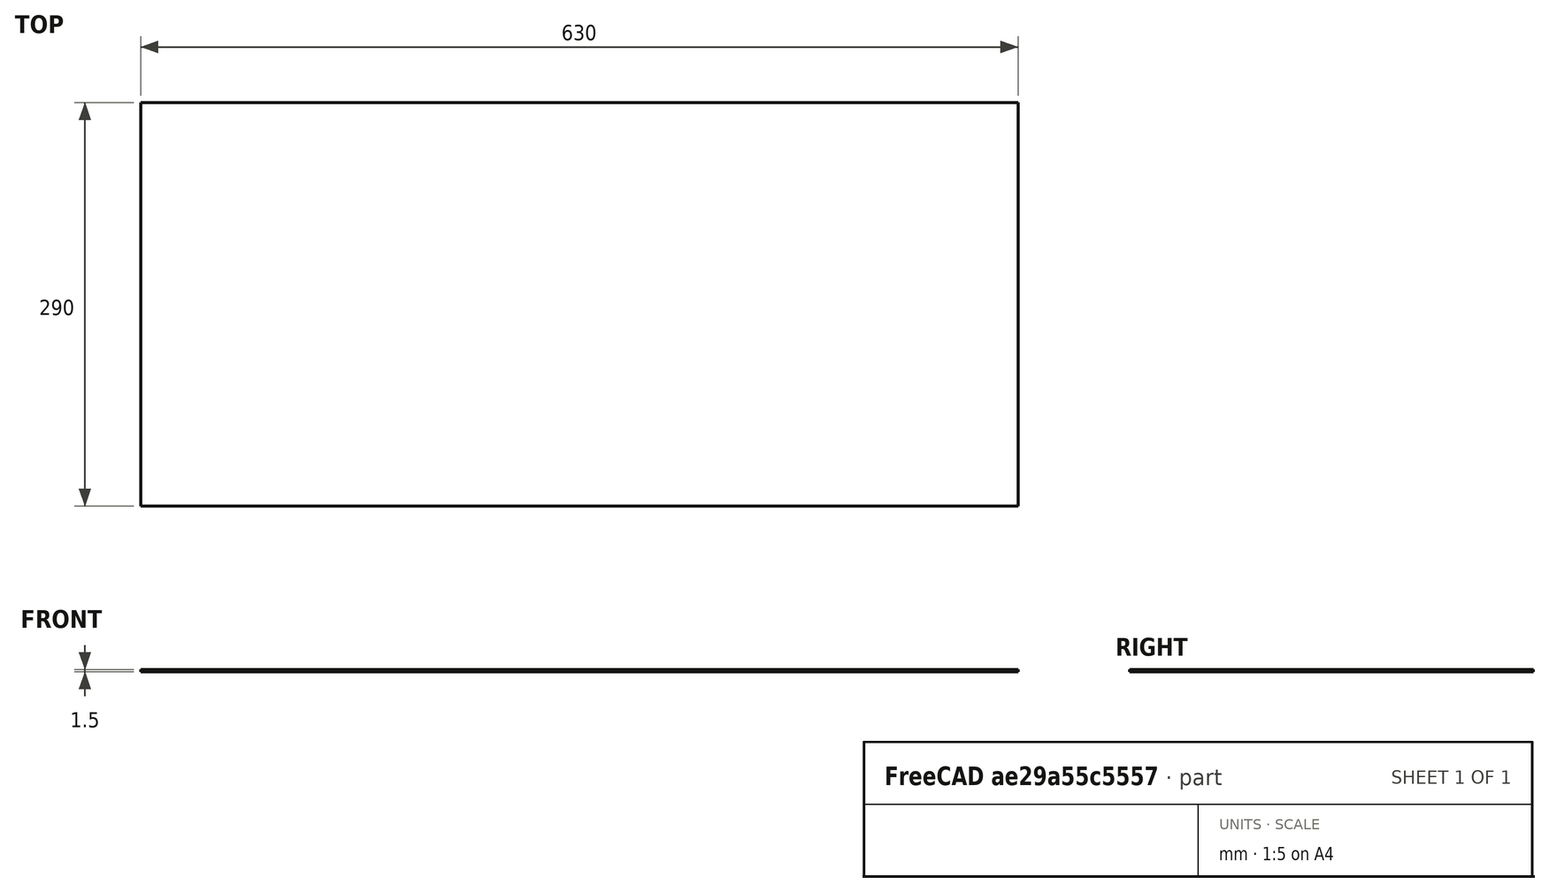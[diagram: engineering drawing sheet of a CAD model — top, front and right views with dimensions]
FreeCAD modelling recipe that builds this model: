
FCSTD DOCUMENT  (FreeCAD 0.21R33771 (Git))
Label: model
License: All rights reserved
LicenseURL: http://en.wikipedia.org/wiki/All_rights_reserved
objects: Sketcher::SketchObject×10, PartDesign::Pad×1, PartDesign::Body×1
note: 13 computed .brp shape members not serialized (recipe doc carries the construction recipe); baked Part::Feature solids carry a one-line shape summary decoded from their .brp

FEATURE [Sketcher::SketchObject] Sketch  label="plate"
  FullyConstrained = true
  MapMode = 5
  Support = -> [XY_Plane]
  sketch-geometry (4):
    g0: LineSegment StartX=-315 StartY=145 StartZ=0 EndX=315 EndY=145 EndZ=0
    g1: LineSegment StartX=315 StartY=145 StartZ=0 EndX=315 EndY=-145 EndZ=0
    g2: LineSegment StartX=315 StartY=-145 StartZ=0 EndX=-315 EndY=-145 EndZ=0
    g3: LineSegment StartX=-315 StartY=-145 StartZ=0 EndX=-315 EndY=145 EndZ=0
  constraints (12):
    c: Coincident(g0,g1)
    c: Coincident(g1,g2)
    c: Coincident(g2,g3)
    c: Coincident(g3,g0)
    c: Horizontal(g0)
    c: Horizontal(g2)
    c: Vertical(g1)
    c: Vertical(g3)
    c: DistanceX(g0,g0) = 630
    c: DistanceY(g1,g1) = 290
    c: DistanceX(g-1,g0) = 315
    c: DistanceY(g-1,g0) = 145
FEATURE [PartDesign::Pad] Pad
  Direction = (0,0,1)
  Length = 1.5
  Length2 = 10
  Profile = -> Sketch
  ReferenceAxis = -> Sketch [N_Axis]
  Type = 0
FEATURE [Sketcher::SketchObject] Sketch001  label="faderwing0"
  ExternalGeometry = -> [Pad]
  FullyConstrained = true
  MapMode = 5
  Placement = pos=(0,0,1.5) rot=(0,0,1;0rad)
  Support = -> [Pad]
  sketch-geometry (120):
    g0: Circle CenterX=-295 CenterY=128 CenterZ=0 NormalX=0 NormalY=0 NormalZ=1 AngleXU=0 Radius=5
    g1: LineSegment StartX=-302 StartY=111 StartZ=0 EndX=-288 EndY=111 EndZ=0
    g2: LineSegment StartX=-288 StartY=111 StartZ=0 EndX=-288 EndY=97 EndZ=0
    g3: LineSegment StartX=-288 StartY=97 StartZ=0 EndX=-302 EndY=97 EndZ=0
    g4: LineSegment StartX=-302 StartY=97 StartZ=0 EndX=-302 EndY=111 EndZ=0
    g5: LineSegment StartX=-309 StartY=44 StartZ=0 EndX=-281 EndY=44 EndZ=0
    g6: LineSegment StartX=-281 StartY=44 StartZ=0 EndX=-281 EndY=30 EndZ=0
    g7: LineSegment StartX=-281 StartY=30 StartZ=0 EndX=-309 EndY=30 EndZ=0
    g8: LineSegment StartX=-309 StartY=30 StartZ=0 EndX=-309 EndY=44 EndZ=0
    g9: LineSegment StartX=-302 StartY=91 StartZ=0 EndX=-288 EndY=91 EndZ=0
    g10: LineSegment StartX=-288 StartY=91 StartZ=0 EndX=-288 EndY=77 EndZ=0
    g11: LineSegment StartX=-288 StartY=77 StartZ=0 EndX=-302 EndY=77 EndZ=0
    g12: LineSegment StartX=-302 StartY=77 StartZ=0 EndX=-302 EndY=91 EndZ=0
    g13: Circle CenterX=-295 CenterY=60 CenterZ=0 NormalX=0 NormalY=0 NormalZ=1 AngleXU=0 Radius=5
    g14: Circle CenterX=-295 CenterY=15 CenterZ=0 NormalX=0 NormalY=0 NormalZ=1 AngleXU=0 Radius=1.5
    g15: LineSegment StartX=-296 StartY=9 StartZ=0 EndX=-294 EndY=9 EndZ=0
    g16: LineSegment StartX=-294 StartY=9 StartZ=0 EndX=-294 EndY=-99 EndZ=0
    g17: LineSegment StartX=-294 StartY=-99 StartZ=0 EndX=-296 EndY=-99 EndZ=0
    g18: LineSegment StartX=-296 StartY=-99 StartZ=0 EndX=-296 EndY=9 EndZ=0
    g19: Circle CenterX=-295 CenterY=-105 CenterZ=0 NormalX=0 NormalY=0 NormalZ=1 AngleXU=0 Radius=1.5
    g20: LineSegment StartX=-302 StartY=-121 StartZ=0 EndX=-288 EndY=-121 EndZ=0
    g21: LineSegment StartX=-288 StartY=-121 StartZ=0 EndX=-288 EndY=-135 EndZ=0
    g22: LineSegment StartX=-288 StartY=-135 StartZ=0 EndX=-302 EndY=-135 EndZ=0
    g23: LineSegment StartX=-302 StartY=-135 StartZ=0 EndX=-302 EndY=-121 EndZ=0
    g24: Circle CenterX=-265 CenterY=128 CenterZ=0 NormalX=0 NormalY=0 NormalZ=1 AngleXU=0 Radius=5
    g25: LineSegment StartX=-272 StartY=111 StartZ=0 EndX=-258 EndY=111 EndZ=0
    g26: LineSegment StartX=-258 StartY=111 StartZ=0 EndX=-258 EndY=97 EndZ=0
    g27: LineSegment StartX=-258 StartY=97 StartZ=0 EndX=-272 EndY=97 EndZ=0
    g28: LineSegment StartX=-272 StartY=97 StartZ=0 EndX=-272 EndY=111 EndZ=0
    g29: LineSegment StartX=-279 StartY=44 StartZ=0 EndX=-251 EndY=44 EndZ=0
    g30: LineSegment StartX=-251 StartY=44 StartZ=0 EndX=-251 EndY=30 EndZ=0
    g31: LineSegment StartX=-251 StartY=30 StartZ=0 EndX=-279 EndY=30 EndZ=0
    g32: LineSegment StartX=-279 StartY=30 StartZ=0 EndX=-279 EndY=44 EndZ=0
    g33: LineSegment StartX=-272 StartY=91 StartZ=0 EndX=-258 EndY=91 EndZ=0
    g34: LineSegment StartX=-258 StartY=91 StartZ=0 EndX=-258 EndY=77 EndZ=0
    g35: LineSegment StartX=-258 StartY=77 StartZ=0 EndX=-272 EndY=77 EndZ=0
    g36: LineSegment StartX=-272 StartY=77 StartZ=0 EndX=-272 EndY=91 EndZ=0
    g37: Circle CenterX=-265 CenterY=60 CenterZ=0 NormalX=0 NormalY=0 NormalZ=1 AngleXU=0 Radius=5
    g38: Circle CenterX=-265 CenterY=15 CenterZ=0 NormalX=0 NormalY=0 NormalZ=1 AngleXU=0 Radius=1.5
    g39: LineSegment StartX=-266 StartY=9 StartZ=0 EndX=-264 EndY=9 EndZ=0
    g40: LineSegment StartX=-264 StartY=9 StartZ=0 EndX=-264 EndY=-99 EndZ=0
    g41: LineSegment StartX=-264 StartY=-99 StartZ=0 EndX=-266 EndY=-99 EndZ=0
    g42: LineSegment StartX=-266 StartY=-99 StartZ=0 EndX=-266 EndY=9 EndZ=0
    g43: Circle CenterX=-265 CenterY=-105 CenterZ=0 NormalX=0 NormalY=0 NormalZ=1 AngleXU=0 Radius=1.5
    g44: LineSegment StartX=-272 StartY=-121 StartZ=0 EndX=-258 EndY=-121 EndZ=0
    g45: LineSegment StartX=-258 StartY=-121 StartZ=0 EndX=-258 EndY=-135 EndZ=0
    g46: LineSegment StartX=-258 StartY=-135 StartZ=0 EndX=-272 EndY=-135 EndZ=0
    g47: LineSegment StartX=-272 StartY=-135 StartZ=0 EndX=-272 EndY=-121 EndZ=0
    g48: Circle CenterX=-235 CenterY=128 CenterZ=0 NormalX=0 NormalY=0 NormalZ=1 AngleXU=0 Radius=5
    g49: LineSegment StartX=-242 StartY=111 StartZ=0 EndX=-228 EndY=111 EndZ=0
    g50: LineSegment StartX=-228 StartY=111 StartZ=0 EndX=-228 EndY=97 EndZ=0
    g51: LineSegment StartX=-228 StartY=97 StartZ=0 EndX=-242 EndY=97 EndZ=0
    g52: LineSegment StartX=-242 StartY=97 StartZ=0 EndX=-242 EndY=111 EndZ=0
    g53: LineSegment StartX=-249 StartY=44 StartZ=0 EndX=-221 EndY=44 EndZ=0
    g54: LineSegment StartX=-221 StartY=44 StartZ=0 EndX=-221 EndY=30 EndZ=0
    g55: LineSegment StartX=-221 StartY=30 StartZ=0 EndX=-249 EndY=30 EndZ=0
    g56: LineSegment StartX=-249 StartY=30 StartZ=0 EndX=-249 EndY=44 EndZ=0
    g57: LineSegment StartX=-242 StartY=91 StartZ=0 EndX=-228 EndY=91 EndZ=0
    g58: LineSegment StartX=-228 StartY=91 StartZ=0 EndX=-228 EndY=77 EndZ=0
    g59: LineSegment StartX=-228 StartY=77 StartZ=0 EndX=-242 EndY=77 EndZ=0
    g60: LineSegment StartX=-242 StartY=77 StartZ=0 EndX=-242 EndY=91 EndZ=0
    g61: Circle CenterX=-235 CenterY=60 CenterZ=0 NormalX=0 NormalY=0 NormalZ=1 AngleXU=0 Radius=5
    g62: Circle CenterX=-235 CenterY=15 CenterZ=0 NormalX=0 NormalY=0 NormalZ=1 AngleXU=0 Radius=1.5
    g63: LineSegment StartX=-236 StartY=9 StartZ=0 EndX=-234 EndY=9 EndZ=0
    g64: LineSegment StartX=-234 StartY=9 StartZ=0 EndX=-234 EndY=-99 EndZ=0
    g65: LineSegment StartX=-234 StartY=-99 StartZ=0 EndX=-236 EndY=-99 EndZ=0
    g66: LineSegment StartX=-236 StartY=-99 StartZ=0 EndX=-236 EndY=9 EndZ=0
    g67: Circle CenterX=-235 CenterY=-105 CenterZ=0 NormalX=0 NormalY=0 NormalZ=1 AngleXU=0 Radius=1.5
    g68: LineSegment StartX=-242 StartY=-121 StartZ=0 EndX=-228 EndY=-121 EndZ=0
    g69: LineSegment StartX=-228 StartY=-121 StartZ=0 EndX=-228 EndY=-135 EndZ=0
    g70: LineSegment StartX=-228 StartY=-135 StartZ=0 EndX=-242 EndY=-135 EndZ=0
    g71: LineSegment StartX=-242 StartY=-135 StartZ=0 EndX=-242 EndY=-121 EndZ=0
    g72: Circle CenterX=-205 CenterY=128 CenterZ=0 NormalX=0 NormalY=0 NormalZ=1 AngleXU=0 Radius=5
    g73: LineSegment StartX=-212 StartY=111 StartZ=0 EndX=-198 EndY=111 EndZ=0
    g74: LineSegment StartX=-198 StartY=111 StartZ=0 EndX=-198 EndY=97 EndZ=0
    g75: LineSegment StartX=-198 StartY=97 StartZ=0 EndX=-212 EndY=97 EndZ=0
    g76: LineSegment StartX=-212 StartY=97 StartZ=0 EndX=-212 EndY=111 EndZ=0
    g77: LineSegment StartX=-219 StartY=44 StartZ=0 EndX=-191 EndY=44 EndZ=0
    g78: LineSegment StartX=-191 StartY=44 StartZ=0 EndX=-191 EndY=30 EndZ=0
    g79: LineSegment StartX=-191 StartY=30 StartZ=0 EndX=-219 EndY=30 EndZ=0
    g80: LineSegment StartX=-219 StartY=30 StartZ=0 EndX=-219 EndY=44 EndZ=0
    g81: LineSegment StartX=-212 StartY=91 StartZ=0 EndX=-198 EndY=91 EndZ=0
    g82: LineSegment StartX=-198 StartY=91 StartZ=0 EndX=-198 EndY=77 EndZ=0
    g83: LineSegment StartX=-198 StartY=77 StartZ=0 EndX=-212 EndY=77 EndZ=0
    g84: LineSegment StartX=-212 StartY=77 StartZ=0 EndX=-212 EndY=91 EndZ=0
    g85: Circle CenterX=-205 CenterY=60 CenterZ=0 NormalX=0 NormalY=0 NormalZ=1 AngleXU=0 Radius=5
    g86: Circle CenterX=-205 CenterY=15 CenterZ=0 NormalX=0 NormalY=0 NormalZ=1 AngleXU=0 Radius=1.5
    g87: LineSegment StartX=-206 StartY=9 StartZ=0 EndX=-204 EndY=9 EndZ=0
    g88: LineSegment StartX=-204 StartY=9 StartZ=0 EndX=-204 EndY=-99 EndZ=0
    g89: LineSegment StartX=-204 StartY=-99 StartZ=0 EndX=-206 EndY=-99 EndZ=0
    g90: LineSegment StartX=-206 StartY=-99 StartZ=0 EndX=-206 EndY=9 EndZ=0
    g91: Circle CenterX=-205 CenterY=-105 CenterZ=0 NormalX=0 NormalY=0 NormalZ=1 AngleXU=0 Radius=1.5
    g92: LineSegment StartX=-212 StartY=-121 StartZ=0 EndX=-198 EndY=-121 EndZ=0
    g93: LineSegment StartX=-198 StartY=-121 StartZ=0 EndX=-198 EndY=-135 EndZ=0
    g94: LineSegment StartX=-198 StartY=-135 StartZ=0 EndX=-212 EndY=-135 EndZ=0
    g95: LineSegment StartX=-212 StartY=-135 StartZ=0 EndX=-212 EndY=-121 EndZ=0
    g96: Circle CenterX=-175 CenterY=128 CenterZ=0 NormalX=0 NormalY=0 NormalZ=1 AngleXU=0 Radius=5
    g97: LineSegment StartX=-182 StartY=111 StartZ=0 EndX=-168 EndY=111 EndZ=0
    g98: LineSegment StartX=-168 StartY=111 StartZ=0 EndX=-168 EndY=97 EndZ=0
    g99: LineSegment StartX=-168 StartY=97 StartZ=0 EndX=-182 EndY=97 EndZ=0
    g100: LineSegment StartX=-182 StartY=97 StartZ=0 EndX=-182 EndY=111 EndZ=0
    g101: LineSegment StartX=-189 StartY=44 StartZ=0 EndX=-161 EndY=44 EndZ=0
    g102: LineSegment StartX=-161 StartY=44 StartZ=0 EndX=-161 EndY=30 EndZ=0
    g103: LineSegment StartX=-161 StartY=30 StartZ=0 EndX=-189 EndY=30 EndZ=0
    g104: LineSegment StartX=-189 StartY=30 StartZ=0 EndX=-189 EndY=44 EndZ=0
    g105: LineSegment StartX=-182 StartY=91 StartZ=0 EndX=-168 EndY=91 EndZ=0
    g106: LineSegment StartX=-168 StartY=91 StartZ=0 EndX=-168 EndY=77 EndZ=0
    g107: LineSegment StartX=-168 StartY=77 StartZ=0 EndX=-182 EndY=77 EndZ=0
    g108: LineSegment StartX=-182 StartY=77 StartZ=0 EndX=-182 EndY=91 EndZ=0
    g109: Circle CenterX=-175 CenterY=60 CenterZ=0 NormalX=0 NormalY=0 NormalZ=1 AngleXU=0 Radius=5
    g110: Circle CenterX=-175 CenterY=15 CenterZ=0 NormalX=0 NormalY=0 NormalZ=1 AngleXU=0 Radius=1.5
    g111: LineSegment StartX=-176 StartY=9 StartZ=0 EndX=-174 EndY=9 EndZ=0
    g112: LineSegment StartX=-174 StartY=9 StartZ=0 EndX=-174 EndY=-99 EndZ=0
    g113: LineSegment StartX=-174 StartY=-99 StartZ=0 EndX=-176 EndY=-99 EndZ=0
    g114: LineSegment StartX=-176 StartY=-99 StartZ=0 EndX=-176 EndY=9 EndZ=0
    g115: Circle CenterX=-175 CenterY=-105 CenterZ=0 NormalX=0 NormalY=0 NormalZ=1 AngleXU=0 Radius=1.5
    g116: LineSegment StartX=-182 StartY=-121 StartZ=0 EndX=-168 EndY=-121 EndZ=0
    g117: LineSegment StartX=-168 StartY=-121 StartZ=0 EndX=-168 EndY=-135 EndZ=0
    g118: LineSegment StartX=-168 StartY=-135 StartZ=0 EndX=-182 EndY=-135 EndZ=0
    g119: LineSegment StartX=-182 StartY=-135 StartZ=0 EndX=-182 EndY=-121 EndZ=0
  constraints (360):
    c: Coincident(g1,g2)
    c: Coincident(g2,g3)
    c: Coincident(g3,g4)
    c: Coincident(g4,g1)
    c: Horizontal(g1)
    c: Horizontal(g3)
    c: Vertical(g2)
    c: Vertical(g4)
    c: Coincident(g5,g6)
    c: Coincident(g6,g7)
    c: Coincident(g7,g8)
    c: Coincident(g8,g5)
    c: Horizontal(g5)
    c: Horizontal(g7)
    c: Vertical(g6)
    c: Vertical(g8)
    c: Diameter(g0) = 10
    c: DistanceY(g4,g4) = 14
    c: DistanceX(g1,g1) = 14
    c: DistanceX(g-4,g0) = 20
    c: DistanceY(g0,g-4) = 17
    c: DistanceX(g1,g0) = 7
    c: DistanceY(g1,g0) = 17
    c: Coincident(g9,g10)
    c: Coincident(g10,g11)
    c: Coincident(g11,g12)
    c: Coincident(g12,g9)
    c: Horizontal(g9)
    c: Horizontal(g11)
    c: Vertical(g10)
    c: Vertical(g12)
    c: Equal(g4,g12) = 14
    c: Equal(g1,g9) = 14
    c: DistanceY(g9,g3) = 6
    c: DistanceX(g3,g9) = 0
    c: Equal(g0,g13) = 10
    c: DistanceX(g11,g13) = 7
    c: DistanceY(g13,g11) = 17
    c: DistanceY(g5,g13) = 16
    c: DistanceY(g8,g8) = 14
    c: DistanceX(g5,g5) = 28
    c: DistanceX(g5,g13) = 14
    c: Coincident(g15,g16)
    c: Coincident(g16,g17)
    c: Coincident(g17,g18)
    c: Coincident(g18,g15)
    c: Horizontal(g15)
    c: Horizontal(g17)
    c: Vertical(g16)
    c: Vertical(g18)
    c: Diameter(g14) = 3
    c: DistanceY(g18,g18) = 108
    c: DistanceX(g15,g15) = 2
    c: DistanceX(g15,g14) = 1
    c: DistanceY(g15,g14) = 6
    c: DistanceX(g7,g14) = 14
    c: DistanceY(g14,g7) = 15
    c: Equal(g14,g19) = 3
    c: DistanceY(g19,g17) = 6
    c: DistanceX(g17,g19) = 1
    c: Coincident(g20,g21)
    c: Coincident(g21,g22)
    c: Coincident(g22,g23)
    c: Coincident(g23,g20)
    c: Horizontal(g20)
    c: Horizontal(g22)
    c: Vertical(g21)
    c: Vertical(g23)
    c: Equal(g4,g23) = 14
    c: Equal(g1,g20) = 14
    c: DistanceX(g20,g19) = 7
    c: DistanceY(g20,g19) = 16
    c: Coincident(g25,g26)
    c: Coincident(g26,g27)
    c: Coincident(g27,g28)
    c: Coincident(g28,g25)
    c: Horizontal(g25)
    c: Horizontal(g27)
    c: Vertical(g26)
    c: Vertical(g28)
    c: Coincident(g29,g30)
    c: Coincident(g30,g31)
    c: Coincident(g31,g32)
    c: Coincident(g32,g29)
    c: Horizontal(g29)
    c: Horizontal(g31)
    c: Vertical(g30)
    c: Vertical(g32)
    c: Equal(g0,g24) = 10
    c: Equal(g4,g28) = 14
    c: Equal(g1,g25) = 14
    c: DistanceX(g25,g24) = 7
    c: Coincident(g33,g34)
    c: Coincident(g34,g35)
    c: Coincident(g35,g36)
    c: Coincident(g36,g33)
    c: Horizontal(g33)
    c: Horizontal(g35)
    c: Vertical(g34)
    c: Vertical(g36)
    c: Equal(g28,g36) = 14
    c: Equal(g25,g33) = 14
    c: DistanceX(g27,g33) = 0
    c: Equal(g24,g37) = 10
    c: DistanceX(g35,g37) = 7
    c: Equal(g8,g32) = 14
    c: Equal(g5,g29) = 28
    c: DistanceX(g29,g37) = 14
    c: Coincident(g39,g40)
    c: Coincident(g40,g41)
    c: Coincident(g41,g42)
    c: Coincident(g42,g39)
    c: Horizontal(g39)
    c: Horizontal(g41)
    c: Vertical(g40)
    c: Vertical(g42)
    c: Equal(g14,g38) = 3
    c: Equal(g18,g42) = 108
    c: Equal(g15,g39) = 2
    c: DistanceX(g39,g38) = 1
    c: DistanceX(g31,g38) = 14
    c: Equal(g38,g43) = 3
    c: DistanceX(g41,g43) = 1
    c: Coincident(g44,g45)
    c: Coincident(g45,g46)
    c: Coincident(g46,g47)
    c: Coincident(g47,g44)
    c: Horizontal(g44)
    c: Horizontal(g46)
    c: Vertical(g45)
    c: Vertical(g47)
    c: Equal(g28,g47) = 14
    c: Equal(g25,g44) = 14
    c: DistanceX(g44,g43) = 7
    c: DistanceY(g24,g0) = 0
    c: DistanceY(g25,g1) = 0
    c: DistanceY(g33,g9) = 0
    c: DistanceX(g0,g24) = 30
    c: DistanceY(g37,g13) = 0
    c: DistanceY(g29,g5) = 0
    c: DistanceY(g38,g14) = 0
    c: DistanceY(g39,g15) = 0
    c: DistanceY(g43,g19) = 0
    c: DistanceY(g44,g20) = 0
    c: Coincident(g49,g50)
    c: Coincident(g50,g51)
    c: Coincident(g51,g52)
    c: Coincident(g52,g49)
    c: Horizontal(g49)
    c: Horizontal(g51)
    c: Vertical(g50)
    c: Vertical(g52)
    c: Coincident(g53,g54)
    c: Coincident(g54,g55)
    c: Coincident(g55,g56)
    c: Coincident(g56,g53)
    c: Horizontal(g53)
    c: Horizontal(g55)
    c: Vertical(g54)
    c: Vertical(g56)
    c: DistanceX(g49,g48) = 7
    c: Coincident(g57,g58)
    c: Coincident(g58,g59)
    c: Coincident(g59,g60)
    c: Coincident(g60,g57)
    c: Horizontal(g57)
    c: Horizontal(g59)
    c: Vertical(g58)
    c: Vertical(g60)
    c: Equal(g52,g60) = 14
    c: Equal(g49,g57) = 14
    c: DistanceX(g51,g57) = 0
    c: Equal(g48,g61) = 10
    c: DistanceX(g59,g61) = 7
    c: DistanceX(g53,g61) = 14
    c: Coincident(g63,g64)
    c: Coincident(g64,g65)
    c: Coincident(g65,g66)
    c: Coincident(g66,g63)
    c: Horizontal(g63)
    c: Horizontal(g65)
    c: Vertical(g64)
    c: Vertical(g66)
    c: DistanceX(g63,g62) = 1
    c: DistanceX(g55,g62) = 14
    c: Equal(g62,g67) = 3
    c: DistanceX(g65,g67) = 1
    c: Coincident(g68,g69)
    c: Coincident(g69,g70)
    c: Coincident(g70,g71)
    c: Coincident(g71,g68)
    c: Horizontal(g68)
    c: Horizontal(g70)
    c: Vertical(g69)
    c: Vertical(g71)
    c: Equal(g52,g71) = 14
    c: Equal(g49,g68) = 14
    c: DistanceX(g68,g67) = 7
    c: Coincident(g73,g74)
    c: Coincident(g74,g75)
    c: Coincident(g75,g76)
    c: Coincident(g76,g73)
    c: Horizontal(g73)
    c: Horizontal(g75)
    c: Vertical(g74)
    c: Vertical(g76)
    c: Coincident(g77,g78)
    c: Coincident(g78,g79)
    c: Coincident(g79,g80)
    c: Coincident(g80,g77)
    c: Horizontal(g77)
    c: Horizontal(g79)
    c: Vertical(g78)
    c: Vertical(g80)
    c: DistanceX(g73,g72) = 7
    c: Coincident(g81,g82)
    c: Coincident(g82,g83)
    c: Coincident(g83,g84)
    c: Coincident(g84,g81)
    c: Horizontal(g81)
    c: Horizontal(g83)
    c: Vertical(g82)
    c: Vertical(g84)
    c: Equal(g76,g84) = 14
    c: Equal(g73,g81) = 14
    c: DistanceX(g75,g81) = 0
    c: Equal(g72,g85) = 10
    c: DistanceX(g83,g85) = 7
    c: DistanceX(g77,g85) = 14
    c: Coincident(g87,g88)
    c: Coincident(g88,g89)
    c: Coincident(g89,g90)
    c: Coincident(g90,g87)
    c: Horizontal(g87)
    c: Horizontal(g89)
    c: Vertical(g88)
    c: Vertical(g90)
    c: DistanceX(g87,g86) = 1
    c: DistanceX(g79,g86) = 14
    c: Equal(g86,g91) = 3
    c: DistanceX(g89,g91) = 1
    c: Coincident(g92,g93)
    c: Coincident(g93,g94)
    c: Coincident(g94,g95)
    c: Coincident(g95,g92)
    c: Horizontal(g92)
    c: Horizontal(g94)
    c: Vertical(g93)
    c: Vertical(g95)
    c: Equal(g76,g95) = 14
    c: Equal(g73,g92) = 14
    c: DistanceX(g92,g91) = 7
    c: Coincident(g97,g98)
    c: Coincident(g98,g99)
    c: Coincident(g99,g100)
    c: Coincident(g100,g97)
    c: Horizontal(g97)
    c: Horizontal(g99)
    c: Vertical(g98)
    c: Vertical(g100)
    c: Coincident(g101,g102)
    c: Coincident(g102,g103)
    c: Coincident(g103,g104)
    c: Coincident(g104,g101)
    c: Horizontal(g101)
    c: Horizontal(g103)
    c: Vertical(g102)
    c: Vertical(g104)
    c: DistanceX(g97,g96) = 7
    c: Coincident(g105,g106)
    c: Coincident(g106,g107)
    c: Coincident(g107,g108)
    c: Coincident(g108,g105)
    c: Horizontal(g105)
    c: Horizontal(g107)
    c: Vertical(g106)
    c: Vertical(g108)
    c: Equal(g100,g108) = 14
    c: Equal(g97,g105) = 14
    c: DistanceX(g99,g105) = 0
    c: Equal(g96,g109) = 10
    c: DistanceX(g107,g109) = 7
    c: DistanceX(g101,g109) = 14
    c: Coincident(g111,g112)
    c: Coincident(g112,g113)
    c: Coincident(g113,g114)
    c: Coincident(g114,g111)
    c: Horizontal(g111)
    c: Horizontal(g113)
    c: Vertical(g112)
    c: Vertical(g114)
    c: DistanceX(g111,g110) = 1
    c: DistanceX(g103,g110) = 14
    c: Equal(g110,g115) = 3
    c: DistanceX(g113,g115) = 1
    c: Coincident(g116,g117)
    c: Coincident(g117,g118)
    c: Coincident(g118,g119)
    c: Coincident(g119,g116)
    c: Horizontal(g116)
    c: Horizontal(g118)
    c: Vertical(g117)
    c: Vertical(g119)
    c: Equal(g100,g119) = 14
    c: Equal(g97,g116) = 14
    c: DistanceX(g116,g115) = 7
    c: DistanceX(g24,g48) = 30
    c: DistanceX(g48,g72) = 30
    c: DistanceX(g72,g96) = 30
    c: DistanceY(g48,g72) = 0
    c: DistanceY(g72,g96) = 0
    c: DistanceY(g48,g24) = 0
    c: DistanceY(g25,g49) = 0
    c: DistanceY(g49,g73) = 0
    c: DistanceY(g73,g97) = 0
    c: DistanceY(g33,g57) = 0
    c: DistanceY(g57,g81) = 0
    c: DistanceY(g81,g105) = 0
    c: Equal(g48,g72)
    c: Equal(g48,g24)
    c: Equal(g72,g96)
    c: Equal(g52,g28)
    c: Equal(g52,g76)
    c: Equal(g76,g100)
    c: Equal(g25,g49)
    c: Equal(g49,g73)
    c: Equal(g73,g97)
    c: DistanceY(g37,g61) = 0
    c: DistanceY(g61,g85) = 0
    c: DistanceY(g85,g109) = 0
    c: Equal(g29,g53)
    c: Equal(g53,g77)
    c: Equal(g77,g101)
    c: Equal(g56,g32)
    c: Equal(g56,g80)
    c: Equal(g80,g104)
    c: DistanceY(g29,g53) = 0
    c: DistanceY(g53,g77) = 0
    c: DistanceY(g77,g101) = 0
    c: Equal(g38,g62)
    c: Equal(g62,g86)
    c: Equal(g86,g110)
    c: DistanceY(g86,g110) = 0
    c: DistanceY(g62,g86) = 0
    c: DistanceY(g38,g62) = 0
    c: Equal(g66,g42)
    c: Equal(g90,g66)
    c: Equal(g114,g90)
    c: Equal(g39,g63)
    c: Equal(g87,g63)
    c: Equal(g111,g87)
    c: DistanceY(g87,g111) = 0
    c: DistanceY(g63,g87) = 0
    c: DistanceY(g39,g63) = 0
    c: DistanceY(g43,g67) = 0
    c: DistanceY(g91,g115) = 0
    c: DistanceY(g67,g91) = 0
    c: DistanceY(g92,g116) = 0
    c: DistanceY(g68,g92) = 0
    c: DistanceY(g44,g68) = 0
FEATURE [Sketcher::SketchObject] Sketch002  label="faderwing1"
  ExternalGeometry = -> [Pad]
  FullyConstrained = true
  MapMode = 5
  Placement = pos=(0,0,1.5) rot=(0,0,1;0rad)
  Support = -> [Pad]
  sketch-geometry (120):
    g0: Circle CenterX=-115 CenterY=128 CenterZ=0 NormalX=0 NormalY=0 NormalZ=1 AngleXU=0 Radius=5
    g1: LineSegment StartX=-122 StartY=111 StartZ=0 EndX=-108 EndY=111 EndZ=0
    g2: LineSegment StartX=-108 StartY=111 StartZ=0 EndX=-108 EndY=97 EndZ=0
    g3: LineSegment StartX=-108 StartY=97 StartZ=0 EndX=-122 EndY=97 EndZ=0
    g4: LineSegment StartX=-122 StartY=97 StartZ=0 EndX=-122 EndY=111 EndZ=0
    g5: LineSegment StartX=-129 StartY=44 StartZ=0 EndX=-101 EndY=44 EndZ=0
    g6: LineSegment StartX=-101 StartY=44 StartZ=0 EndX=-101 EndY=30 EndZ=0
    g7: LineSegment StartX=-101 StartY=30 StartZ=0 EndX=-129 EndY=30 EndZ=0
    g8: LineSegment StartX=-129 StartY=30 StartZ=0 EndX=-129 EndY=44 EndZ=0
    g9: LineSegment StartX=-122 StartY=91 StartZ=0 EndX=-108 EndY=91 EndZ=0
    g10: LineSegment StartX=-108 StartY=91 StartZ=0 EndX=-108 EndY=77 EndZ=0
    g11: LineSegment StartX=-108 StartY=77 StartZ=0 EndX=-122 EndY=77 EndZ=0
    g12: LineSegment StartX=-122 StartY=77 StartZ=0 EndX=-122 EndY=91 EndZ=0
    g13: Circle CenterX=-115 CenterY=60 CenterZ=0 NormalX=0 NormalY=0 NormalZ=1 AngleXU=0 Radius=5
    g14: Circle CenterX=-115 CenterY=15 CenterZ=0 NormalX=0 NormalY=0 NormalZ=1 AngleXU=0 Radius=1.5
    g15: LineSegment StartX=-116 StartY=9 StartZ=0 EndX=-114 EndY=9 EndZ=0
    g16: LineSegment StartX=-114 StartY=9 StartZ=0 EndX=-114 EndY=-99 EndZ=0
    g17: LineSegment StartX=-114 StartY=-99 StartZ=0 EndX=-116 EndY=-99 EndZ=0
    g18: LineSegment StartX=-116 StartY=-99 StartZ=0 EndX=-116 EndY=9 EndZ=0
    g19: Circle CenterX=-115 CenterY=-105 CenterZ=0 NormalX=0 NormalY=0 NormalZ=1 AngleXU=0 Radius=1.5
    g20: LineSegment StartX=-122 StartY=-121 StartZ=0 EndX=-108 EndY=-121 EndZ=0
    g21: LineSegment StartX=-108 StartY=-121 StartZ=0 EndX=-108 EndY=-135 EndZ=0
    g22: LineSegment StartX=-108 StartY=-135 StartZ=0 EndX=-122 EndY=-135 EndZ=0
    g23: LineSegment StartX=-122 StartY=-135 StartZ=0 EndX=-122 EndY=-121 EndZ=0
    g24: Circle CenterX=-85 CenterY=128 CenterZ=0 NormalX=0 NormalY=0 NormalZ=1 AngleXU=0 Radius=5
    g25: LineSegment StartX=-92 StartY=111 StartZ=0 EndX=-78 EndY=111 EndZ=0
    g26: LineSegment StartX=-78 StartY=111 StartZ=0 EndX=-78 EndY=97 EndZ=0
    g27: LineSegment StartX=-78 StartY=97 StartZ=0 EndX=-92 EndY=97 EndZ=0
    g28: LineSegment StartX=-92 StartY=97 StartZ=0 EndX=-92 EndY=111 EndZ=0
    g29: LineSegment StartX=-99 StartY=44 StartZ=0 EndX=-71 EndY=44 EndZ=0
    g30: LineSegment StartX=-71 StartY=44 StartZ=0 EndX=-71 EndY=30 EndZ=0
    g31: LineSegment StartX=-71 StartY=30 StartZ=0 EndX=-99 EndY=30 EndZ=0
    g32: LineSegment StartX=-99 StartY=30 StartZ=0 EndX=-99 EndY=44 EndZ=0
    g33: LineSegment StartX=-92 StartY=91 StartZ=0 EndX=-78 EndY=91 EndZ=0
    g34: LineSegment StartX=-78 StartY=91 StartZ=0 EndX=-78 EndY=77 EndZ=0
    g35: LineSegment StartX=-78 StartY=77 StartZ=0 EndX=-92 EndY=77 EndZ=0
    g36: LineSegment StartX=-92 StartY=77 StartZ=0 EndX=-92 EndY=91 EndZ=0
    g37: Circle CenterX=-85 CenterY=60 CenterZ=0 NormalX=0 NormalY=0 NormalZ=1 AngleXU=0 Radius=5
    g38: Circle CenterX=-85 CenterY=15 CenterZ=0 NormalX=0 NormalY=0 NormalZ=1 AngleXU=0 Radius=1.5
    g39: LineSegment StartX=-86 StartY=9 StartZ=0 EndX=-84 EndY=9 EndZ=0
    g40: LineSegment StartX=-84 StartY=9 StartZ=0 EndX=-84 EndY=-99 EndZ=0
    g41: LineSegment StartX=-84 StartY=-99 StartZ=0 EndX=-86 EndY=-99 EndZ=0
    g42: LineSegment StartX=-86 StartY=-99 StartZ=0 EndX=-86 EndY=9 EndZ=0
    g43: Circle CenterX=-85 CenterY=-105 CenterZ=0 NormalX=0 NormalY=0 NormalZ=1 AngleXU=0 Radius=1.5
    g44: LineSegment StartX=-92 StartY=-121 StartZ=0 EndX=-78 EndY=-121 EndZ=0
    g45: LineSegment StartX=-78 StartY=-121 StartZ=0 EndX=-78 EndY=-135 EndZ=0
    g46: LineSegment StartX=-78 StartY=-135 StartZ=0 EndX=-92 EndY=-135 EndZ=0
    g47: LineSegment StartX=-92 StartY=-135 StartZ=0 EndX=-92 EndY=-121 EndZ=0
    g48: Circle CenterX=-55 CenterY=128 CenterZ=0 NormalX=0 NormalY=0 NormalZ=1 AngleXU=0 Radius=5
    g49: LineSegment StartX=-62 StartY=111 StartZ=0 EndX=-48 EndY=111 EndZ=0
    g50: LineSegment StartX=-48 StartY=111 StartZ=0 EndX=-48 EndY=97 EndZ=0
    g51: LineSegment StartX=-48 StartY=97 StartZ=0 EndX=-62 EndY=97 EndZ=0
    g52: LineSegment StartX=-62 StartY=97 StartZ=0 EndX=-62 EndY=111 EndZ=0
    g53: LineSegment StartX=-69 StartY=44 StartZ=0 EndX=-41 EndY=44 EndZ=0
    g54: LineSegment StartX=-41 StartY=44 StartZ=0 EndX=-41 EndY=30 EndZ=0
    g55: LineSegment StartX=-41 StartY=30 StartZ=0 EndX=-69 EndY=30 EndZ=0
    g56: LineSegment StartX=-69 StartY=30 StartZ=0 EndX=-69 EndY=44 EndZ=0
    g57: LineSegment StartX=-62 StartY=91 StartZ=0 EndX=-48 EndY=91 EndZ=0
    g58: LineSegment StartX=-48 StartY=91 StartZ=0 EndX=-48 EndY=77 EndZ=0
    g59: LineSegment StartX=-48 StartY=77 StartZ=0 EndX=-62 EndY=77 EndZ=0
    g60: LineSegment StartX=-62 StartY=77 StartZ=0 EndX=-62 EndY=91 EndZ=0
    g61: Circle CenterX=-55 CenterY=60 CenterZ=0 NormalX=0 NormalY=0 NormalZ=1 AngleXU=0 Radius=5
    g62: Circle CenterX=-55 CenterY=15 CenterZ=0 NormalX=0 NormalY=0 NormalZ=1 AngleXU=0 Radius=1.5
    g63: LineSegment StartX=-56 StartY=9 StartZ=0 EndX=-54 EndY=9 EndZ=0
    g64: LineSegment StartX=-54 StartY=9 StartZ=0 EndX=-54 EndY=-99 EndZ=0
    g65: LineSegment StartX=-54 StartY=-99 StartZ=0 EndX=-56 EndY=-99 EndZ=0
    g66: LineSegment StartX=-56 StartY=-99 StartZ=0 EndX=-56 EndY=9 EndZ=0
    g67: Circle CenterX=-55 CenterY=-105 CenterZ=0 NormalX=0 NormalY=0 NormalZ=1 AngleXU=0 Radius=1.5
    g68: LineSegment StartX=-62 StartY=-121 StartZ=0 EndX=-48 EndY=-121 EndZ=0
    g69: LineSegment StartX=-48 StartY=-121 StartZ=0 EndX=-48 EndY=-135 EndZ=0
    g70: LineSegment StartX=-48 StartY=-135 StartZ=0 EndX=-62 EndY=-135 EndZ=0
    g71: LineSegment StartX=-62 StartY=-135 StartZ=0 EndX=-62 EndY=-121 EndZ=0
    g72: Circle CenterX=-25 CenterY=128 CenterZ=0 NormalX=0 NormalY=0 NormalZ=1 AngleXU=0 Radius=5
    g73: LineSegment StartX=-32 StartY=111 StartZ=0 EndX=-18 EndY=111 EndZ=0
    g74: LineSegment StartX=-18 StartY=111 StartZ=0 EndX=-18 EndY=97 EndZ=0
    g75: LineSegment StartX=-18 StartY=97 StartZ=0 EndX=-32 EndY=97 EndZ=0
    g76: LineSegment StartX=-32 StartY=97 StartZ=0 EndX=-32 EndY=111 EndZ=0
    g77: LineSegment StartX=-39 StartY=44 StartZ=0 EndX=-11 EndY=44 EndZ=0
    g78: LineSegment StartX=-11 StartY=44 StartZ=0 EndX=-11 EndY=30 EndZ=0
    g79: LineSegment StartX=-11 StartY=30 StartZ=0 EndX=-39 EndY=30 EndZ=0
    g80: LineSegment StartX=-39 StartY=30 StartZ=0 EndX=-39 EndY=44 EndZ=0
    g81: LineSegment StartX=-32 StartY=91 StartZ=0 EndX=-18 EndY=91 EndZ=0
    g82: LineSegment StartX=-18 StartY=91 StartZ=0 EndX=-18 EndY=77 EndZ=0
    g83: LineSegment StartX=-18 StartY=77 StartZ=0 EndX=-32 EndY=77 EndZ=0
    g84: LineSegment StartX=-32 StartY=77 StartZ=0 EndX=-32 EndY=91 EndZ=0
    g85: Circle CenterX=-25 CenterY=60 CenterZ=0 NormalX=0 NormalY=0 NormalZ=1 AngleXU=0 Radius=5
    g86: Circle CenterX=-25 CenterY=15 CenterZ=0 NormalX=0 NormalY=0 NormalZ=1 AngleXU=0 Radius=1.5
    g87: LineSegment StartX=-26 StartY=9 StartZ=0 EndX=-24 EndY=9 EndZ=0
    g88: LineSegment StartX=-24 StartY=9 StartZ=0 EndX=-24 EndY=-99 EndZ=0
    g89: LineSegment StartX=-24 StartY=-99 StartZ=0 EndX=-26 EndY=-99 EndZ=0
    g90: LineSegment StartX=-26 StartY=-99 StartZ=0 EndX=-26 EndY=9 EndZ=0
    g91: Circle CenterX=-25 CenterY=-105 CenterZ=0 NormalX=0 NormalY=0 NormalZ=1 AngleXU=0 Radius=1.5
    g92: LineSegment StartX=-32 StartY=-121 StartZ=0 EndX=-18 EndY=-121 EndZ=0
    g93: LineSegment StartX=-18 StartY=-121 StartZ=0 EndX=-18 EndY=-135 EndZ=0
    g94: LineSegment StartX=-18 StartY=-135 StartZ=0 EndX=-32 EndY=-135 EndZ=0
    g95: LineSegment StartX=-32 StartY=-135 StartZ=0 EndX=-32 EndY=-121 EndZ=0
    g96: Circle CenterX=5 CenterY=128 CenterZ=0 NormalX=0 NormalY=0 NormalZ=1 AngleXU=0 Radius=5
    g97: LineSegment StartX=-2 StartY=111 StartZ=0 EndX=12 EndY=111 EndZ=0
    g98: LineSegment StartX=12 StartY=111 StartZ=0 EndX=12 EndY=97 EndZ=0
    g99: LineSegment StartX=12 StartY=97 StartZ=0 EndX=-2 EndY=97 EndZ=0
    g100: LineSegment StartX=-2 StartY=97 StartZ=0 EndX=-2 EndY=111 EndZ=0
    g101: LineSegment StartX=-9 StartY=44 StartZ=0 EndX=19 EndY=44 EndZ=0
    g102: LineSegment StartX=19 StartY=44 StartZ=0 EndX=19 EndY=30 EndZ=0
    g103: LineSegment StartX=19 StartY=30 StartZ=0 EndX=-9 EndY=30 EndZ=0
    g104: LineSegment StartX=-9 StartY=30 StartZ=0 EndX=-9 EndY=44 EndZ=0
    g105: LineSegment StartX=-2 StartY=91 StartZ=0 EndX=12 EndY=91 EndZ=0
    g106: LineSegment StartX=12 StartY=91 StartZ=0 EndX=12 EndY=77 EndZ=0
    g107: LineSegment StartX=12 StartY=77 StartZ=0 EndX=-2 EndY=77 EndZ=0
    g108: LineSegment StartX=-2 StartY=77 StartZ=0 EndX=-2 EndY=91 EndZ=0
    g109: Circle CenterX=5 CenterY=60 CenterZ=0 NormalX=0 NormalY=0 NormalZ=1 AngleXU=0 Radius=5
    g110: Circle CenterX=5 CenterY=15 CenterZ=0 NormalX=0 NormalY=0 NormalZ=1 AngleXU=0 Radius=1.5
    g111: LineSegment StartX=4 StartY=9 StartZ=0 EndX=6 EndY=9 EndZ=0
    g112: LineSegment StartX=6 StartY=9 StartZ=0 EndX=6 EndY=-99 EndZ=0
    g113: LineSegment StartX=6 StartY=-99 StartZ=0 EndX=4 EndY=-99 EndZ=0
    g114: LineSegment StartX=4 StartY=-99 StartZ=0 EndX=4 EndY=9 EndZ=0
    g115: Circle CenterX=5 CenterY=-105 CenterZ=0 NormalX=0 NormalY=0 NormalZ=1 AngleXU=0 Radius=1.5
    g116: LineSegment StartX=-2 StartY=-121 StartZ=0 EndX=12 EndY=-121 EndZ=0
    g117: LineSegment StartX=12 StartY=-121 StartZ=0 EndX=12 EndY=-135 EndZ=0
    g118: LineSegment StartX=12 StartY=-135 StartZ=0 EndX=-2 EndY=-135 EndZ=0
    g119: LineSegment StartX=-2 StartY=-135 StartZ=0 EndX=-2 EndY=-121 EndZ=0
  constraints (360):
    c: Coincident(g1,g2)
    c: Coincident(g2,g3)
    c: Coincident(g3,g4)
    c: Coincident(g4,g1)
    c: Horizontal(g1)
    c: Horizontal(g3)
    c: Vertical(g2)
    c: Vertical(g4)
    c: Coincident(g5,g6)
    c: Coincident(g6,g7)
    c: Coincident(g7,g8)
    c: Coincident(g8,g5)
    c: Horizontal(g5)
    c: Horizontal(g7)
    c: Vertical(g6)
    c: Vertical(g8)
    c: Diameter(g0) = 10
    c: DistanceY(g4,g4) = 14
    c: DistanceX(g1,g1) = 14
    c: DistanceX(g-4,g0) = 200
    c: DistanceY(g0,g-4) = 17
    c: DistanceX(g1,g0) = 7
    c: DistanceY(g1,g0) = 17
    c: Coincident(g9,g10)
    c: Coincident(g10,g11)
    c: Coincident(g11,g12)
    c: Coincident(g12,g9)
    c: Horizontal(g9)
    c: Horizontal(g11)
    c: Vertical(g10)
    c: Vertical(g12)
    c: Equal(g4,g12) = 14
    c: Equal(g1,g9) = 14
    c: DistanceY(g9,g3) = 6
    c: DistanceX(g3,g9) = 0
    c: Equal(g0,g13) = 10
    c: DistanceX(g11,g13) = 7
    c: DistanceY(g13,g11) = 17
    c: DistanceY(g5,g13) = 16
    c: DistanceY(g8,g8) = 14
    c: DistanceX(g5,g5) = 28
    c: DistanceX(g5,g13) = 14
    c: Coincident(g15,g16)
    c: Coincident(g16,g17)
    c: Coincident(g17,g18)
    c: Coincident(g18,g15)
    c: Horizontal(g15)
    c: Horizontal(g17)
    c: Vertical(g16)
    c: Vertical(g18)
    c: Diameter(g14) = 3
    c: DistanceY(g18,g18) = 108
    c: DistanceX(g15,g15) = 2
    c: DistanceX(g15,g14) = 1
    c: DistanceY(g15,g14) = 6
    c: DistanceX(g7,g14) = 14
    c: DistanceY(g14,g7) = 15
    c: Equal(g14,g19) = 3
    c: DistanceY(g19,g17) = 6
    c: DistanceX(g17,g19) = 1
    c: Coincident(g20,g21)
    c: Coincident(g21,g22)
    c: Coincident(g22,g23)
    c: Coincident(g23,g20)
    c: Horizontal(g20)
    c: Horizontal(g22)
    c: Vertical(g21)
    c: Vertical(g23)
    c: Equal(g4,g23) = 14
    c: Equal(g1,g20) = 14
    c: DistanceX(g20,g19) = 7
    c: DistanceY(g20,g19) = 16
    c: Coincident(g25,g26)
    c: Coincident(g26,g27)
    c: Coincident(g27,g28)
    c: Coincident(g28,g25)
    c: Horizontal(g25)
    c: Horizontal(g27)
    c: Vertical(g26)
    c: Vertical(g28)
    c: Coincident(g29,g30)
    c: Coincident(g30,g31)
    c: Coincident(g31,g32)
    c: Coincident(g32,g29)
    c: Horizontal(g29)
    c: Horizontal(g31)
    c: Vertical(g30)
    c: Vertical(g32)
    c: Equal(g0,g24) = 10
    c: Equal(g4,g28) = 14
    c: Equal(g1,g25) = 14
    c: DistanceX(g25,g24) = 7
    c: Coincident(g33,g34)
    c: Coincident(g34,g35)
    c: Coincident(g35,g36)
    c: Coincident(g36,g33)
    c: Horizontal(g33)
    c: Horizontal(g35)
    c: Vertical(g34)
    c: Vertical(g36)
    c: Equal(g28,g36) = 14
    c: Equal(g25,g33) = 14
    c: DistanceX(g27,g33) = 0
    c: Equal(g24,g37) = 10
    c: DistanceX(g35,g37) = 7
    c: Equal(g8,g32) = 14
    c: Equal(g5,g29) = 28
    c: DistanceX(g29,g37) = 14
    c: Coincident(g39,g40)
    c: Coincident(g40,g41)
    c: Coincident(g41,g42)
    c: Coincident(g42,g39)
    c: Horizontal(g39)
    c: Horizontal(g41)
    c: Vertical(g40)
    c: Vertical(g42)
    c: Equal(g14,g38) = 3
    c: Equal(g18,g42) = 108
    c: Equal(g15,g39) = 2
    c: DistanceX(g39,g38) = 1
    c: DistanceX(g31,g38) = 14
    c: Equal(g38,g43) = 3
    c: DistanceX(g41,g43) = 1
    c: Coincident(g44,g45)
    c: Coincident(g45,g46)
    c: Coincident(g46,g47)
    c: Coincident(g47,g44)
    c: Horizontal(g44)
    c: Horizontal(g46)
    c: Vertical(g45)
    c: Vertical(g47)
    c: Equal(g28,g47) = 14
    c: Equal(g25,g44) = 14
    c: DistanceX(g44,g43) = 7
    c: DistanceY(g24,g0) = 0
    c: DistanceY(g25,g1) = 0
    c: DistanceY(g33,g9) = 0
    c: DistanceX(g0,g24) = 30
    c: DistanceY(g37,g13) = 0
    c: DistanceY(g29,g5) = 0
    c: DistanceY(g38,g14) = 0
    c: DistanceY(g39,g15) = 0
    c: DistanceY(g43,g19) = 0
    c: DistanceY(g44,g20) = 0
    c: Coincident(g49,g50)
    c: Coincident(g50,g51)
    c: Coincident(g51,g52)
    c: Coincident(g52,g49)
    c: Horizontal(g49)
    c: Horizontal(g51)
    c: Vertical(g50)
    c: Vertical(g52)
    c: Coincident(g53,g54)
    c: Coincident(g54,g55)
    c: Coincident(g55,g56)
    c: Coincident(g56,g53)
    c: Horizontal(g53)
    c: Horizontal(g55)
    c: Vertical(g54)
    c: Vertical(g56)
    c: DistanceX(g49,g48) = 7
    c: Coincident(g57,g58)
    c: Coincident(g58,g59)
    c: Coincident(g59,g60)
    c: Coincident(g60,g57)
    c: Horizontal(g57)
    c: Horizontal(g59)
    c: Vertical(g58)
    c: Vertical(g60)
    c: Equal(g52,g60) = 14
    c: Equal(g49,g57) = 14
    c: DistanceX(g51,g57) = 0
    c: Equal(g48,g61) = 10
    c: DistanceX(g59,g61) = 7
    c: DistanceX(g53,g61) = 14
    c: Coincident(g63,g64)
    c: Coincident(g64,g65)
    c: Coincident(g65,g66)
    c: Coincident(g66,g63)
    c: Horizontal(g63)
    c: Horizontal(g65)
    c: Vertical(g64)
    c: Vertical(g66)
    c: DistanceX(g63,g62) = 1
    c: DistanceX(g55,g62) = 14
    c: Equal(g62,g67) = 3
    c: DistanceX(g65,g67) = 1
    c: Coincident(g68,g69)
    c: Coincident(g69,g70)
    c: Coincident(g70,g71)
    c: Coincident(g71,g68)
    c: Horizontal(g68)
    c: Horizontal(g70)
    c: Vertical(g69)
    c: Vertical(g71)
    c: Equal(g52,g71) = 14
    c: Equal(g49,g68) = 14
    c: DistanceX(g68,g67) = 7
    c: Coincident(g73,g74)
    c: Coincident(g74,g75)
    c: Coincident(g75,g76)
    c: Coincident(g76,g73)
    c: Horizontal(g73)
    c: Horizontal(g75)
    c: Vertical(g74)
    c: Vertical(g76)
    c: Coincident(g77,g78)
    c: Coincident(g78,g79)
    c: Coincident(g79,g80)
    c: Coincident(g80,g77)
    c: Horizontal(g77)
    c: Horizontal(g79)
    c: Vertical(g78)
    c: Vertical(g80)
    c: DistanceX(g73,g72) = 7
    c: Coincident(g81,g82)
    c: Coincident(g82,g83)
    c: Coincident(g83,g84)
    c: Coincident(g84,g81)
    c: Horizontal(g81)
    c: Horizontal(g83)
    c: Vertical(g82)
    c: Vertical(g84)
    c: Equal(g76,g84) = 14
    c: Equal(g73,g81) = 14
    c: DistanceX(g75,g81) = 0
    c: Equal(g72,g85) = 10
    c: DistanceX(g83,g85) = 7
    c: DistanceX(g77,g85) = 14
    c: Coincident(g87,g88)
    c: Coincident(g88,g89)
    c: Coincident(g89,g90)
    c: Coincident(g90,g87)
    c: Horizontal(g87)
    c: Horizontal(g89)
    c: Vertical(g88)
    c: Vertical(g90)
    c: DistanceX(g87,g86) = 1
    c: DistanceX(g79,g86) = 14
    c: Equal(g86,g91) = 3
    c: DistanceX(g89,g91) = 1
    c: Coincident(g92,g93)
    c: Coincident(g93,g94)
    c: Coincident(g94,g95)
    c: Coincident(g95,g92)
    c: Horizontal(g92)
    c: Horizontal(g94)
    c: Vertical(g93)
    c: Vertical(g95)
    c: Equal(g76,g95) = 14
    c: Equal(g73,g92) = 14
    c: DistanceX(g92,g91) = 7
    c: Coincident(g97,g98)
    c: Coincident(g98,g99)
    c: Coincident(g99,g100)
    c: Coincident(g100,g97)
    c: Horizontal(g97)
    c: Horizontal(g99)
    c: Vertical(g98)
    c: Vertical(g100)
    c: Coincident(g101,g102)
    c: Coincident(g102,g103)
    c: Coincident(g103,g104)
    c: Coincident(g104,g101)
    c: Horizontal(g101)
    c: Horizontal(g103)
    c: Vertical(g102)
    c: Vertical(g104)
    c: DistanceX(g97,g96) = 7
    c: Coincident(g105,g106)
    c: Coincident(g106,g107)
    c: Coincident(g107,g108)
    c: Coincident(g108,g105)
    c: Horizontal(g105)
    c: Horizontal(g107)
    c: Vertical(g106)
    c: Vertical(g108)
    c: Equal(g100,g108) = 14
    c: Equal(g97,g105) = 14
    c: DistanceX(g99,g105) = 0
    c: Equal(g96,g109) = 10
    c: DistanceX(g107,g109) = 7
    c: DistanceX(g101,g109) = 14
    c: Coincident(g111,g112)
    c: Coincident(g112,g113)
    c: Coincident(g113,g114)
    c: Coincident(g114,g111)
    c: Horizontal(g111)
    c: Horizontal(g113)
    c: Vertical(g112)
    c: Vertical(g114)
    c: DistanceX(g111,g110) = 1
    c: DistanceX(g103,g110) = 14
    c: Equal(g110,g115) = 3
    c: DistanceX(g113,g115) = 1
    c: Coincident(g116,g117)
    c: Coincident(g117,g118)
    c: Coincident(g118,g119)
    c: Coincident(g119,g116)
    c: Horizontal(g116)
    c: Horizontal(g118)
    c: Vertical(g117)
    c: Vertical(g119)
    c: Equal(g100,g119) = 14
    c: Equal(g97,g116) = 14
    c: DistanceX(g116,g115) = 7
    c: DistanceX(g24,g48) = 30
    c: DistanceX(g48,g72) = 30
    c: DistanceX(g72,g96) = 30
    c: DistanceY(g48,g72) = 0
    c: DistanceY(g72,g96) = 0
    c: DistanceY(g48,g24) = 0
    c: DistanceY(g25,g49) = 0
    c: DistanceY(g49,g73) = 0
    c: DistanceY(g73,g97) = 0
    c: DistanceY(g33,g57) = 0
    c: DistanceY(g57,g81) = 0
    c: DistanceY(g81,g105) = 0
    c: Equal(g48,g72)
    c: Equal(g48,g24)
    c: Equal(g72,g96)
    c: Equal(g52,g28)
    c: Equal(g52,g76)
    c: Equal(g76,g100)
    c: Equal(g25,g49)
    c: Equal(g49,g73)
    c: Equal(g73,g97)
    c: DistanceY(g37,g61) = 0
    c: DistanceY(g61,g85) = 0
    c: DistanceY(g85,g109) = 0
    c: Equal(g29,g53)
    c: Equal(g53,g77)
    c: Equal(g77,g101)
    c: Equal(g56,g32)
    c: Equal(g56,g80)
    c: Equal(g80,g104)
    c: DistanceY(g29,g53) = 0
    c: DistanceY(g53,g77) = 0
    c: DistanceY(g77,g101) = 0
    c: Equal(g38,g62)
    c: Equal(g62,g86)
    c: Equal(g86,g110)
    c: DistanceY(g86,g110) = 0
    c: DistanceY(g62,g86) = 0
    c: DistanceY(g38,g62) = 0
    c: Equal(g66,g42)
    c: Equal(g90,g66)
    c: Equal(g114,g90)
    c: Equal(g39,g63)
    c: Equal(g87,g63)
    c: Equal(g111,g87)
    c: DistanceY(g87,g111) = 0
    c: DistanceY(g63,g87) = 0
    c: DistanceY(g39,g63) = 0
    c: DistanceY(g43,g67) = 0
    c: DistanceY(g91,g115) = 0
    c: DistanceY(g67,g91) = 0
    c: DistanceY(g92,g116) = 0
    c: DistanceY(g68,g92) = 0
    c: DistanceY(g44,g68) = 0
FEATURE [Sketcher::SketchObject] Sketch003  label="masterfader"
  ExternalGeometry = -> [Pad]
  FullyConstrained = true
  MapMode = 5
  Placement = pos=(0,0,1.5) rot=(0,0,1;0rad)
  Support = -> [Pad]
  sketch-geometry (10):
    g0: LineSegment StartX=304 StartY=-135 StartZ=0 EndX=290 EndY=-135 EndZ=0
    g1: LineSegment StartX=290 StartY=-135 StartZ=0 EndX=290 EndY=-121 EndZ=0
    g2: LineSegment StartX=290 StartY=-121 StartZ=0 EndX=304 EndY=-121 EndZ=0
    g3: LineSegment StartX=304 StartY=-121 StartZ=0 EndX=304 EndY=-135 EndZ=0
    g4: Circle CenterX=296 CenterY=-105 CenterZ=0 NormalX=0 NormalY=0 NormalZ=1 AngleXU=0 Radius=1.5
    g5: Circle CenterX=296 CenterY=15 CenterZ=0 NormalX=0 NormalY=0 NormalZ=1 AngleXU=0 Radius=1.5
    g6: LineSegment StartX=295 StartY=9 StartZ=0 EndX=297 EndY=9 EndZ=0
    g7: LineSegment StartX=297 StartY=9 StartZ=0 EndX=297 EndY=-99 EndZ=0
    g8: LineSegment StartX=297 StartY=-99 StartZ=0 EndX=295 EndY=-99 EndZ=0
    g9: LineSegment StartX=295 StartY=-99 StartZ=0 EndX=295 EndY=9 EndZ=0
  constraints (30):
    c: Coincident(g0,g1)
    c: Coincident(g1,g2)
    c: Coincident(g2,g3)
    c: Coincident(g3,g0)
    c: Horizontal(g0)
    c: Horizontal(g2)
    c: Vertical(g1)
    c: Vertical(g3)
    c: Coincident(g6,g7)
    c: Coincident(g7,g8)
    c: Coincident(g8,g9)
    c: Coincident(g9,g6)
    c: Horizontal(g6)
    c: Horizontal(g8)
    c: Vertical(g7)
    c: Vertical(g9)
    c: Diameter(g4) = 3
    c: Equal(g4,g5)
    c: DistanceX(g6,g6) = 2
    c: DistanceY(g9,g9) = 108
    c: DistanceY(g1,g1) = 14
    c: DistanceX(g2,g2) = 14
    c: DistanceX(g1,g4) = 6
    c: DistanceX(g8,g4) = 1
    c: DistanceX(g6,g5) = 1
    c: DistanceY(g6,g5) = 6
    c: DistanceY(g4,g8) = 6
    c: DistanceY(g1,g4) = 16
    c: DistanceX(g0,g-4) = 11
    c: DistanceY(g-4,g0) = 10
FEATURE [Sketcher::SketchObject] Sketch004  label="keypad"
  ExternalGeometry = -> [Pad]
  FullyConstrained = true
  MapMode = 5
  Placement = pos=(0,0,1.5) rot=(0,0,1;0rad)
  Support = -> [Pad]
  sketch-geometry (105):
    g0: LineSegment StartX=204 StartY=-61 StartZ=0 EndX=190 EndY=-61 EndZ=0
    g1: LineSegment StartX=190 StartY=-61 StartZ=0 EndX=190 EndY=-75 EndZ=0
    g2: LineSegment StartX=190 StartY=-75 StartZ=0 EndX=204 EndY=-75 EndZ=0
    g3: LineSegment StartX=204 StartY=-75 StartZ=0 EndX=204 EndY=-61 EndZ=0
    g4: LineSegment StartX=224 StartY=-61 StartZ=0 EndX=210 EndY=-61 EndZ=0
    g5: LineSegment StartX=210 StartY=-61 StartZ=0 EndX=210 EndY=-75 EndZ=0
    g6: LineSegment StartX=210 StartY=-75 StartZ=0 EndX=224 EndY=-75 EndZ=0
    g7: LineSegment StartX=224 StartY=-75 StartZ=0 EndX=224 EndY=-61 EndZ=0
    g8: LineSegment StartX=204 StartY=-61 StartZ=0 EndX=224 EndY=-61 EndZ=0
    g9: LineSegment StartX=244 StartY=-61 StartZ=0 EndX=230 EndY=-61 EndZ=0
    g10: LineSegment StartX=230 StartY=-61 StartZ=0 EndX=230 EndY=-75 EndZ=0
    g11: LineSegment StartX=230 StartY=-75 StartZ=0 EndX=244 EndY=-75 EndZ=0
    g12: LineSegment StartX=244 StartY=-75 StartZ=0 EndX=244 EndY=-61 EndZ=0
    g13: LineSegment StartX=224 StartY=-61 StartZ=0 EndX=244 EndY=-61 EndZ=0
    g14: LineSegment StartX=264 StartY=-61 StartZ=0 EndX=250 EndY=-61 EndZ=0
    g15: LineSegment StartX=250 StartY=-61 StartZ=0 EndX=250 EndY=-75 EndZ=0
    g16: LineSegment StartX=250 StartY=-75 StartZ=0 EndX=264 EndY=-75 EndZ=0
    g17: LineSegment StartX=264 StartY=-75 StartZ=0 EndX=264 EndY=-61 EndZ=0
    g18: LineSegment StartX=244 StartY=-61 StartZ=0 EndX=264 EndY=-61 EndZ=0
    g19: LineSegment StartX=204 StartY=-81 StartZ=0 EndX=190 EndY=-81 EndZ=0
    g20: LineSegment StartX=190 StartY=-81 StartZ=0 EndX=190 EndY=-95 EndZ=0
    g21: LineSegment StartX=190 StartY=-95 StartZ=0 EndX=204 EndY=-95 EndZ=0
    g22: LineSegment StartX=204 StartY=-95 StartZ=0 EndX=204 EndY=-81 EndZ=0
    g23: LineSegment StartX=204 StartY=-61 StartZ=0 EndX=204 EndY=-81 EndZ=0
    g24: LineSegment StartX=224 StartY=-81 StartZ=0 EndX=210 EndY=-81 EndZ=0
    g25: LineSegment StartX=210 StartY=-81 StartZ=0 EndX=210 EndY=-95 EndZ=0
    g26: LineSegment StartX=210 StartY=-95 StartZ=0 EndX=224 EndY=-95 EndZ=0
    g27: LineSegment StartX=224 StartY=-95 StartZ=0 EndX=224 EndY=-81 EndZ=0
    g28: LineSegment StartX=204 StartY=-81 StartZ=0 EndX=224 EndY=-81 EndZ=0
    g29: LineSegment StartX=244 StartY=-81 StartZ=0 EndX=230 EndY=-81 EndZ=0
    g30: LineSegment StartX=230 StartY=-81 StartZ=0 EndX=230 EndY=-95 EndZ=0
    g31: LineSegment StartX=230 StartY=-95 StartZ=0 EndX=244 EndY=-95 EndZ=0
    g32: LineSegment StartX=244 StartY=-95 StartZ=0 EndX=244 EndY=-81 EndZ=0
    g33: LineSegment StartX=224 StartY=-81 StartZ=0 EndX=244 EndY=-81 EndZ=0
    g34: LineSegment StartX=264 StartY=-81 StartZ=0 EndX=250 EndY=-81 EndZ=0
    g35: LineSegment StartX=250 StartY=-81 StartZ=0 EndX=250 EndY=-95 EndZ=0
    g36: LineSegment StartX=250 StartY=-95 StartZ=0 EndX=264 EndY=-95 EndZ=0
    g37: LineSegment StartX=264 StartY=-95 StartZ=0 EndX=264 EndY=-81 EndZ=0
    g38: LineSegment StartX=244 StartY=-81 StartZ=0 EndX=264 EndY=-81 EndZ=0
    g39: LineSegment StartX=204 StartY=-101 StartZ=0 EndX=190 EndY=-101 EndZ=0
    g40: LineSegment StartX=190 StartY=-101 StartZ=0 EndX=190 EndY=-115 EndZ=0
    g41: LineSegment StartX=190 StartY=-115 StartZ=0 EndX=204 EndY=-115 EndZ=0
    g42: LineSegment StartX=204 StartY=-115 StartZ=0 EndX=204 EndY=-101 EndZ=0
    g43: LineSegment StartX=204 StartY=-81 StartZ=0 EndX=204 EndY=-101 EndZ=0
    g44: LineSegment StartX=224 StartY=-101 StartZ=0 EndX=210 EndY=-101 EndZ=0
    g45: LineSegment StartX=210 StartY=-101 StartZ=0 EndX=210 EndY=-115 EndZ=0
    g46: LineSegment StartX=210 StartY=-115 StartZ=0 EndX=224 EndY=-115 EndZ=0
    g47: LineSegment StartX=224 StartY=-115 StartZ=0 EndX=224 EndY=-101 EndZ=0
    g48: LineSegment StartX=204 StartY=-101 StartZ=0 EndX=224 EndY=-101 EndZ=0
    g49: LineSegment StartX=244 StartY=-101 StartZ=0 EndX=230 EndY=-101 EndZ=0
    g50: LineSegment StartX=230 StartY=-101 StartZ=0 EndX=230 EndY=-115 EndZ=0
    g51: LineSegment StartX=230 StartY=-115 StartZ=0 EndX=244 EndY=-115 EndZ=0
    g52: LineSegment StartX=244 StartY=-115 StartZ=0 EndX=244 EndY=-101 EndZ=0
    g53: LineSegment StartX=224 StartY=-101 StartZ=0 EndX=244 EndY=-101 EndZ=0
    g54: LineSegment StartX=204 StartY=-121 StartZ=0 EndX=190 EndY=-121 EndZ=0
    g55: LineSegment StartX=190 StartY=-121 StartZ=0 EndX=190 EndY=-135 EndZ=0
    g56: LineSegment StartX=190 StartY=-135 StartZ=0 EndX=204 EndY=-135 EndZ=0
    g57: LineSegment StartX=204 StartY=-135 StartZ=0 EndX=204 EndY=-121 EndZ=0
    g58: LineSegment StartX=204 StartY=-101 StartZ=0 EndX=204 EndY=-121 EndZ=0
    g59: LineSegment StartX=224 StartY=-121 StartZ=0 EndX=210 EndY=-121 EndZ=0
    g60: LineSegment StartX=210 StartY=-121 StartZ=0 EndX=210 EndY=-135 EndZ=0
    g61: LineSegment StartX=210 StartY=-135 StartZ=0 EndX=224 EndY=-135 EndZ=0
    g62: LineSegment StartX=224 StartY=-135 StartZ=0 EndX=224 EndY=-121 EndZ=0
    g63: LineSegment StartX=204 StartY=-121 StartZ=0 EndX=224 EndY=-121 EndZ=0
    g64: LineSegment StartX=244 StartY=-121 StartZ=0 EndX=230 EndY=-121 EndZ=0
    g65: LineSegment StartX=230 StartY=-121 StartZ=0 EndX=230 EndY=-135 EndZ=0
    g66: LineSegment StartX=230 StartY=-135 StartZ=0 EndX=244 EndY=-135 EndZ=0
    g67: LineSegment StartX=244 StartY=-135 StartZ=0 EndX=244 EndY=-121 EndZ=0
    g68: LineSegment StartX=224 StartY=-121 StartZ=0 EndX=244 EndY=-121 EndZ=0
    g69: LineSegment StartX=250 StartY=-125 StartZ=0 EndX=250 EndY=-111 EndZ=0
    g70: LineSegment StartX=250 StartY=-111 StartZ=0 EndX=254.7 EndY=-111 EndZ=0
    g71: LineSegment StartX=254.7 StartY=-111 StartZ=0 EndX=254.7 EndY=-109.475 EndZ=0
    g72: LineSegment StartX=254.7 StartY=-109.475 StartZ=0 EndX=251.47 EndY=-109.475 EndZ=0
    g73: LineSegment StartX=251.47 StartY=-109.475 StartZ=0 EndX=251.47 EndY=-102.725 EndZ=0
    g74: LineSegment StartX=251.47 StartY=-102.725 StartZ=0 EndX=254.7 EndY=-102.725 EndZ=0
    g75: LineSegment StartX=254.7 StartY=-102.725 StartZ=0 EndX=254.7 EndY=-101.9 EndZ=0
    g76: LineSegment StartX=254.7 StartY=-101.9 StartZ=0 EndX=257.485 EndY=-101.9 EndZ=0
    g77: LineSegment StartX=257.485 StartY=-101.9 StartZ=0 EndX=257.485 EndY=-102.725 EndZ=0
    g78: LineSegment StartX=257.485 StartY=-102.725 StartZ=0 EndX=263.77 EndY=-102.725 EndZ=0
    g79: LineSegment StartX=263.77 StartY=-102.725 StartZ=0 EndX=263.77 EndY=-104.45 EndZ=0
    g80: LineSegment StartX=263.77 StartY=-104.45 StartZ=0 EndX=265.495 EndY=-104.45 EndZ=0
    g81: LineSegment StartX=265.495 StartY=-104.45 StartZ=0 EndX=265.495 EndY=-107.75 EndZ=0
    g82: LineSegment StartX=265.495 StartY=-107.75 StartZ=0 EndX=263.77 EndY=-107.75 EndZ=0
    g83: LineSegment StartX=263.77 StartY=-107.75 StartZ=0 EndX=263.77 EndY=-109.475 EndZ=0
    g84: LineSegment StartX=263.77 StartY=-109.475 StartZ=0 EndX=259.07 EndY=-109.475 EndZ=0
    g85: LineSegment StartX=259.07 StartY=-109.475 StartZ=0 EndX=259.07 EndY=-111 EndZ=0
    g86: LineSegment StartX=259.07 StartY=-111 StartZ=0 EndX=263.77 EndY=-111 EndZ=0
    g87: LineSegment StartX=263.77 StartY=-111 StartZ=0 EndX=263.77 EndY=-125 EndZ=0
    g88: LineSegment StartX=250 StartY=-125 StartZ=0 EndX=254.7 EndY=-125 EndZ=0
    g89: LineSegment StartX=254.7 StartY=-125 StartZ=0 EndX=254.7 EndY=-126.525 EndZ=0
    g90: LineSegment StartX=254.7 StartY=-126.525 StartZ=0 EndX=251.47 EndY=-126.525 EndZ=0
    g91: LineSegment StartX=251.47 StartY=-126.525 StartZ=0 EndX=251.47 EndY=-133.275 EndZ=0
    g92: LineSegment StartX=251.47 StartY=-133.275 StartZ=0 EndX=254.7 EndY=-133.275 EndZ=0
    g93: LineSegment StartX=254.7 StartY=-133.275 StartZ=0 EndX=254.7 EndY=-134.1 EndZ=0
    g94: LineSegment StartX=254.7 StartY=-134.1 StartZ=0 EndX=257.485 EndY=-134.1 EndZ=0
    g95: LineSegment StartX=257.485 StartY=-134.1 StartZ=0 EndX=257.485 EndY=-133.275 EndZ=0
    g96: LineSegment StartX=257.485 StartY=-133.275 StartZ=0 EndX=263.77 EndY=-133.275 EndZ=0
    g97: LineSegment StartX=263.77 StartY=-133.275 StartZ=0 EndX=263.77 EndY=-131.55 EndZ=0
    g98: LineSegment StartX=263.77 StartY=-131.55 StartZ=0 EndX=265.495 EndY=-131.55 EndZ=0
    g99: LineSegment StartX=265.495 StartY=-131.55 StartZ=0 EndX=265.495 EndY=-128.25 EndZ=0
    g100: LineSegment StartX=265.495 StartY=-128.25 StartZ=0 EndX=263.77 EndY=-128.25 EndZ=0
    g101: LineSegment StartX=263.77 StartY=-128.25 StartZ=0 EndX=263.77 EndY=-126.525 EndZ=0
    g102: LineSegment StartX=263.77 StartY=-126.525 StartZ=0 EndX=259.07 EndY=-126.525 EndZ=0
    g103: LineSegment StartX=259.07 StartY=-126.525 StartZ=0 EndX=259.07 EndY=-125 EndZ=0
    g104: LineSegment StartX=259.07 StartY=-125 StartZ=0 EndX=263.77 EndY=-125 EndZ=0
  constraints (302):
    c: Coincident(g0,g1)
    c: Coincident(g1,g2)
    c: Coincident(g2,g3)
    c: Coincident(g3,g0)
    c: Horizontal(g0)
    c: Horizontal(g2)
    c: Vertical(g1)
    c: Vertical(g3)
    c: DistanceY(g1,g1) = 14
    c: DistanceX(g0,g0) = 14
    c: Coincident(g4,g5)
    c: Coincident(g5,g6)
    c: Coincident(g6,g7)
    c: Coincident(g7,g4)
    c: Horizontal(g4)
    c: Horizontal(g6)
    c: Vertical(g5)
    c: Vertical(g7)
    c: Equal(g1,g5) = 14
    c: Equal(g0,g4) = 14
    c: Coincident(g0,g8)
    c: Coincident(g4,g8)
    c: Distance(g8) = 20
    c: Angle(g8) = 0
    c: Coincident(g9,g10)
    c: Coincident(g10,g11)
    c: Coincident(g11,g12)
    c: Coincident(g12,g9)
    c: Horizontal(g9)
    c: Horizontal(g11)
    c: Vertical(g10)
    c: Vertical(g12)
    c: Equal(g1,g10) = 14
    c: Equal(g0,g9) = 14
    c: Coincident(g4,g13)
    c: Coincident(g9,g13)
    c: Equal(g8,g13)
    c: Parallel(g13,g8)
    c: Coincident(g14,g15)
    c: Coincident(g15,g16)
    c: Coincident(g16,g17)
    c: Coincident(g17,g14)
    c: Horizontal(g14)
    c: Horizontal(g16)
    c: Vertical(g15)
    c: Vertical(g17)
    c: Equal(g1,g15) = 14
    c: Equal(g0,g14) = 14
    c: Coincident(g9,g18)
    c: Coincident(g14,g18)
    c: Equal(g8,g18)
    c: Parallel(g18,g8)
    c: Coincident(g19,g20)
    c: Coincident(g20,g21)
    c: Coincident(g21,g22)
    c: Coincident(g22,g19)
    c: Horizontal(g19)
    c: Horizontal(g21)
    c: Vertical(g20)
    c: Vertical(g22)
    c: Equal(g1,g20) = 14
    c: Equal(g0,g19) = 14
    c: Coincident(g0,g23)
    c: Coincident(g19,g23)
    c: Equal(g23,g8)
    c: Perpendicular(g23,g8)
    c: Coincident(g24,g25)
    c: Coincident(g25,g26)
    c: Coincident(g26,g27)
    c: Coincident(g27,g24)
    c: Horizontal(g24)
    c: Horizontal(g26)
    c: Vertical(g25)
    c: Vertical(g27)
    c: Equal(g1,g25) = 14
    c: Equal(g0,g24) = 14
    c: Coincident(g19,g28)
    c: Coincident(g24,g28)
    c: Equal(g8,g28)
    c: Parallel(g28,g8)
    c: Coincident(g29,g30)
    c: Coincident(g30,g31)
    c: Coincident(g31,g32)
    c: Coincident(g32,g29)
    c: Horizontal(g29)
    c: Horizontal(g31)
    c: Vertical(g30)
    c: Vertical(g32)
    c: Equal(g1,g30) = 14
    c: Equal(g0,g29) = 14
    c: Coincident(g24,g33)
    c: Coincident(g29,g33)
    c: Equal(g8,g33)
    c: Parallel(g33,g8)
    c: Coincident(g34,g35)
    c: Coincident(g35,g36)
    c: Coincident(g36,g37)
    c: Coincident(g37,g34)
    c: Horizontal(g34)
    c: Horizontal(g36)
    c: Vertical(g35)
    c: Vertical(g37)
    c: Equal(g1,g35) = 14
    c: Equal(g0,g34) = 14
    c: Coincident(g29,g38)
    c: Coincident(g34,g38)
    c: Equal(g8,g38)
    c: Parallel(g38,g8)
    c: Coincident(g39,g40)
    c: Coincident(g40,g41)
    c: Coincident(g41,g42)
    c: Coincident(g42,g39)
    c: Horizontal(g39)
    c: Horizontal(g41)
    c: Vertical(g40)
    c: Vertical(g42)
    c: Equal(g1,g40) = 14
    c: Equal(g0,g39) = 14
    c: Coincident(g19,g43)
    c: Coincident(g39,g43)
    c: Equal(g23,g43)
    c: Perpendicular(g43,g8)
    c: Coincident(g44,g45)
    c: Coincident(g45,g46)
    c: Coincident(g46,g47)
    c: Coincident(g47,g44)
    c: Horizontal(g44)
    c: Horizontal(g46)
    c: Vertical(g45)
    c: Vertical(g47)
    c: Equal(g1,g45) = 14
    c: Equal(g0,g44) = 14
    c: Coincident(g39,g48)
    c: Coincident(g44,g48)
    c: Equal(g8,g48)
    c: Parallel(g48,g8)
    c: Coincident(g49,g50)
    c: Coincident(g50,g51)
    c: Coincident(g51,g52)
    c: Coincident(g52,g49)
    c: Horizontal(g49)
    c: Horizontal(g51)
    c: Vertical(g50)
    c: Vertical(g52)
    c: Equal(g1,g50) = 14
    c: Equal(g0,g49) = 14
    c: Coincident(g44,g53)
    c: Coincident(g49,g53)
    c: Equal(g8,g53)
    c: Parallel(g53,g8)
    c: Coincident(g54,g55)
    c: Coincident(g55,g56)
    c: Coincident(g56,g57)
    c: Coincident(g57,g54)
    c: Horizontal(g54)
    c: Horizontal(g56)
    c: Vertical(g55)
    c: Vertical(g57)
    c: Equal(g1,g55) = 14
    c: Equal(g0,g54) = 14
    c: Coincident(g39,g58)
    c: Coincident(g54,g58)
    c: Equal(g23,g58)
    c: Perpendicular(g58,g8)
    c: Coincident(g59,g60)
    c: Coincident(g60,g61)
    c: Coincident(g61,g62)
    c: Coincident(g62,g59)
    c: Horizontal(g59)
    c: Horizontal(g61)
    c: Vertical(g60)
    c: Vertical(g62)
    c: Equal(g1,g60) = 14
    c: Equal(g0,g59) = 14
    c: Coincident(g54,g63)
    c: Coincident(g59,g63)
    c: Equal(g8,g63)
    c: Parallel(g63,g8)
    c: Coincident(g64,g65)
    c: Coincident(g65,g66)
    c: Coincident(g66,g67)
    c: Coincident(g67,g64)
    c: Horizontal(g64)
    c: Horizontal(g66)
    c: Vertical(g65)
    c: Vertical(g67)
    c: Equal(g1,g65) = 14
    c: Equal(g0,g64) = 14
    c: Coincident(g59,g68)
    c: Coincident(g64,g68)
    c: Equal(g8,g68)
    c: Parallel(g68,g8)
    c: DistanceY(g-6,g66) = 10
    c: Vertical(g69)
    c: DistanceY(g69,g69) = 14
    c: DistanceY(g51,g69) = 4
    c: Coincident(g70,g69)
    c: Horizontal(g70)
    c: Coincident(g71,g70)
    c: Vertical(g71)
    c: Coincident(g72,g71)
    c: Horizontal(g72)
    c: Coincident(g73,g72)
    c: Vertical(g73)
    c: Coincident(g74,g73)
    c: Horizontal(g74)
    c: Coincident(g75,g74)
    c: Vertical(g75)
    c: Coincident(g76,g75)
    c: Coincident(g77,g76)
    c: Vertical(g77)
    c: Coincident(g78,g77)
    c: Horizontal(g78)
    c: Coincident(g79,g78)
    c: Coincident(g80,g79)
    c: Coincident(g81,g80)
    c: Coincident(g82,g81)
    c: Coincident(g83,g82)
    c: Vertical(g83)
    c: Coincident(g84,g83)
    c: Horizontal(g84)
    c: Coincident(g85,g84)
    c: Vertical(g85)
    c: Coincident(g86,g85)
    c: Horizontal(g86)
    c: Coincident(g87,g86)
    c: Vertical(g87)
    c: Equal(g74,g72)
    c: Equal(g75,g77)
    c: Equal(g83,g79)
    c: Equal(g80,g82)
    c: Parallel(g80,g82)
    c: Perpendicular(g76,g75)
    c: Perpendicular(g79,g80)
    c: Parallel(g81,g79)
    c: Parallel(g83,g79)
    c: Equal(g85,g71)
    c: Equal(g70,g86)
    c: DistanceY(g73,g73) = 6.75
    c: DistanceX(g70,g70) = 4.7
    c: DistanceY(g71,g71) = 1.525
    c: DistanceX(g72,g72) = 3.23
    c: DistanceX(g35,g69) = 0
    c: DistanceY(g75,g75) = 0.825
    c: DistanceX(g76,g76) = 2.785
    c: DistanceX(g78,g78) = 6.285
    c: DistanceY(g79,g79) = 1.725
    c: DistanceX(g80,g80) = 1.725
    c: DistanceY(g81,g81) = 3.3
    c: Equal(g84,g86)
    c: Equal(g87,g69)
    c: Coincident(g88,g69)
    c: Horizontal(g88)
    c: Coincident(g89,g88)
    c: Vertical(g89)
    c: Coincident(g90,g89)
    c: Horizontal(g90)
    c: Coincident(g91,g90)
    c: Vertical(g91)
    c: Coincident(g92,g91)
    c: Horizontal(g92)
    c: Coincident(g93,g92)
    c: Coincident(g94,g93)
    c: Horizontal(g94)
    c: Coincident(g95,g94)
    c: Coincident(g96,g95)
    c: Horizontal(g96)
    c: Coincident(g97,g96)
    c: Vertical(g97)
    c: Coincident(g98,g97)
    c: Coincident(g99,g98)
    c: Coincident(g100,g99)
    c: Coincident(g101,g100)
    c: Coincident(g102,g101)
    c: Horizontal(g102)
    c: Coincident(g103,g102)
    c: Vertical(g103)
    c: Coincident(g104,g103)
    c: Coincident(g104,g87)
    c: Equal(g70,g88)
    c: Equal(g104,g86)
    c: Equal(g103,g89)
    c: Equal(g89,g71)
    c: Perpendicular(g87,g104)
    c: Equal(g90,g72)
    c: Equal(g102,g84)
    c: Equal(g101,g83)
    c: Equal(g100,g82)
    c: Equal(g81,g99)
    c: Equal(g80,g98)
    c: Equal(g97,g79)
    c: Equal(g78,g96)
    c: Equal(g91,g73)
    c: Equal(g92,g74)
    c: Equal(g95,g93)
    c: Equal(g93,g75)
    c: Perpendicular(g102,g101)
    c: Parallel(g98,g100)
    c: Perpendicular(g101,g100)
    c: Perpendicular(g100,g99)
    c: Perpendicular(g95,g96)
    c: DistanceX(g55,g-6) = 125
FEATURE [Sketcher::SketchObject] Sketch005  label="executer0"
  ExternalGeometry = -> [Pad]
  FullyConstrained = true
  MapMode = 5
  Placement = pos=(0,0,1.5) rot=(0,0,1;0rad)
  Support = -> [Pad]
  sketch-geometry (53):
    g0: LineSegment StartX=60 StartY=-111 StartZ=0 EndX=74 EndY=-111 EndZ=0
    g1: LineSegment StartX=74 StartY=-111 StartZ=0 EndX=74 EndY=-125 EndZ=0
    g2: LineSegment StartX=74 StartY=-125 StartZ=0 EndX=60 EndY=-125 EndZ=0
    g3: LineSegment StartX=60 StartY=-125 StartZ=0 EndX=60 EndY=-111 EndZ=0
    g4: LineSegment StartX=60 StartY=-91 StartZ=0 EndX=74 EndY=-91 EndZ=0
    g5: LineSegment StartX=74 StartY=-91 StartZ=0 EndX=74 EndY=-105 EndZ=0
    g6: LineSegment StartX=74 StartY=-105 StartZ=0 EndX=60 EndY=-105 EndZ=0
    g7: LineSegment StartX=60 StartY=-105 StartZ=0 EndX=60 EndY=-91 EndZ=0
    g8: LineSegment StartX=80 StartY=-111 StartZ=0 EndX=94 EndY=-111 EndZ=0
    g9: LineSegment StartX=94 StartY=-111 StartZ=0 EndX=94 EndY=-125 EndZ=0
    g10: LineSegment StartX=94 StartY=-125 StartZ=0 EndX=80 EndY=-125 EndZ=0
    g11: LineSegment StartX=80 StartY=-125 StartZ=0 EndX=80 EndY=-111 EndZ=0
    g12: LineSegment StartX=80 StartY=-91 StartZ=0 EndX=94 EndY=-91 EndZ=0
    g13: LineSegment StartX=94 StartY=-91 StartZ=0 EndX=94 EndY=-105 EndZ=0
    g14: LineSegment StartX=94 StartY=-105 StartZ=0 EndX=80 EndY=-105 EndZ=0
    g15: LineSegment StartX=80 StartY=-105 StartZ=0 EndX=80 EndY=-91 EndZ=0
    g16: LineSegment StartX=60 StartY=-111 StartZ=0 EndX=80 EndY=-111 EndZ=0
    g17: LineSegment StartX=100 StartY=-111 StartZ=0 EndX=114 EndY=-111 EndZ=0
    g18: LineSegment StartX=114 StartY=-111 StartZ=0 EndX=114 EndY=-125 EndZ=0
    g19: LineSegment StartX=114 StartY=-125 StartZ=0 EndX=100 EndY=-125 EndZ=0
    g20: LineSegment StartX=100 StartY=-125 StartZ=0 EndX=100 EndY=-111 EndZ=0
    g21: LineSegment StartX=100 StartY=-91 StartZ=0 EndX=114 EndY=-91 EndZ=0
    g22: LineSegment StartX=114 StartY=-91 StartZ=0 EndX=114 EndY=-105 EndZ=0
    g23: LineSegment StartX=114 StartY=-105 StartZ=0 EndX=100 EndY=-105 EndZ=0
    g24: LineSegment StartX=100 StartY=-105 StartZ=0 EndX=100 EndY=-91 EndZ=0
    g25: LineSegment StartX=80 StartY=-111 StartZ=0 EndX=100 EndY=-111 EndZ=0
    g26: LineSegment StartX=120 StartY=-111 StartZ=0 EndX=134 EndY=-111 EndZ=0
    g27: LineSegment StartX=134 StartY=-111 StartZ=0 EndX=134 EndY=-125 EndZ=0
    g28: LineSegment StartX=134 StartY=-125 StartZ=0 EndX=120 EndY=-125 EndZ=0
    g29: LineSegment StartX=120 StartY=-125 StartZ=0 EndX=120 EndY=-111 EndZ=0
    g30: LineSegment StartX=120 StartY=-91 StartZ=0 EndX=134 EndY=-91 EndZ=0
    g31: LineSegment StartX=134 StartY=-91 StartZ=0 EndX=134 EndY=-105 EndZ=0
    g32: LineSegment StartX=134 StartY=-105 StartZ=0 EndX=120 EndY=-105 EndZ=0
    g33: LineSegment StartX=120 StartY=-105 StartZ=0 EndX=120 EndY=-91 EndZ=0
    g34: LineSegment StartX=100 StartY=-111 StartZ=0 EndX=120 EndY=-111 EndZ=0
    g35: LineSegment StartX=140 StartY=-111 StartZ=0 EndX=154 EndY=-111 EndZ=0
    g36: LineSegment StartX=154 StartY=-111 StartZ=0 EndX=154 EndY=-125 EndZ=0
    g37: LineSegment StartX=154 StartY=-125 StartZ=0 EndX=140 EndY=-125 EndZ=0
    g38: LineSegment StartX=140 StartY=-125 StartZ=0 EndX=140 EndY=-111 EndZ=0
    g39: LineSegment StartX=140 StartY=-91 StartZ=0 EndX=154 EndY=-91 EndZ=0
    g40: LineSegment StartX=154 StartY=-91 StartZ=0 EndX=154 EndY=-105 EndZ=0
    g41: LineSegment StartX=154 StartY=-105 StartZ=0 EndX=140 EndY=-105 EndZ=0
    g42: LineSegment StartX=140 StartY=-105 StartZ=0 EndX=140 EndY=-91 EndZ=0
    g43: LineSegment StartX=120 StartY=-111 StartZ=0 EndX=140 EndY=-111 EndZ=0
    g44: LineSegment StartX=160 StartY=-111 StartZ=0 EndX=174 EndY=-111 EndZ=0
    g45: LineSegment StartX=174 StartY=-111 StartZ=0 EndX=174 EndY=-125 EndZ=0
    g46: LineSegment StartX=174 StartY=-125 StartZ=0 EndX=160 EndY=-125 EndZ=0
    g47: LineSegment StartX=160 StartY=-125 StartZ=0 EndX=160 EndY=-111 EndZ=0
    g48: LineSegment StartX=160 StartY=-91 StartZ=0 EndX=174 EndY=-91 EndZ=0
    g49: LineSegment StartX=174 StartY=-91 StartZ=0 EndX=174 EndY=-105 EndZ=0
    g50: LineSegment StartX=174 StartY=-105 StartZ=0 EndX=160 EndY=-105 EndZ=0
    g51: LineSegment StartX=160 StartY=-105 StartZ=0 EndX=160 EndY=-91 EndZ=0
    g52: LineSegment StartX=140 StartY=-111 StartZ=0 EndX=160 EndY=-111 EndZ=0
  constraints (154):
    c: Coincident(g0,g1)
    c: Coincident(g1,g2)
    c: Coincident(g2,g3)
    c: Coincident(g3,g0)
    c: Horizontal(g0)
    c: Horizontal(g2)
    c: Vertical(g1)
    c: Vertical(g3)
    c: DistanceY(g3,g3) = 14
    c: DistanceX(g0,g0) = 14
    c: Coincident(g4,g5)
    c: Coincident(g5,g6)
    c: Coincident(g6,g7)
    c: Coincident(g7,g4)
    c: Horizontal(g4)
    c: Horizontal(g6)
    c: Vertical(g5)
    c: Vertical(g7)
    c: Equal(g3,g7) = 14
    c: Equal(g0,g4) = 14
    c: DistanceY(g0,g6) = 6
    c: DistanceX(g0,g6) = 0
    c: Coincident(g8,g9)
    c: Coincident(g9,g10)
    c: Coincident(g10,g11)
    c: Coincident(g11,g8)
    c: Horizontal(g8)
    c: Horizontal(g10)
    c: Vertical(g9)
    c: Vertical(g11)
    c: Equal(g3,g11) = 14
    c: Equal(g0,g8) = 14
    c: Coincident(g12,g13)
    c: Coincident(g13,g14)
    c: Coincident(g14,g15)
    c: Coincident(g15,g12)
    c: Horizontal(g12)
    c: Horizontal(g14)
    c: Vertical(g13)
    c: Vertical(g15)
    c: Equal(g11,g15) = 14
    c: Equal(g8,g12) = 14
    c: DistanceY(g8,g14) = 6
    c: DistanceX(g8,g14) = 0
    c: Coincident(g0,g16)
    c: Coincident(g8,g16)
    c: Distance(g16) = 20
    c: Angle(g16) = 0
    c: Coincident(g17,g18)
    c: Coincident(g18,g19)
    c: Coincident(g19,g20)
    c: Coincident(g20,g17)
    c: Horizontal(g17)
    c: Horizontal(g19)
    c: Vertical(g18)
    c: Vertical(g20)
    c: Equal(g3,g20) = 14
    c: Equal(g0,g17) = 14
    c: Coincident(g21,g22)
    c: Coincident(g22,g23)
    c: Coincident(g23,g24)
    c: Coincident(g24,g21)
    c: Horizontal(g21)
    c: Horizontal(g23)
    c: Vertical(g22)
    c: Vertical(g24)
    c: Equal(g20,g24) = 14
    c: Equal(g17,g21) = 14
    c: DistanceY(g17,g23) = 6
    c: DistanceX(g17,g23) = 0
    c: Coincident(g8,g25)
    c: Coincident(g17,g25)
    c: Equal(g16,g25)
    c: Parallel(g25,g16)
    c: Coincident(g26,g27)
    c: Coincident(g27,g28)
    c: Coincident(g28,g29)
    c: Coincident(g29,g26)
    c: Horizontal(g26)
    c: Horizontal(g28)
    c: Vertical(g27)
    c: Vertical(g29)
    c: Equal(g3,g29) = 14
    c: Equal(g0,g26) = 14
    c: Coincident(g30,g31)
    c: Coincident(g31,g32)
    c: Coincident(g32,g33)
    c: Coincident(g33,g30)
    c: Horizontal(g30)
    c: Horizontal(g32)
    c: Vertical(g31)
    c: Vertical(g33)
    c: Equal(g29,g33) = 14
    c: Equal(g26,g30) = 14
    c: DistanceY(g26,g32) = 6
    c: DistanceX(g26,g32) = 0
    c: Coincident(g17,g34)
    c: Coincident(g26,g34)
    c: Equal(g16,g34)
    c: Parallel(g34,g16)
    c: Coincident(g35,g36)
    c: Coincident(g36,g37)
    c: Coincident(g37,g38)
    c: Coincident(g38,g35)
    c: Horizontal(g35)
    c: Horizontal(g37)
    c: Vertical(g36)
    c: Vertical(g38)
    c: Equal(g3,g38) = 14
    c: Equal(g0,g35) = 14
    c: Coincident(g39,g40)
    c: Coincident(g40,g41)
    c: Coincident(g41,g42)
    c: Coincident(g42,g39)
    c: Horizontal(g39)
    c: Horizontal(g41)
    c: Vertical(g40)
    c: Vertical(g42)
    c: Equal(g38,g42) = 14
    c: Equal(g35,g39) = 14
    c: DistanceY(g35,g41) = 6
    c: DistanceX(g35,g41) = 0
    c: Coincident(g26,g43)
    c: Coincident(g35,g43)
    c: Equal(g16,g43)
    c: Parallel(g43,g16)
    c: Coincident(g44,g45)
    c: Coincident(g45,g46)
    c: Coincident(g46,g47)
    c: Coincident(g47,g44)
    c: Horizontal(g44)
    c: Horizontal(g46)
    c: Vertical(g45)
    c: Vertical(g47)
    c: Equal(g3,g47) = 14
    c: Equal(g0,g44) = 14
    c: Coincident(g48,g49)
    c: Coincident(g49,g50)
    c: Coincident(g50,g51)
    c: Coincident(g51,g48)
    c: Horizontal(g48)
    c: Horizontal(g50)
    c: Vertical(g49)
    c: Vertical(g51)
    c: Equal(g47,g51) = 14
    c: Equal(g44,g48) = 14
    c: DistanceY(g44,g50) = 6
    c: DistanceX(g44,g50) = 0
    c: Coincident(g35,g52)
    c: Coincident(g44,g52)
    c: Equal(g16,g52)
    c: Parallel(g52,g16)
    c: DistanceX(g-6,g2) = 375
    c: DistanceY(g-6,g2) = 20
FEATURE [Sketcher::SketchObject] Sketch006  label="executer1"
  ExternalGeometry = -> [Pad]
  FullyConstrained = true
  MapMode = 5
  Placement = pos=(0,0,1.5) rot=(0,0,1;0rad)
  Support = -> [Pad]
  sketch-geometry (53):
    g0: LineSegment StartX=60 StartY=-41 StartZ=0 EndX=74 EndY=-41 EndZ=0
    g1: LineSegment StartX=74 StartY=-41 StartZ=0 EndX=74 EndY=-55 EndZ=0
    g2: LineSegment StartX=74 StartY=-55 StartZ=0 EndX=60 EndY=-55 EndZ=0
    g3: LineSegment StartX=60 StartY=-55 StartZ=0 EndX=60 EndY=-41 EndZ=0
    g4: LineSegment StartX=60 StartY=-21 StartZ=0 EndX=74 EndY=-21 EndZ=0
    g5: LineSegment StartX=74 StartY=-21 StartZ=0 EndX=74 EndY=-35 EndZ=0
    g6: LineSegment StartX=74 StartY=-35 StartZ=0 EndX=60 EndY=-35 EndZ=0
    g7: LineSegment StartX=60 StartY=-35 StartZ=0 EndX=60 EndY=-21 EndZ=0
    g8: LineSegment StartX=80 StartY=-41 StartZ=0 EndX=94 EndY=-41 EndZ=0
    g9: LineSegment StartX=94 StartY=-41 StartZ=0 EndX=94 EndY=-55 EndZ=0
    g10: LineSegment StartX=94 StartY=-55 StartZ=0 EndX=80 EndY=-55 EndZ=0
    g11: LineSegment StartX=80 StartY=-55 StartZ=0 EndX=80 EndY=-41 EndZ=0
    g12: LineSegment StartX=80 StartY=-21 StartZ=0 EndX=94 EndY=-21 EndZ=0
    g13: LineSegment StartX=94 StartY=-21 StartZ=0 EndX=94 EndY=-35 EndZ=0
    g14: LineSegment StartX=94 StartY=-35 StartZ=0 EndX=80 EndY=-35 EndZ=0
    g15: LineSegment StartX=80 StartY=-35 StartZ=0 EndX=80 EndY=-21 EndZ=0
    g16: LineSegment StartX=60 StartY=-41 StartZ=0 EndX=80 EndY=-41 EndZ=0
    g17: LineSegment StartX=100 StartY=-41 StartZ=0 EndX=114 EndY=-41 EndZ=0
    g18: LineSegment StartX=114 StartY=-41 StartZ=0 EndX=114 EndY=-55 EndZ=0
    g19: LineSegment StartX=114 StartY=-55 StartZ=0 EndX=100 EndY=-55 EndZ=0
    g20: LineSegment StartX=100 StartY=-55 StartZ=0 EndX=100 EndY=-41 EndZ=0
    g21: LineSegment StartX=100 StartY=-21 StartZ=0 EndX=114 EndY=-21 EndZ=0
    g22: LineSegment StartX=114 StartY=-21 StartZ=0 EndX=114 EndY=-35 EndZ=0
    g23: LineSegment StartX=114 StartY=-35 StartZ=0 EndX=100 EndY=-35 EndZ=0
    g24: LineSegment StartX=100 StartY=-35 StartZ=0 EndX=100 EndY=-21 EndZ=0
    g25: LineSegment StartX=80 StartY=-41 StartZ=0 EndX=100 EndY=-41 EndZ=0
    g26: LineSegment StartX=120 StartY=-41 StartZ=0 EndX=134 EndY=-41 EndZ=0
    g27: LineSegment StartX=134 StartY=-41 StartZ=0 EndX=134 EndY=-55 EndZ=0
    g28: LineSegment StartX=134 StartY=-55 StartZ=0 EndX=120 EndY=-55 EndZ=0
    g29: LineSegment StartX=120 StartY=-55 StartZ=0 EndX=120 EndY=-41 EndZ=0
    g30: LineSegment StartX=120 StartY=-21 StartZ=0 EndX=134 EndY=-21 EndZ=0
    g31: LineSegment StartX=134 StartY=-21 StartZ=0 EndX=134 EndY=-35 EndZ=0
    g32: LineSegment StartX=134 StartY=-35 StartZ=0 EndX=120 EndY=-35 EndZ=0
    g33: LineSegment StartX=120 StartY=-35 StartZ=0 EndX=120 EndY=-21 EndZ=0
    g34: LineSegment StartX=100 StartY=-41 StartZ=0 EndX=120 EndY=-41 EndZ=0
    g35: LineSegment StartX=140 StartY=-41 StartZ=0 EndX=154 EndY=-41 EndZ=0
    g36: LineSegment StartX=154 StartY=-41 StartZ=0 EndX=154 EndY=-55 EndZ=0
    g37: LineSegment StartX=154 StartY=-55 StartZ=0 EndX=140 EndY=-55 EndZ=0
    g38: LineSegment StartX=140 StartY=-55 StartZ=0 EndX=140 EndY=-41 EndZ=0
    g39: LineSegment StartX=140 StartY=-21 StartZ=0 EndX=154 EndY=-21 EndZ=0
    g40: LineSegment StartX=154 StartY=-21 StartZ=0 EndX=154 EndY=-35 EndZ=0
    g41: LineSegment StartX=154 StartY=-35 StartZ=0 EndX=140 EndY=-35 EndZ=0
    g42: LineSegment StartX=140 StartY=-35 StartZ=0 EndX=140 EndY=-21 EndZ=0
    g43: LineSegment StartX=120 StartY=-41 StartZ=0 EndX=140 EndY=-41 EndZ=0
    g44: LineSegment StartX=160 StartY=-41 StartZ=0 EndX=174 EndY=-41 EndZ=0
    g45: LineSegment StartX=174 StartY=-41 StartZ=0 EndX=174 EndY=-55 EndZ=0
    g46: LineSegment StartX=174 StartY=-55 StartZ=0 EndX=160 EndY=-55 EndZ=0
    g47: LineSegment StartX=160 StartY=-55 StartZ=0 EndX=160 EndY=-41 EndZ=0
    g48: LineSegment StartX=160 StartY=-21 StartZ=0 EndX=174 EndY=-21 EndZ=0
    g49: LineSegment StartX=174 StartY=-21 StartZ=0 EndX=174 EndY=-35 EndZ=0
    g50: LineSegment StartX=174 StartY=-35 StartZ=0 EndX=160 EndY=-35 EndZ=0
    g51: LineSegment StartX=160 StartY=-35 StartZ=0 EndX=160 EndY=-21 EndZ=0
    g52: LineSegment StartX=140 StartY=-41 StartZ=0 EndX=160 EndY=-41 EndZ=0
  constraints (154):
    c: Coincident(g0,g1)
    c: Coincident(g1,g2)
    c: Coincident(g2,g3)
    c: Coincident(g3,g0)
    c: Horizontal(g0)
    c: Horizontal(g2)
    c: Vertical(g1)
    c: Vertical(g3)
    c: DistanceY(g3,g3) = 14
    c: DistanceX(g0,g0) = 14
    c: Coincident(g4,g5)
    c: Coincident(g5,g6)
    c: Coincident(g6,g7)
    c: Coincident(g7,g4)
    c: Horizontal(g4)
    c: Horizontal(g6)
    c: Vertical(g5)
    c: Vertical(g7)
    c: Equal(g3,g7) = 14
    c: Equal(g0,g4) = 14
    c: DistanceY(g0,g6) = 6
    c: DistanceX(g0,g6) = 0
    c: Coincident(g8,g9)
    c: Coincident(g9,g10)
    c: Coincident(g10,g11)
    c: Coincident(g11,g8)
    c: Horizontal(g8)
    c: Horizontal(g10)
    c: Vertical(g9)
    c: Vertical(g11)
    c: Equal(g3,g11) = 14
    c: Equal(g0,g8) = 14
    c: Coincident(g12,g13)
    c: Coincident(g13,g14)
    c: Coincident(g14,g15)
    c: Coincident(g15,g12)
    c: Horizontal(g12)
    c: Horizontal(g14)
    c: Vertical(g13)
    c: Vertical(g15)
    c: Equal(g11,g15) = 14
    c: Equal(g8,g12) = 14
    c: DistanceY(g8,g14) = 6
    c: DistanceX(g8,g14) = 0
    c: Coincident(g0,g16)
    c: Coincident(g8,g16)
    c: Distance(g16) = 20
    c: Angle(g16) = 0
    c: Coincident(g17,g18)
    c: Coincident(g18,g19)
    c: Coincident(g19,g20)
    c: Coincident(g20,g17)
    c: Horizontal(g17)
    c: Horizontal(g19)
    c: Vertical(g18)
    c: Vertical(g20)
    c: Equal(g3,g20) = 14
    c: Equal(g0,g17) = 14
    c: Coincident(g21,g22)
    c: Coincident(g22,g23)
    c: Coincident(g23,g24)
    c: Coincident(g24,g21)
    c: Horizontal(g21)
    c: Horizontal(g23)
    c: Vertical(g22)
    c: Vertical(g24)
    c: Equal(g20,g24) = 14
    c: Equal(g17,g21) = 14
    c: DistanceY(g17,g23) = 6
    c: DistanceX(g17,g23) = 0
    c: Coincident(g8,g25)
    c: Coincident(g17,g25)
    c: Equal(g16,g25)
    c: Parallel(g25,g16)
    c: Coincident(g26,g27)
    c: Coincident(g27,g28)
    c: Coincident(g28,g29)
    c: Coincident(g29,g26)
    c: Horizontal(g26)
    c: Horizontal(g28)
    c: Vertical(g27)
    c: Vertical(g29)
    c: Equal(g3,g29) = 14
    c: Equal(g0,g26) = 14
    c: Coincident(g30,g31)
    c: Coincident(g31,g32)
    c: Coincident(g32,g33)
    c: Coincident(g33,g30)
    c: Horizontal(g30)
    c: Horizontal(g32)
    c: Vertical(g31)
    c: Vertical(g33)
    c: Equal(g29,g33) = 14
    c: Equal(g26,g30) = 14
    c: DistanceY(g26,g32) = 6
    c: DistanceX(g26,g32) = 0
    c: Coincident(g17,g34)
    c: Coincident(g26,g34)
    c: Equal(g16,g34)
    c: Parallel(g34,g16)
    c: Coincident(g35,g36)
    c: Coincident(g36,g37)
    c: Coincident(g37,g38)
    c: Coincident(g38,g35)
    c: Horizontal(g35)
    c: Horizontal(g37)
    c: Vertical(g36)
    c: Vertical(g38)
    c: Equal(g3,g38) = 14
    c: Equal(g0,g35) = 14
    c: Coincident(g39,g40)
    c: Coincident(g40,g41)
    c: Coincident(g41,g42)
    c: Coincident(g42,g39)
    c: Horizontal(g39)
    c: Horizontal(g41)
    c: Vertical(g40)
    c: Vertical(g42)
    c: Equal(g38,g42) = 14
    c: Equal(g35,g39) = 14
    c: DistanceY(g35,g41) = 6
    c: DistanceX(g35,g41) = 0
    c: Coincident(g26,g43)
    c: Coincident(g35,g43)
    c: Equal(g16,g43)
    c: Parallel(g43,g16)
    c: Coincident(g44,g45)
    c: Coincident(g45,g46)
    c: Coincident(g46,g47)
    c: Coincident(g47,g44)
    c: Horizontal(g44)
    c: Horizontal(g46)
    c: Vertical(g45)
    c: Vertical(g47)
    c: Equal(g3,g47) = 14
    c: Equal(g0,g44) = 14
    c: Coincident(g48,g49)
    c: Coincident(g49,g50)
    c: Coincident(g50,g51)
    c: Coincident(g51,g48)
    c: Horizontal(g48)
    c: Horizontal(g50)
    c: Vertical(g49)
    c: Vertical(g51)
    c: Equal(g47,g51) = 14
    c: Equal(g44,g48) = 14
    c: DistanceY(g44,g50) = 6
    c: DistanceX(g44,g50) = 0
    c: Coincident(g35,g52)
    c: Coincident(g44,g52)
    c: Equal(g16,g52)
    c: Parallel(g52,g16)
    c: DistanceX(g-6,g2) = 375
    c: DistanceY(g-6,g2) = 90
FEATURE [Sketcher::SketchObject] Sketch007  label="user"
  ExternalGeometry = -> [Pad]
  FullyConstrained = true
  MapMode = 5
  Placement = pos=(0,0,1.5) rot=(0,0,1;0rad)
  Support = -> [Pad]
  sketch-geometry (32):
    g0: LineSegment StartX=190 StartY=-21 StartZ=0 EndX=204 EndY=-21 EndZ=0
    g1: LineSegment StartX=204 StartY=-21 StartZ=0 EndX=204 EndY=-35 EndZ=0
    g2: LineSegment StartX=204 StartY=-35 StartZ=0 EndX=190 EndY=-35 EndZ=0
    g3: LineSegment StartX=190 StartY=-35 StartZ=0 EndX=190 EndY=-21 EndZ=0
    g4: LineSegment StartX=210 StartY=-21 StartZ=0 EndX=224 EndY=-21 EndZ=0
    g5: LineSegment StartX=224 StartY=-21 StartZ=0 EndX=224 EndY=-35 EndZ=0
    g6: LineSegment StartX=224 StartY=-35 StartZ=0 EndX=210 EndY=-35 EndZ=0
    g7: LineSegment StartX=210 StartY=-35 StartZ=0 EndX=210 EndY=-21 EndZ=0
    g8: LineSegment StartX=230 StartY=-21 StartZ=0 EndX=244 EndY=-21 EndZ=0
    g9: LineSegment StartX=244 StartY=-21 StartZ=0 EndX=244 EndY=-35 EndZ=0
    g10: LineSegment StartX=244 StartY=-35 StartZ=0 EndX=230 EndY=-35 EndZ=0
    g11: LineSegment StartX=230 StartY=-35 StartZ=0 EndX=230 EndY=-21 EndZ=0
    g12: LineSegment StartX=250 StartY=-21 StartZ=0 EndX=264 EndY=-21 EndZ=0
    g13: LineSegment StartX=264 StartY=-21 StartZ=0 EndX=264 EndY=-35 EndZ=0
    g14: LineSegment StartX=264 StartY=-35 StartZ=0 EndX=250 EndY=-35 EndZ=0
    g15: LineSegment StartX=250 StartY=-35 StartZ=0 EndX=250 EndY=-21 EndZ=0
    g16: LineSegment StartX=190 StartY=19 StartZ=0 EndX=204 EndY=19 EndZ=0
    g17: LineSegment StartX=204 StartY=19 StartZ=0 EndX=204 EndY=5 EndZ=0
    g18: LineSegment StartX=204 StartY=5 StartZ=0 EndX=190 EndY=5 EndZ=0
    g19: LineSegment StartX=190 StartY=5 StartZ=0 EndX=190 EndY=19 EndZ=0
    g20: LineSegment StartX=210 StartY=19 StartZ=0 EndX=224 EndY=19 EndZ=0
    g21: LineSegment StartX=224 StartY=19 StartZ=0 EndX=224 EndY=5 EndZ=0
    g22: LineSegment StartX=224 StartY=5 StartZ=0 EndX=210 EndY=5 EndZ=0
    g23: LineSegment StartX=210 StartY=5 StartZ=0 EndX=210 EndY=19 EndZ=0
    g24: LineSegment StartX=230 StartY=19 StartZ=0 EndX=244 EndY=19 EndZ=0
    g25: LineSegment StartX=244 StartY=19 StartZ=0 EndX=244 EndY=5 EndZ=0
    g26: LineSegment StartX=244 StartY=5 StartZ=0 EndX=230 EndY=5 EndZ=0
    g27: LineSegment StartX=230 StartY=5 StartZ=0 EndX=230 EndY=19 EndZ=0
    g28: LineSegment StartX=250 StartY=19 StartZ=0 EndX=264 EndY=19 EndZ=0
    g29: LineSegment StartX=264 StartY=19 StartZ=0 EndX=264 EndY=5 EndZ=0
    g30: LineSegment StartX=264 StartY=5 StartZ=0 EndX=250 EndY=5 EndZ=0
    g31: LineSegment StartX=250 StartY=5 StartZ=0 EndX=250 EndY=19 EndZ=0
  constraints (96):
    c: Coincident(g0,g1)
    c: Coincident(g1,g2)
    c: Coincident(g2,g3)
    c: Coincident(g3,g0)
    c: Horizontal(g0)
    c: Horizontal(g2)
    c: Vertical(g1)
    c: Vertical(g3)
    c: DistanceY(g3,g3) = 14
    c: DistanceX(g2,g2) = 14
    c: Coincident(g4,g5)
    c: Coincident(g5,g6)
    c: Coincident(g6,g7)
    c: Coincident(g7,g4)
    c: Horizontal(g4)
    c: Horizontal(g6)
    c: Vertical(g5)
    c: Vertical(g7)
    c: Equal(g3,g7) = 14
    c: Equal(g2,g6) = 14
    c: Coincident(g8,g9)
    c: Coincident(g9,g10)
    c: Coincident(g10,g11)
    c: Coincident(g11,g8)
    c: Horizontal(g8)
    c: Horizontal(g10)
    c: Vertical(g9)
    c: Vertical(g11)
    c: Equal(g3,g11) = 14
    c: Equal(g2,g10) = 14
    c: Coincident(g12,g13)
    c: Coincident(g13,g14)
    c: Coincident(g14,g15)
    c: Coincident(g15,g12)
    c: Horizontal(g12)
    c: Horizontal(g14)
    c: Vertical(g13)
    c: Vertical(g15)
    c: Equal(g3,g15) = 14
    c: Equal(g2,g14) = 14
    c: Coincident(g16,g17)
    c: Coincident(g17,g18)
    c: Coincident(g18,g19)
    c: Coincident(g19,g16)
    c: Horizontal(g16)
    c: Horizontal(g18)
    c: Vertical(g17)
    c: Vertical(g19)
    c: Equal(g3,g19) = 14
    c: Equal(g2,g18) = 14
    c: Coincident(g20,g21)
    c: Coincident(g21,g22)
    c: Coincident(g22,g23)
    c: Coincident(g23,g20)
    c: Horizontal(g20)
    c: Horizontal(g22)
    c: Vertical(g21)
    c: Vertical(g23)
    c: Equal(g3,g23) = 14
    c: Equal(g2,g22) = 14
    c: Coincident(g24,g25)
    c: Coincident(g25,g26)
    c: Coincident(g26,g27)
    c: Coincident(g27,g24)
    c: Horizontal(g24)
    c: Horizontal(g26)
    c: Vertical(g25)
    c: Vertical(g27)
    c: Equal(g3,g27) = 14
    c: Equal(g2,g26) = 14
    c: Coincident(g28,g29)
    c: Coincident(g29,g30)
    c: Coincident(g30,g31)
    c: Coincident(g31,g28)
    c: Horizontal(g28)
    c: Horizontal(g30)
    c: Vertical(g29)
    c: Vertical(g31)
    c: Equal(g3,g31) = 14
    c: Equal(g2,g30) = 14
    c: DistanceY(g0,g18) = 26
    c: DistanceY(g17,g22) = 0
    c: DistanceY(g1,g6) = 0
    c: DistanceY(g5,g10) = 0
    c: DistanceY(g9,g14) = 0
    c: DistanceY(g21,g26) = 0
    c: DistanceY(g25,g30) = 0
    c: DistanceX(g16,g20) = 6
    c: DistanceX(g20,g24) = 6
    c: DistanceX(g24,g28) = 6
    c: DistanceX(g0,g17) = 0
    c: DistanceX(g4,g21) = 0
    c: DistanceX(g8,g25) = 0
    c: DistanceX(g29,g12) = 0
    c: DistanceX(g2,g-5) = 125
    c: DistanceY(g-5,g2) = 110
FEATURE [Sketcher::SketchObject] Sketch008  label="bank"
  ExternalGeometry = -> [Pad]
  FullyConstrained = true
  MapMode = 5
  Placement = pos=(0,0,1.5) rot=(0,0,1;0rad)
  Support = -> [Pad]
  sketch-geometry (32):
    g0: LineSegment StartX=30 StartY=-111 StartZ=0 EndX=44 EndY=-111 EndZ=0
    g1: LineSegment StartX=44 StartY=-111 StartZ=0 EndX=44 EndY=-125 EndZ=0
    g2: LineSegment StartX=44 StartY=-125 StartZ=0 EndX=30 EndY=-125 EndZ=0
    g3: LineSegment StartX=30 StartY=-125 StartZ=0 EndX=30 EndY=-111 EndZ=0
    g4: LineSegment StartX=30 StartY=-91 StartZ=0 EndX=44 EndY=-91 EndZ=0
    g5: LineSegment StartX=44 StartY=-91 StartZ=0 EndX=44 EndY=-105 EndZ=0
    g6: LineSegment StartX=44 StartY=-105 StartZ=0 EndX=30 EndY=-105 EndZ=0
    g7: LineSegment StartX=30 StartY=-105 StartZ=0 EndX=30 EndY=-91 EndZ=0
    g8: LineSegment StartX=30 StartY=-41 StartZ=0 EndX=44 EndY=-41 EndZ=0
    g9: LineSegment StartX=44 StartY=-41 StartZ=0 EndX=44 EndY=-55 EndZ=0
    g10: LineSegment StartX=44 StartY=-55 StartZ=0 EndX=30 EndY=-55 EndZ=0
    g11: LineSegment StartX=30 StartY=-55 StartZ=0 EndX=30 EndY=-41 EndZ=0
    g12: LineSegment StartX=30 StartY=-21 StartZ=0 EndX=44 EndY=-21 EndZ=0
    g13: LineSegment StartX=44 StartY=-21 StartZ=0 EndX=44 EndY=-35 EndZ=0
    g14: LineSegment StartX=44 StartY=-35 StartZ=0 EndX=30 EndY=-35 EndZ=0
    g15: LineSegment StartX=30 StartY=-35 StartZ=0 EndX=30 EndY=-21 EndZ=0
    g16: LineSegment StartX=30 StartY=-1 StartZ=0 EndX=44 EndY=-1 EndZ=0
    g17: LineSegment StartX=44 StartY=-1 StartZ=0 EndX=44 EndY=-15 EndZ=0
    g18: LineSegment StartX=44 StartY=-15 StartZ=0 EndX=30 EndY=-15 EndZ=0
    g19: LineSegment StartX=30 StartY=-15 StartZ=0 EndX=30 EndY=-1 EndZ=0
    g20: LineSegment StartX=30 StartY=19 StartZ=0 EndX=44 EndY=19 EndZ=0
    g21: LineSegment StartX=44 StartY=19 StartZ=0 EndX=44 EndY=5 EndZ=0
    g22: LineSegment StartX=44 StartY=5 StartZ=0 EndX=30 EndY=5 EndZ=0
    g23: LineSegment StartX=30 StartY=5 StartZ=0 EndX=30 EndY=19 EndZ=0
    g24: LineSegment StartX=23 StartY=-66 StartZ=0 EndX=51 EndY=-66 EndZ=0
    g25: LineSegment StartX=51 StartY=-66 StartZ=0 EndX=51 EndY=-80 EndZ=0
    g26: LineSegment StartX=51 StartY=-80 StartZ=0 EndX=23 EndY=-80 EndZ=0
    g27: LineSegment StartX=23 StartY=-80 StartZ=0 EndX=23 EndY=-66 EndZ=0
    g28: LineSegment StartX=30 StartY=39 StartZ=0 EndX=44 EndY=39 EndZ=0
    g29: LineSegment StartX=44 StartY=39 StartZ=0 EndX=44 EndY=25 EndZ=0
    g30: LineSegment StartX=44 StartY=25 StartZ=0 EndX=30 EndY=25 EndZ=0
    g31: LineSegment StartX=30 StartY=25 StartZ=0 EndX=30 EndY=39 EndZ=0
  constraints (96):
    c: Coincident(g0,g1)
    c: Coincident(g1,g2)
    c: Coincident(g2,g3)
    c: Coincident(g3,g0)
    c: Horizontal(g0)
    c: Horizontal(g2)
    c: Vertical(g1)
    c: Vertical(g3)
    c: DistanceY(g3,g3) = 14
    c: DistanceX(g0,g0) = 14
    c: Coincident(g4,g5)
    c: Coincident(g5,g6)
    c: Coincident(g6,g7)
    c: Coincident(g7,g4)
    c: Horizontal(g4)
    c: Horizontal(g6)
    c: Vertical(g5)
    c: Vertical(g7)
    c: Equal(g3,g7) = 14
    c: Equal(g0,g4) = 14
    c: Coincident(g8,g9)
    c: Coincident(g9,g10)
    c: Coincident(g10,g11)
    c: Coincident(g11,g8)
    c: Horizontal(g8)
    c: Horizontal(g10)
    c: Vertical(g9)
    c: Vertical(g11)
    c: Equal(g3,g11) = 14
    c: Equal(g0,g8) = 14
    c: Coincident(g12,g13)
    c: Coincident(g13,g14)
    c: Coincident(g14,g15)
    c: Coincident(g15,g12)
    c: Horizontal(g12)
    c: Horizontal(g14)
    c: Vertical(g13)
    c: Vertical(g15)
    c: Equal(g3,g15) = 14
    c: Equal(g0,g12) = 14
    c: Coincident(g16,g17)
    c: Coincident(g17,g18)
    c: Coincident(g18,g19)
    c: Coincident(g19,g16)
    c: Horizontal(g16)
    c: Horizontal(g18)
    c: Vertical(g17)
    c: Vertical(g19)
    c: Equal(g3,g19) = 14
    c: Equal(g0,g16) = 14
    c: Coincident(g20,g21)
    c: Coincident(g21,g22)
    c: Coincident(g22,g23)
    c: Coincident(g23,g20)
    c: Horizontal(g20)
    c: Horizontal(g22)
    c: Vertical(g21)
    c: Vertical(g23)
    c: Equal(g3,g23) = 14
    c: Equal(g0,g20) = 14
    c: DistanceY(g0,g6) = 6
    c: DistanceX(g6,g0) = 0
    c: DistanceY(g8,g14) = 6
    c: DistanceY(g12,g18) = 6
    c: DistanceY(g16,g22) = 6
    c: DistanceX(g16,g22) = 0
    c: DistanceX(g12,g18) = 0
    c: DistanceX(g8,g14) = 0
    c: Coincident(g24,g25)
    c: Coincident(g25,g26)
    c: Coincident(g26,g27)
    c: Coincident(g27,g24)
    c: Horizontal(g24)
    c: Horizontal(g26)
    c: Vertical(g25)
    c: Vertical(g27)
    c: DistanceY(g27,g27) = 14
    c: DistanceX(g24,g24) = 28
    c: DistanceX(g26,g4) = 7
    c: DistanceX(g24,g10) = 7
    c: Coincident(g28,g29)
    c: Coincident(g29,g30)
    c: Coincident(g30,g31)
    c: Coincident(g31,g28)
    c: Horizontal(g28)
    c: Horizontal(g30)
    c: Vertical(g29)
    c: Vertical(g31)
    c: Equal(g3,g31) = 14
    c: Equal(g0,g28) = 14
    c: DistanceY(g20,g30) = 6
    c: DistanceX(g20,g30) = 0
    c: DistanceY(g24,g10) = 11
    c: DistanceY(g4,g26) = 11
    c: DistanceY(g-4,g2) = 20
    c: DistanceX(g-6,g2) = 345
FEATURE [Sketcher::SketchObject] Sketch009  label="encoders"
  ExternalGeometry = -> [Pad]
  FullyConstrained = true
  MapMode = 5
  Placement = pos=(0,0,1.5) rot=(0,0,1;0rad)
  Support = -> [Pad]
  sketch-geometry (500):
    g0: Circle CenterX=295 CenterY=128 CenterZ=0 NormalX=0 NormalY=0 NormalZ=1 AngleXU=0 Radius=5
    g1: Circle CenterX=295 CenterY=128 CenterZ=0 NormalX=0 NormalY=0 NormalZ=1 AngleXU=0 Radius=12
    g2: LineSegment StartX=295 StartY=128 StartZ=0 EndX=295 EndY=116 EndZ=0
    g3: LineSegment StartX=295 StartY=128 StartZ=0 EndX=303.485 EndY=119.515 EndZ=0
    g4: LineSegment StartX=303.485 StartY=119.515 StartZ=0 EndX=303.132 EndY=119.161 EndZ=0
    g5: LineSegment StartX=303.132 StartY=119.161 StartZ=0 EndX=300.303 EndY=121.99 EndZ=0
    g6: LineSegment StartX=300.303 StartY=121.99 StartZ=0 EndX=301.01 EndY=122.697 EndZ=0
    g7: LineSegment StartX=301.01 StartY=122.697 StartZ=0 EndX=303.839 EndY=119.868 EndZ=0
    g8: LineSegment StartX=303.839 StartY=119.868 StartZ=0 EndX=303.485 EndY=119.515 EndZ=0
    g9: LineSegment StartX=295 StartY=128 StartZ=0 EndX=305.692 EndY=122.552 EndZ=0
    g10: LineSegment StartX=305.692 StartY=122.552 StartZ=0 EndX=305.465 EndY=122.107 EndZ=0
    g11: LineSegment StartX=305.465 StartY=122.107 StartZ=0 EndX=301.901 EndY=123.923 EndZ=0
    g12: LineSegment StartX=301.901 StartY=123.923 StartZ=0 EndX=302.355 EndY=124.814 EndZ=0
    g13: LineSegment StartX=302.355 StartY=124.814 StartZ=0 EndX=305.919 EndY=122.998 EndZ=0
    g14: LineSegment StartX=305.919 StartY=122.998 StartZ=0 EndX=305.692 EndY=122.552 EndZ=0
    g15: LineSegment StartX=295 StartY=128 StartZ=0 EndX=306.852 EndY=126.123 EndZ=0
    g16: LineSegment StartX=306.852 StartY=126.123 StartZ=0 EndX=306.774 EndY=125.629 EndZ=0
    g17: LineSegment StartX=306.774 StartY=125.629 StartZ=0 EndX=302.823 EndY=126.255 EndZ=0
    g18: LineSegment StartX=302.823 StartY=126.255 StartZ=0 EndX=302.98 EndY=127.242 EndZ=0
    g19: LineSegment StartX=302.98 StartY=127.242 StartZ=0 EndX=306.93 EndY=126.617 EndZ=0
    g20: LineSegment StartX=306.93 StartY=126.617 StartZ=0 EndX=306.852 EndY=126.123 EndZ=0
    g21: LineSegment StartX=295 StartY=128 StartZ=0 EndX=306.852 EndY=129.877 EndZ=0
    g22: LineSegment StartX=306.852 StartY=129.877 StartZ=0 EndX=306.93 EndY=129.383 EndZ=0
    g23: LineSegment StartX=306.93 StartY=129.383 StartZ=0 EndX=302.98 EndY=128.758 EndZ=0
    g24: LineSegment StartX=302.98 StartY=128.758 StartZ=0 EndX=302.823 EndY=129.745 EndZ=0
    g25: LineSegment StartX=302.823 StartY=129.745 StartZ=0 EndX=306.774 EndY=130.371 EndZ=0
    g26: LineSegment StartX=306.774 StartY=130.371 StartZ=0 EndX=306.852 EndY=129.877 EndZ=0
    g27: LineSegment StartX=295 StartY=128 StartZ=0 EndX=305.692 EndY=133.448 EndZ=0
    g28: LineSegment StartX=305.692 StartY=133.448 StartZ=0 EndX=305.919 EndY=133.002 EndZ=0
    g29: LineSegment StartX=305.919 StartY=133.002 StartZ=0 EndX=302.355 EndY=131.186 EndZ=0
    g30: LineSegment StartX=302.355 StartY=131.186 StartZ=0 EndX=301.901 EndY=132.077 EndZ=0
    g31: LineSegment StartX=301.901 StartY=132.077 StartZ=0 EndX=305.465 EndY=133.893 EndZ=0
    g32: LineSegment StartX=305.465 StartY=133.893 StartZ=0 EndX=305.692 EndY=133.448 EndZ=0
    g33: LineSegment StartX=295 StartY=128 StartZ=0 EndX=303.485 EndY=136.485 EndZ=0
    g34: LineSegment StartX=303.485 StartY=136.485 StartZ=0 EndX=303.839 EndY=136.132 EndZ=0
    g35: LineSegment StartX=303.839 StartY=136.132 StartZ=0 EndX=301.01 EndY=133.303 EndZ=0
    g36: LineSegment StartX=301.01 StartY=133.303 StartZ=0 EndX=300.303 EndY=134.01 EndZ=0
    g37: LineSegment StartX=300.303 StartY=134.01 StartZ=0 EndX=303.132 EndY=136.839 EndZ=0
    g38: LineSegment StartX=303.132 StartY=136.839 StartZ=0 EndX=303.485 EndY=136.485 EndZ=0
    g39: LineSegment StartX=295 StartY=128 StartZ=0 EndX=300.448 EndY=138.692 EndZ=0
    g40: LineSegment StartX=300.448 StartY=138.692 StartZ=0 EndX=300.893 EndY=138.465 EndZ=0
    g41: LineSegment StartX=300.893 StartY=138.465 StartZ=0 EndX=299.077 EndY=134.901 EndZ=0
    g42: LineSegment StartX=299.077 StartY=134.901 StartZ=0 EndX=298.186 EndY=135.355 EndZ=0
    g43: LineSegment StartX=298.186 StartY=135.355 StartZ=0 EndX=300.002 EndY=138.919 EndZ=0
    g44: LineSegment StartX=300.002 StartY=138.919 StartZ=0 EndX=300.448 EndY=138.692 EndZ=0
    g45: LineSegment StartX=295 StartY=128 StartZ=0 EndX=296.877 EndY=139.852 EndZ=0
    g46: LineSegment StartX=296.877 StartY=139.852 StartZ=0 EndX=297.371 EndY=139.774 EndZ=0
    g47: LineSegment StartX=297.371 StartY=139.774 StartZ=0 EndX=296.745 EndY=135.823 EndZ=0
    g48: LineSegment StartX=296.745 StartY=135.823 StartZ=0 EndX=295.758 EndY=135.98 EndZ=0
    g49: LineSegment StartX=295.758 StartY=135.98 StartZ=0 EndX=296.383 EndY=139.93 EndZ=0
    g50: LineSegment StartX=296.383 StartY=139.93 StartZ=0 EndX=296.877 EndY=139.852 EndZ=0
    g51: LineSegment StartX=295 StartY=128 StartZ=0 EndX=293.123 EndY=139.852 EndZ=0
    g52: LineSegment StartX=293.123 StartY=139.852 StartZ=0 EndX=293.617 EndY=139.93 EndZ=0
    g53: LineSegment StartX=293.617 StartY=139.93 StartZ=0 EndX=294.242 EndY=135.98 EndZ=0
    g54: LineSegment StartX=294.242 StartY=135.98 StartZ=0 EndX=293.255 EndY=135.823 EndZ=0
    g55: LineSegment StartX=293.255 StartY=135.823 StartZ=0 EndX=292.629 EndY=139.774 EndZ=0
    g56: LineSegment StartX=292.629 StartY=139.774 StartZ=0 EndX=293.123 EndY=139.852 EndZ=0
    g57: LineSegment StartX=295 StartY=128 StartZ=0 EndX=289.552 EndY=138.692 EndZ=0
    g58: LineSegment StartX=289.552 StartY=138.692 StartZ=0 EndX=289.998 EndY=138.919 EndZ=0
    g59: LineSegment StartX=289.998 StartY=138.919 StartZ=0 EndX=291.814 EndY=135.355 EndZ=0
    g60: LineSegment StartX=291.814 StartY=135.355 StartZ=0 EndX=290.923 EndY=134.901 EndZ=0
    g61: LineSegment StartX=290.923 StartY=134.901 StartZ=0 EndX=289.107 EndY=138.465 EndZ=0
    g62: LineSegment StartX=289.107 StartY=138.465 StartZ=0 EndX=289.552 EndY=138.692 EndZ=0
    g63: LineSegment StartX=295 StartY=128 StartZ=0 EndX=284.308 EndY=133.448 EndZ=0
    g64: LineSegment StartX=284.308 StartY=133.448 StartZ=0 EndX=284.535 EndY=133.893 EndZ=0
    g65: LineSegment StartX=284.535 StartY=133.893 StartZ=0 EndX=288.099 EndY=132.077 EndZ=0
    g66: LineSegment StartX=288.099 StartY=132.077 StartZ=0 EndX=287.645 EndY=131.186 EndZ=0
    g67: LineSegment StartX=287.645 StartY=131.186 StartZ=0 EndX=284.081 EndY=133.002 EndZ=0
    g68: LineSegment StartX=284.081 StartY=133.002 StartZ=0 EndX=284.308 EndY=133.448 EndZ=0
    g69: LineSegment StartX=295 StartY=128 StartZ=0 EndX=283.148 EndY=129.877 EndZ=0
    g70: LineSegment StartX=283.148 StartY=129.877 StartZ=0 EndX=283.226 EndY=130.371 EndZ=0
    g71: LineSegment StartX=283.226 StartY=130.371 StartZ=0 EndX=287.177 EndY=129.745 EndZ=0
    g72: LineSegment StartX=287.177 StartY=129.745 StartZ=0 EndX=287.02 EndY=128.758 EndZ=0
    g73: LineSegment StartX=287.02 StartY=128.758 StartZ=0 EndX=283.07 EndY=129.383 EndZ=0
    g74: LineSegment StartX=283.07 StartY=129.383 StartZ=0 EndX=283.148 EndY=129.877 EndZ=0
    g75: LineSegment StartX=295 StartY=128 StartZ=0 EndX=283.148 EndY=126.123 EndZ=0
    g76: LineSegment StartX=283.148 StartY=126.123 StartZ=0 EndX=283.07 EndY=126.617 EndZ=0
    g77: LineSegment StartX=283.07 StartY=126.617 StartZ=0 EndX=287.02 EndY=127.242 EndZ=0
    g78: LineSegment StartX=287.02 StartY=127.242 StartZ=0 EndX=287.177 EndY=126.255 EndZ=0
    g79: LineSegment StartX=287.177 StartY=126.255 StartZ=0 EndX=283.226 EndY=125.629 EndZ=0
    g80: LineSegment StartX=283.226 StartY=125.629 StartZ=0 EndX=283.148 EndY=126.123 EndZ=0
    g81: LineSegment StartX=295 StartY=128 StartZ=0 EndX=284.308 EndY=122.552 EndZ=0
    g82: LineSegment StartX=284.308 StartY=122.552 StartZ=0 EndX=284.081 EndY=122.998 EndZ=0
    g83: LineSegment StartX=284.081 StartY=122.998 StartZ=0 EndX=287.645 EndY=124.814 EndZ=0
    g84: LineSegment StartX=287.645 StartY=124.814 StartZ=0 EndX=288.099 EndY=123.923 EndZ=0
    g85: LineSegment StartX=288.099 StartY=123.923 StartZ=0 EndX=284.535 EndY=122.107 EndZ=0
    g86: LineSegment StartX=284.535 StartY=122.107 StartZ=0 EndX=284.308 EndY=122.552 EndZ=0
    g87: LineSegment StartX=295 StartY=128 StartZ=0 EndX=286.515 EndY=136.485 EndZ=0
    g88: LineSegment StartX=286.515 StartY=136.485 StartZ=0 EndX=286.868 EndY=136.839 EndZ=0
    g89: LineSegment StartX=286.868 StartY=136.839 StartZ=0 EndX=289.697 EndY=134.01 EndZ=0
    g90: LineSegment StartX=289.697 StartY=134.01 StartZ=0 EndX=288.99 EndY=133.303 EndZ=0
    g91: LineSegment StartX=288.99 StartY=133.303 StartZ=0 EndX=286.161 EndY=136.132 EndZ=0
    g92: LineSegment StartX=286.161 StartY=136.132 StartZ=0 EndX=286.515 EndY=136.485 EndZ=0
    g93: LineSegment StartX=295 StartY=128 StartZ=0 EndX=286.515 EndY=119.515 EndZ=0
    g94: LineSegment StartX=286.515 StartY=119.515 StartZ=0 EndX=286.161 EndY=119.868 EndZ=0
    g95: LineSegment StartX=286.161 StartY=119.868 StartZ=0 EndX=288.99 EndY=122.697 EndZ=0
    g96: LineSegment StartX=288.99 StartY=122.697 StartZ=0 EndX=289.697 EndY=121.99 EndZ=0
    g97: LineSegment StartX=289.697 StartY=121.99 StartZ=0 EndX=286.868 EndY=119.161 EndZ=0
    g98: LineSegment StartX=286.868 StartY=119.161 StartZ=0 EndX=286.515 EndY=119.515 EndZ=0
    g99: Circle CenterX=295 CenterY=118 CenterZ=0 NormalX=0 NormalY=0 NormalZ=1 AngleXU=0 Radius=2
    g100: Circle CenterX=265 CenterY=128 CenterZ=0 NormalX=0 NormalY=0 NormalZ=1 AngleXU=0 Radius=5
    g101: Circle CenterX=265 CenterY=128 CenterZ=0 NormalX=0 NormalY=0 NormalZ=1 AngleXU=0 Radius=12
    g102: LineSegment StartX=265 StartY=128 StartZ=0 EndX=265 EndY=116 EndZ=0
    g103: LineSegment StartX=265 StartY=128 StartZ=0 EndX=273.485 EndY=119.515 EndZ=0
    g104: LineSegment StartX=273.485 StartY=119.515 StartZ=0 EndX=273.132 EndY=119.161 EndZ=0
    g105: LineSegment StartX=273.132 StartY=119.161 StartZ=0 EndX=270.303 EndY=121.99 EndZ=0
    g106: LineSegment StartX=270.303 StartY=121.99 StartZ=0 EndX=271.01 EndY=122.697 EndZ=0
    g107: LineSegment StartX=271.01 StartY=122.697 StartZ=0 EndX=273.839 EndY=119.868 EndZ=0
    g108: LineSegment StartX=273.839 StartY=119.868 StartZ=0 EndX=273.485 EndY=119.515 EndZ=0
    g109: LineSegment StartX=265 StartY=128 StartZ=0 EndX=275.692 EndY=122.552 EndZ=0
    g110: LineSegment StartX=275.692 StartY=122.552 StartZ=0 EndX=275.465 EndY=122.107 EndZ=0
    g111: LineSegment StartX=275.465 StartY=122.107 StartZ=0 EndX=271.901 EndY=123.923 EndZ=0
    g112: LineSegment StartX=271.901 StartY=123.923 StartZ=0 EndX=272.355 EndY=124.814 EndZ=0
    g113: LineSegment StartX=272.355 StartY=124.814 StartZ=0 EndX=275.919 EndY=122.998 EndZ=0
    g114: LineSegment StartX=275.919 StartY=122.998 StartZ=0 EndX=275.692 EndY=122.552 EndZ=0
    g115: LineSegment StartX=265 StartY=128 StartZ=0 EndX=276.852 EndY=126.123 EndZ=0
    g116: LineSegment StartX=276.852 StartY=126.123 StartZ=0 EndX=276.774 EndY=125.629 EndZ=0
    g117: LineSegment StartX=276.774 StartY=125.629 StartZ=0 EndX=272.823 EndY=126.255 EndZ=0
    g118: LineSegment StartX=272.823 StartY=126.255 StartZ=0 EndX=272.98 EndY=127.242 EndZ=0
    g119: LineSegment StartX=272.98 StartY=127.242 StartZ=0 EndX=276.93 EndY=126.617 EndZ=0
    g120: LineSegment StartX=276.93 StartY=126.617 StartZ=0 EndX=276.852 EndY=126.123 EndZ=0
    g121: LineSegment StartX=265 StartY=128 StartZ=0 EndX=276.852 EndY=129.877 EndZ=0
    g122: LineSegment StartX=276.852 StartY=129.877 StartZ=0 EndX=276.93 EndY=129.383 EndZ=0
    g123: LineSegment StartX=276.93 StartY=129.383 StartZ=0 EndX=272.98 EndY=128.758 EndZ=0
    g124: LineSegment StartX=272.98 StartY=128.758 StartZ=0 EndX=272.823 EndY=129.745 EndZ=0
    g125: LineSegment StartX=272.823 StartY=129.745 StartZ=0 EndX=276.774 EndY=130.371 EndZ=0
    g126: LineSegment StartX=276.774 StartY=130.371 StartZ=0 EndX=276.852 EndY=129.877 EndZ=0
    g127: LineSegment StartX=265 StartY=128 StartZ=0 EndX=275.692 EndY=133.448 EndZ=0
    g128: LineSegment StartX=275.692 StartY=133.448 StartZ=0 EndX=275.919 EndY=133.002 EndZ=0
    g129: LineSegment StartX=275.919 StartY=133.002 StartZ=0 EndX=272.355 EndY=131.186 EndZ=0
    g130: LineSegment StartX=272.355 StartY=131.186 StartZ=0 EndX=271.901 EndY=132.077 EndZ=0
    g131: LineSegment StartX=271.901 StartY=132.077 StartZ=0 EndX=275.465 EndY=133.893 EndZ=0
    g132: LineSegment StartX=275.465 StartY=133.893 StartZ=0 EndX=275.692 EndY=133.448 EndZ=0
    g133: LineSegment StartX=265 StartY=128 StartZ=0 EndX=273.485 EndY=136.485 EndZ=0
    g134: LineSegment StartX=273.485 StartY=136.485 StartZ=0 EndX=273.839 EndY=136.132 EndZ=0
    g135: LineSegment StartX=273.839 StartY=136.132 StartZ=0 EndX=271.01 EndY=133.303 EndZ=0
    g136: LineSegment StartX=271.01 StartY=133.303 StartZ=0 EndX=270.303 EndY=134.01 EndZ=0
    g137: LineSegment StartX=270.303 StartY=134.01 StartZ=0 EndX=273.132 EndY=136.839 EndZ=0
    g138: LineSegment StartX=273.132 StartY=136.839 StartZ=0 EndX=273.485 EndY=136.485 EndZ=0
    g139: LineSegment StartX=265 StartY=128 StartZ=0 EndX=270.448 EndY=138.692 EndZ=0
    g140: LineSegment StartX=270.448 StartY=138.692 StartZ=0 EndX=270.893 EndY=138.465 EndZ=0
    g141: LineSegment StartX=270.893 StartY=138.465 StartZ=0 EndX=269.077 EndY=134.901 EndZ=0
    g142: LineSegment StartX=269.077 StartY=134.901 StartZ=0 EndX=268.186 EndY=135.355 EndZ=0
    g143: LineSegment StartX=268.186 StartY=135.355 StartZ=0 EndX=270.002 EndY=138.919 EndZ=0
    g144: LineSegment StartX=270.002 StartY=138.919 StartZ=0 EndX=270.448 EndY=138.692 EndZ=0
    g145: LineSegment StartX=265 StartY=128 StartZ=0 EndX=266.877 EndY=139.852 EndZ=0
    g146: LineSegment StartX=266.877 StartY=139.852 StartZ=0 EndX=267.371 EndY=139.774 EndZ=0
    g147: LineSegment StartX=267.371 StartY=139.774 StartZ=0 EndX=266.745 EndY=135.823 EndZ=0
    g148: LineSegment StartX=266.745 StartY=135.823 StartZ=0 EndX=265.758 EndY=135.98 EndZ=0
    g149: LineSegment StartX=265.758 StartY=135.98 StartZ=0 EndX=266.383 EndY=139.93 EndZ=0
    g150: LineSegment StartX=266.383 StartY=139.93 StartZ=0 EndX=266.877 EndY=139.852 EndZ=0
    g151: LineSegment StartX=265 StartY=128 StartZ=0 EndX=263.123 EndY=139.852 EndZ=0
    g152: LineSegment StartX=263.123 StartY=139.852 StartZ=0 EndX=263.617 EndY=139.93 EndZ=0
    g153: LineSegment StartX=263.617 StartY=139.93 StartZ=0 EndX=264.242 EndY=135.98 EndZ=0
    g154: LineSegment StartX=264.242 StartY=135.98 StartZ=0 EndX=263.255 EndY=135.823 EndZ=0
    g155: LineSegment StartX=263.255 StartY=135.823 StartZ=0 EndX=262.629 EndY=139.774 EndZ=0
    g156: LineSegment StartX=262.629 StartY=139.774 StartZ=0 EndX=263.123 EndY=139.852 EndZ=0
    g157: LineSegment StartX=265 StartY=128 StartZ=0 EndX=259.552 EndY=138.692 EndZ=0
    g158: LineSegment StartX=259.552 StartY=138.692 StartZ=0 EndX=259.998 EndY=138.919 EndZ=0
    g159: LineSegment StartX=259.998 StartY=138.919 StartZ=0 EndX=261.814 EndY=135.355 EndZ=0
    g160: LineSegment StartX=261.814 StartY=135.355 StartZ=0 EndX=260.923 EndY=134.901 EndZ=0
    g161: LineSegment StartX=260.923 StartY=134.901 StartZ=0 EndX=259.107 EndY=138.465 EndZ=0
    g162: LineSegment StartX=259.107 StartY=138.465 StartZ=0 EndX=259.552 EndY=138.692 EndZ=0
    g163: LineSegment StartX=265 StartY=128 StartZ=0 EndX=254.308 EndY=133.448 EndZ=0
    g164: LineSegment StartX=254.308 StartY=133.448 StartZ=0 EndX=254.535 EndY=133.893 EndZ=0
    g165: LineSegment StartX=254.535 StartY=133.893 StartZ=0 EndX=258.099 EndY=132.077 EndZ=0
    g166: LineSegment StartX=258.099 StartY=132.077 StartZ=0 EndX=257.645 EndY=131.186 EndZ=0
    g167: LineSegment StartX=257.645 StartY=131.186 StartZ=0 EndX=254.081 EndY=133.002 EndZ=0
    g168: LineSegment StartX=254.081 StartY=133.002 StartZ=0 EndX=254.308 EndY=133.448 EndZ=0
    g169: LineSegment StartX=265 StartY=128 StartZ=0 EndX=253.148 EndY=129.877 EndZ=0
    g170: LineSegment StartX=253.148 StartY=129.877 StartZ=0 EndX=253.226 EndY=130.371 EndZ=0
    g171: LineSegment StartX=253.226 StartY=130.371 StartZ=0 EndX=257.177 EndY=129.745 EndZ=0
    g172: LineSegment StartX=257.177 StartY=129.745 StartZ=0 EndX=257.02 EndY=128.758 EndZ=0
    g173: LineSegment StartX=257.02 StartY=128.758 StartZ=0 EndX=253.07 EndY=129.383 EndZ=0
    g174: LineSegment StartX=253.07 StartY=129.383 StartZ=0 EndX=253.148 EndY=129.877 EndZ=0
    g175: LineSegment StartX=265 StartY=128 StartZ=0 EndX=253.148 EndY=126.123 EndZ=0
    g176: LineSegment StartX=253.148 StartY=126.123 StartZ=0 EndX=253.07 EndY=126.617 EndZ=0
    g177: LineSegment StartX=253.07 StartY=126.617 StartZ=0 EndX=257.02 EndY=127.242 EndZ=0
    g178: LineSegment StartX=257.02 StartY=127.242 StartZ=0 EndX=257.177 EndY=126.255 EndZ=0
    g179: LineSegment StartX=257.177 StartY=126.255 StartZ=0 EndX=253.226 EndY=125.629 EndZ=0
    g180: LineSegment StartX=253.226 StartY=125.629 StartZ=0 EndX=253.148 EndY=126.123 EndZ=0
    g181: LineSegment StartX=265 StartY=128 StartZ=0 EndX=254.308 EndY=122.552 EndZ=0
    g182: LineSegment StartX=254.308 StartY=122.552 StartZ=0 EndX=254.081 EndY=122.998 EndZ=0
    g183: LineSegment StartX=254.081 StartY=122.998 StartZ=0 EndX=257.645 EndY=124.814 EndZ=0
    g184: LineSegment StartX=257.645 StartY=124.814 StartZ=0 EndX=258.099 EndY=123.923 EndZ=0
    g185: LineSegment StartX=258.099 StartY=123.923 StartZ=0 EndX=254.535 EndY=122.107 EndZ=0
    g186: LineSegment StartX=254.535 StartY=122.107 StartZ=0 EndX=254.308 EndY=122.552 EndZ=0
    g187: LineSegment StartX=265 StartY=128 StartZ=0 EndX=256.515 EndY=136.485 EndZ=0
    g188: LineSegment StartX=256.515 StartY=136.485 StartZ=0 EndX=256.868 EndY=136.839 EndZ=0
    g189: LineSegment StartX=256.868 StartY=136.839 StartZ=0 EndX=259.697 EndY=134.01 EndZ=0
    g190: LineSegment StartX=259.697 StartY=134.01 StartZ=0 EndX=258.99 EndY=133.303 EndZ=0
    g191: LineSegment StartX=258.99 StartY=133.303 StartZ=0 EndX=256.161 EndY=136.132 EndZ=0
    g192: LineSegment StartX=256.161 StartY=136.132 StartZ=0 EndX=256.515 EndY=136.485 EndZ=0
    g193: LineSegment StartX=265 StartY=128 StartZ=0 EndX=256.515 EndY=119.515 EndZ=0
    g194: LineSegment StartX=256.515 StartY=119.515 StartZ=0 EndX=256.161 EndY=119.868 EndZ=0
    g195: LineSegment StartX=256.161 StartY=119.868 StartZ=0 EndX=258.99 EndY=122.697 EndZ=0
    g196: LineSegment StartX=258.99 StartY=122.697 StartZ=0 EndX=259.697 EndY=121.99 EndZ=0
    g197: LineSegment StartX=259.697 StartY=121.99 StartZ=0 EndX=256.868 EndY=119.161 EndZ=0
    g198: LineSegment StartX=256.868 StartY=119.161 StartZ=0 EndX=256.515 EndY=119.515 EndZ=0
    g199: Circle CenterX=265 CenterY=118 CenterZ=0 NormalX=0 NormalY=0 NormalZ=1 AngleXU=0 Radius=2
    g200: Circle CenterX=235 CenterY=128 CenterZ=0 NormalX=0 NormalY=0 NormalZ=1 AngleXU=0 Radius=5
    g201: Circle CenterX=235 CenterY=128 CenterZ=0 NormalX=0 NormalY=0 NormalZ=1 AngleXU=0 Radius=12
    g202: LineSegment StartX=235 StartY=128 StartZ=0 EndX=235 EndY=116 EndZ=0
    g203: LineSegment StartX=235 StartY=128 StartZ=0 EndX=243.485 EndY=119.515 EndZ=0
    g204: LineSegment StartX=243.485 StartY=119.515 StartZ=0 EndX=243.132 EndY=119.161 EndZ=0
    g205: LineSegment StartX=243.132 StartY=119.161 StartZ=0 EndX=240.303 EndY=121.99 EndZ=0
    g206: LineSegment StartX=240.303 StartY=121.99 StartZ=0 EndX=241.01 EndY=122.697 EndZ=0
    g207: LineSegment StartX=241.01 StartY=122.697 StartZ=0 EndX=243.839 EndY=119.868 EndZ=0
    g208: LineSegment StartX=243.839 StartY=119.868 StartZ=0 EndX=243.485 EndY=119.515 EndZ=0
    g209: LineSegment StartX=235 StartY=128 StartZ=0 EndX=245.692 EndY=122.552 EndZ=0
    g210: LineSegment StartX=245.692 StartY=122.552 StartZ=0 EndX=245.465 EndY=122.107 EndZ=0
    g211: LineSegment StartX=245.465 StartY=122.107 StartZ=0 EndX=241.901 EndY=123.923 EndZ=0
    g212: LineSegment StartX=241.901 StartY=123.923 StartZ=0 EndX=242.355 EndY=124.814 EndZ=0
    g213: LineSegment StartX=242.355 StartY=124.814 StartZ=0 EndX=245.919 EndY=122.998 EndZ=0
    g214: LineSegment StartX=245.919 StartY=122.998 StartZ=0 EndX=245.692 EndY=122.552 EndZ=0
    g215: LineSegment StartX=235 StartY=128 StartZ=0 EndX=246.852 EndY=126.123 EndZ=0
    g216: LineSegment StartX=246.852 StartY=126.123 StartZ=0 EndX=246.774 EndY=125.629 EndZ=0
    g217: LineSegment StartX=246.774 StartY=125.629 StartZ=0 EndX=242.823 EndY=126.255 EndZ=0
    g218: LineSegment StartX=242.823 StartY=126.255 StartZ=0 EndX=242.98 EndY=127.242 EndZ=0
    g219: LineSegment StartX=242.98 StartY=127.242 StartZ=0 EndX=246.93 EndY=126.617 EndZ=0
    g220: LineSegment StartX=246.93 StartY=126.617 StartZ=0 EndX=246.852 EndY=126.123 EndZ=0
    g221: LineSegment StartX=235 StartY=128 StartZ=0 EndX=246.852 EndY=129.877 EndZ=0
    g222: LineSegment StartX=246.852 StartY=129.877 StartZ=0 EndX=246.93 EndY=129.383 EndZ=0
    g223: LineSegment StartX=246.93 StartY=129.383 StartZ=0 EndX=242.98 EndY=128.758 EndZ=0
    g224: LineSegment StartX=242.98 StartY=128.758 StartZ=0 EndX=242.823 EndY=129.745 EndZ=0
    g225: LineSegment StartX=242.823 StartY=129.745 StartZ=0 EndX=246.774 EndY=130.371 EndZ=0
    g226: LineSegment StartX=246.774 StartY=130.371 StartZ=0 EndX=246.852 EndY=129.877 EndZ=0
    g227: LineSegment StartX=235 StartY=128 StartZ=0 EndX=245.692 EndY=133.448 EndZ=0
    g228: LineSegment StartX=245.692 StartY=133.448 StartZ=0 EndX=245.919 EndY=133.002 EndZ=0
    g229: LineSegment StartX=245.919 StartY=133.002 StartZ=0 EndX=242.355 EndY=131.186 EndZ=0
    g230: LineSegment StartX=242.355 StartY=131.186 StartZ=0 EndX=241.901 EndY=132.077 EndZ=0
    g231: LineSegment StartX=241.901 StartY=132.077 StartZ=0 EndX=245.465 EndY=133.893 EndZ=0
    g232: LineSegment StartX=245.465 StartY=133.893 StartZ=0 EndX=245.692 EndY=133.448 EndZ=0
    g233: LineSegment StartX=235 StartY=128 StartZ=0 EndX=243.485 EndY=136.485 EndZ=0
    g234: LineSegment StartX=243.485 StartY=136.485 StartZ=0 EndX=243.839 EndY=136.132 EndZ=0
    g235: LineSegment StartX=243.839 StartY=136.132 StartZ=0 EndX=241.01 EndY=133.303 EndZ=0
    g236: LineSegment StartX=241.01 StartY=133.303 StartZ=0 EndX=240.303 EndY=134.01 EndZ=0
    g237: LineSegment StartX=240.303 StartY=134.01 StartZ=0 EndX=243.132 EndY=136.839 EndZ=0
    g238: LineSegment StartX=243.132 StartY=136.839 StartZ=0 EndX=243.485 EndY=136.485 EndZ=0
    g239: LineSegment StartX=235 StartY=128 StartZ=0 EndX=240.448 EndY=138.692 EndZ=0
    g240: LineSegment StartX=240.448 StartY=138.692 StartZ=0 EndX=240.893 EndY=138.465 EndZ=0
    g241: LineSegment StartX=240.893 StartY=138.465 StartZ=0 EndX=239.077 EndY=134.901 EndZ=0
    g242: LineSegment StartX=239.077 StartY=134.901 StartZ=0 EndX=238.186 EndY=135.355 EndZ=0
    g243: LineSegment StartX=238.186 StartY=135.355 StartZ=0 EndX=240.002 EndY=138.919 EndZ=0
    g244: LineSegment StartX=240.002 StartY=138.919 StartZ=0 EndX=240.448 EndY=138.692 EndZ=0
    g245: LineSegment StartX=235 StartY=128 StartZ=0 EndX=236.877 EndY=139.852 EndZ=0
    g246: LineSegment StartX=236.877 StartY=139.852 StartZ=0 EndX=237.371 EndY=139.774 EndZ=0
    g247: LineSegment StartX=237.371 StartY=139.774 StartZ=0 EndX=236.745 EndY=135.823 EndZ=0
    g248: LineSegment StartX=236.745 StartY=135.823 StartZ=0 EndX=235.758 EndY=135.98 EndZ=0
    g249: LineSegment StartX=235.758 StartY=135.98 StartZ=0 EndX=236.383 EndY=139.93 EndZ=0
    g250: LineSegment StartX=236.383 StartY=139.93 StartZ=0 EndX=236.877 EndY=139.852 EndZ=0
    g251: LineSegment StartX=235 StartY=128 StartZ=0 EndX=233.123 EndY=139.852 EndZ=0
    g252: LineSegment StartX=233.123 StartY=139.852 StartZ=0 EndX=233.617 EndY=139.93 EndZ=0
    g253: LineSegment StartX=233.617 StartY=139.93 StartZ=0 EndX=234.242 EndY=135.98 EndZ=0
    g254: LineSegment StartX=234.242 StartY=135.98 StartZ=0 EndX=233.255 EndY=135.823 EndZ=0
    g255: LineSegment StartX=233.255 StartY=135.823 StartZ=0 EndX=232.629 EndY=139.774 EndZ=0
    g256: LineSegment StartX=232.629 StartY=139.774 StartZ=0 EndX=233.123 EndY=139.852 EndZ=0
    g257: LineSegment StartX=235 StartY=128 StartZ=0 EndX=229.552 EndY=138.692 EndZ=0
    g258: LineSegment StartX=229.552 StartY=138.692 StartZ=0 EndX=229.998 EndY=138.919 EndZ=0
    g259: LineSegment StartX=229.998 StartY=138.919 StartZ=0 EndX=231.814 EndY=135.355 EndZ=0
    g260: LineSegment StartX=231.814 StartY=135.355 StartZ=0 EndX=230.923 EndY=134.901 EndZ=0
    g261: LineSegment StartX=230.923 StartY=134.901 StartZ=0 EndX=229.107 EndY=138.465 EndZ=0
    g262: LineSegment StartX=229.107 StartY=138.465 StartZ=0 EndX=229.552 EndY=138.692 EndZ=0
    g263: LineSegment StartX=235 StartY=128 StartZ=0 EndX=224.308 EndY=133.448 EndZ=0
    g264: LineSegment StartX=224.308 StartY=133.448 StartZ=0 EndX=224.535 EndY=133.893 EndZ=0
    g265: LineSegment StartX=224.535 StartY=133.893 StartZ=0 EndX=228.099 EndY=132.077 EndZ=0
    g266: LineSegment StartX=228.099 StartY=132.077 StartZ=0 EndX=227.645 EndY=131.186 EndZ=0
    g267: LineSegment StartX=227.645 StartY=131.186 StartZ=0 EndX=224.081 EndY=133.002 EndZ=0
    g268: LineSegment StartX=224.081 StartY=133.002 StartZ=0 EndX=224.308 EndY=133.448 EndZ=0
    g269: LineSegment StartX=235 StartY=128 StartZ=0 EndX=223.148 EndY=129.877 EndZ=0
    g270: LineSegment StartX=223.148 StartY=129.877 StartZ=0 EndX=223.226 EndY=130.371 EndZ=0
    g271: LineSegment StartX=223.226 StartY=130.371 StartZ=0 EndX=227.177 EndY=129.745 EndZ=0
    g272: LineSegment StartX=227.177 StartY=129.745 StartZ=0 EndX=227.02 EndY=128.758 EndZ=0
    g273: LineSegment StartX=227.02 StartY=128.758 StartZ=0 EndX=223.07 EndY=129.383 EndZ=0
    g274: LineSegment StartX=223.07 StartY=129.383 StartZ=0 EndX=223.148 EndY=129.877 EndZ=0
    g275: LineSegment StartX=235 StartY=128 StartZ=0 EndX=223.148 EndY=126.123 EndZ=0
    g276: LineSegment StartX=223.148 StartY=126.123 StartZ=0 EndX=223.07 EndY=126.617 EndZ=0
    g277: LineSegment StartX=223.07 StartY=126.617 StartZ=0 EndX=227.02 EndY=127.242 EndZ=0
    g278: LineSegment StartX=227.02 StartY=127.242 StartZ=0 EndX=227.177 EndY=126.255 EndZ=0
    g279: LineSegment StartX=227.177 StartY=126.255 StartZ=0 EndX=223.226 EndY=125.629 EndZ=0
    g280: LineSegment StartX=223.226 StartY=125.629 StartZ=0 EndX=223.148 EndY=126.123 EndZ=0
    g281: LineSegment StartX=235 StartY=128 StartZ=0 EndX=224.308 EndY=122.552 EndZ=0
    g282: LineSegment StartX=224.308 StartY=122.552 StartZ=0 EndX=224.081 EndY=122.998 EndZ=0
    g283: LineSegment StartX=224.081 StartY=122.998 StartZ=0 EndX=227.645 EndY=124.814 EndZ=0
    g284: LineSegment StartX=227.645 StartY=124.814 StartZ=0 EndX=228.099 EndY=123.923 EndZ=0
    g285: LineSegment StartX=228.099 StartY=123.923 StartZ=0 EndX=224.535 EndY=122.107 EndZ=0
    g286: LineSegment StartX=224.535 StartY=122.107 StartZ=0 EndX=224.308 EndY=122.552 EndZ=0
    g287: LineSegment StartX=235 StartY=128 StartZ=0 EndX=226.515 EndY=136.485 EndZ=0
    g288: LineSegment StartX=226.515 StartY=136.485 StartZ=0 EndX=226.868 EndY=136.839 EndZ=0
    g289: LineSegment StartX=226.868 StartY=136.839 StartZ=0 EndX=229.697 EndY=134.01 EndZ=0
    g290: LineSegment StartX=229.697 StartY=134.01 StartZ=0 EndX=228.99 EndY=133.303 EndZ=0
    g291: LineSegment StartX=228.99 StartY=133.303 StartZ=0 EndX=226.161 EndY=136.132 EndZ=0
    g292: LineSegment StartX=226.161 StartY=136.132 StartZ=0 EndX=226.515 EndY=136.485 EndZ=0
    g293: LineSegment StartX=235 StartY=128 StartZ=0 EndX=226.515 EndY=119.515 EndZ=0
    g294: LineSegment StartX=226.515 StartY=119.515 StartZ=0 EndX=226.161 EndY=119.868 EndZ=0
    g295: LineSegment StartX=226.161 StartY=119.868 StartZ=0 EndX=228.99 EndY=122.697 EndZ=0
    g296: LineSegment StartX=228.99 StartY=122.697 StartZ=0 EndX=229.697 EndY=121.99 EndZ=0
    g297: LineSegment StartX=229.697 StartY=121.99 StartZ=0 EndX=226.868 EndY=119.161 EndZ=0
    g298: LineSegment StartX=226.868 StartY=119.161 StartZ=0 EndX=226.515 EndY=119.515 EndZ=0
    g299: Circle CenterX=235 CenterY=118 CenterZ=0 NormalX=0 NormalY=0 NormalZ=1 AngleXU=0 Radius=2
    g300: Circle CenterX=205 CenterY=128 CenterZ=0 NormalX=0 NormalY=0 NormalZ=1 AngleXU=0 Radius=5
    g301: Circle CenterX=205 CenterY=128 CenterZ=0 NormalX=0 NormalY=0 NormalZ=1 AngleXU=0 Radius=12
    g302: LineSegment StartX=205 StartY=128 StartZ=0 EndX=205 EndY=116 EndZ=0
    g303: LineSegment StartX=205 StartY=128 StartZ=0 EndX=213.485 EndY=119.515 EndZ=0
    g304: LineSegment StartX=213.485 StartY=119.515 StartZ=0 EndX=213.132 EndY=119.161 EndZ=0
    g305: LineSegment StartX=213.132 StartY=119.161 StartZ=0 EndX=210.303 EndY=121.99 EndZ=0
    g306: LineSegment StartX=210.303 StartY=121.99 StartZ=0 EndX=211.01 EndY=122.697 EndZ=0
    g307: LineSegment StartX=211.01 StartY=122.697 StartZ=0 EndX=213.839 EndY=119.868 EndZ=0
    g308: LineSegment StartX=213.839 StartY=119.868 StartZ=0 EndX=213.485 EndY=119.515 EndZ=0
    g309: LineSegment StartX=205 StartY=128 StartZ=0 EndX=215.692 EndY=122.552 EndZ=0
    g310: LineSegment StartX=215.692 StartY=122.552 StartZ=0 EndX=215.465 EndY=122.107 EndZ=0
    g311: LineSegment StartX=215.465 StartY=122.107 StartZ=0 EndX=211.901 EndY=123.923 EndZ=0
    g312: LineSegment StartX=211.901 StartY=123.923 StartZ=0 EndX=212.355 EndY=124.814 EndZ=0
    g313: LineSegment StartX=212.355 StartY=124.814 StartZ=0 EndX=215.919 EndY=122.998 EndZ=0
    g314: LineSegment StartX=215.919 StartY=122.998 StartZ=0 EndX=215.692 EndY=122.552 EndZ=0
    g315: LineSegment StartX=205 StartY=128 StartZ=0 EndX=216.852 EndY=126.123 EndZ=0
    g316: LineSegment StartX=216.852 StartY=126.123 StartZ=0 EndX=216.774 EndY=125.629 EndZ=0
    g317: LineSegment StartX=216.774 StartY=125.629 StartZ=0 EndX=212.823 EndY=126.255 EndZ=0
    g318: LineSegment StartX=212.823 StartY=126.255 StartZ=0 EndX=212.98 EndY=127.242 EndZ=0
    g319: LineSegment StartX=212.98 StartY=127.242 StartZ=0 EndX=216.93 EndY=126.617 EndZ=0
    g320: LineSegment StartX=216.93 StartY=126.617 StartZ=0 EndX=216.852 EndY=126.123 EndZ=0
    g321: LineSegment StartX=205 StartY=128 StartZ=0 EndX=216.852 EndY=129.877 EndZ=0
    g322: LineSegment StartX=216.852 StartY=129.877 StartZ=0 EndX=216.93 EndY=129.383 EndZ=0
    g323: LineSegment StartX=216.93 StartY=129.383 StartZ=0 EndX=212.98 EndY=128.758 EndZ=0
    g324: LineSegment StartX=212.98 StartY=128.758 StartZ=0 EndX=212.823 EndY=129.745 EndZ=0
    g325: LineSegment StartX=212.823 StartY=129.745 StartZ=0 EndX=216.774 EndY=130.371 EndZ=0
    g326: LineSegment StartX=216.774 StartY=130.371 StartZ=0 EndX=216.852 EndY=129.877 EndZ=0
    g327: LineSegment StartX=205 StartY=128 StartZ=0 EndX=215.692 EndY=133.448 EndZ=0
    g328: LineSegment StartX=215.692 StartY=133.448 StartZ=0 EndX=215.919 EndY=133.002 EndZ=0
    g329: LineSegment StartX=215.919 StartY=133.002 StartZ=0 EndX=212.355 EndY=131.186 EndZ=0
    g330: LineSegment StartX=212.355 StartY=131.186 StartZ=0 EndX=211.901 EndY=132.077 EndZ=0
    g331: LineSegment StartX=211.901 StartY=132.077 StartZ=0 EndX=215.465 EndY=133.893 EndZ=0
    g332: LineSegment StartX=215.465 StartY=133.893 StartZ=0 EndX=215.692 EndY=133.448 EndZ=0
    g333: LineSegment StartX=205 StartY=128 StartZ=0 EndX=213.485 EndY=136.485 EndZ=0
    g334: LineSegment StartX=213.485 StartY=136.485 StartZ=0 EndX=213.839 EndY=136.132 EndZ=0
    g335: LineSegment StartX=213.839 StartY=136.132 StartZ=0 EndX=211.01 EndY=133.303 EndZ=0
    g336: LineSegment StartX=211.01 StartY=133.303 StartZ=0 EndX=210.303 EndY=134.01 EndZ=0
    g337: LineSegment StartX=210.303 StartY=134.01 StartZ=0 EndX=213.132 EndY=136.839 EndZ=0
    g338: LineSegment StartX=213.132 StartY=136.839 StartZ=0 EndX=213.485 EndY=136.485 EndZ=0
    g339: LineSegment StartX=205 StartY=128 StartZ=0 EndX=210.448 EndY=138.692 EndZ=0
    g340: LineSegment StartX=210.448 StartY=138.692 StartZ=0 EndX=210.893 EndY=138.465 EndZ=0
    g341: LineSegment StartX=210.893 StartY=138.465 StartZ=0 EndX=209.077 EndY=134.901 EndZ=0
    g342: LineSegment StartX=209.077 StartY=134.901 StartZ=0 EndX=208.186 EndY=135.355 EndZ=0
    g343: LineSegment StartX=208.186 StartY=135.355 StartZ=0 EndX=210.002 EndY=138.919 EndZ=0
    g344: LineSegment StartX=210.002 StartY=138.919 StartZ=0 EndX=210.448 EndY=138.692 EndZ=0
    g345: LineSegment StartX=205 StartY=128 StartZ=0 EndX=206.877 EndY=139.852 EndZ=0
    g346: LineSegment StartX=206.877 StartY=139.852 StartZ=0 EndX=207.371 EndY=139.774 EndZ=0
    g347: LineSegment StartX=207.371 StartY=139.774 StartZ=0 EndX=206.745 EndY=135.823 EndZ=0
    g348: LineSegment StartX=206.745 StartY=135.823 StartZ=0 EndX=205.758 EndY=135.98 EndZ=0
    g349: LineSegment StartX=205.758 StartY=135.98 StartZ=0 EndX=206.383 EndY=139.93 EndZ=0
    g350: LineSegment StartX=206.383 StartY=139.93 StartZ=0 EndX=206.877 EndY=139.852 EndZ=0
    g351: LineSegment StartX=205 StartY=128 StartZ=0 EndX=203.123 EndY=139.852 EndZ=0
    g352: LineSegment StartX=203.123 StartY=139.852 StartZ=0 EndX=203.617 EndY=139.93 EndZ=0
    g353: LineSegment StartX=203.617 StartY=139.93 StartZ=0 EndX=204.242 EndY=135.98 EndZ=0
    g354: LineSegment StartX=204.242 StartY=135.98 StartZ=0 EndX=203.255 EndY=135.823 EndZ=0
    g355: LineSegment StartX=203.255 StartY=135.823 StartZ=0 EndX=202.629 EndY=139.774 EndZ=0
    g356: LineSegment StartX=202.629 StartY=139.774 StartZ=0 EndX=203.123 EndY=139.852 EndZ=0
    g357: LineSegment StartX=205 StartY=128 StartZ=0 EndX=199.552 EndY=138.692 EndZ=0
    g358: LineSegment StartX=199.552 StartY=138.692 StartZ=0 EndX=199.998 EndY=138.919 EndZ=0
    g359: LineSegment StartX=199.998 StartY=138.919 StartZ=0 EndX=201.814 EndY=135.355 EndZ=0
    g360: LineSegment StartX=201.814 StartY=135.355 StartZ=0 EndX=200.923 EndY=134.901 EndZ=0
    g361: LineSegment StartX=200.923 StartY=134.901 StartZ=0 EndX=199.107 EndY=138.465 EndZ=0
    g362: LineSegment StartX=199.107 StartY=138.465 StartZ=0 EndX=199.552 EndY=138.692 EndZ=0
    g363: LineSegment StartX=205 StartY=128 StartZ=0 EndX=194.308 EndY=133.448 EndZ=0
    g364: LineSegment StartX=194.308 StartY=133.448 StartZ=0 EndX=194.535 EndY=133.893 EndZ=0
    g365: LineSegment StartX=194.535 StartY=133.893 StartZ=0 EndX=198.099 EndY=132.077 EndZ=0
    g366: LineSegment StartX=198.099 StartY=132.077 StartZ=0 EndX=197.645 EndY=131.186 EndZ=0
    g367: LineSegment StartX=197.645 StartY=131.186 StartZ=0 EndX=194.081 EndY=133.002 EndZ=0
    g368: LineSegment StartX=194.081 StartY=133.002 StartZ=0 EndX=194.308 EndY=133.448 EndZ=0
    g369: LineSegment StartX=205 StartY=128 StartZ=0 EndX=193.148 EndY=129.877 EndZ=0
    g370: LineSegment StartX=193.148 StartY=129.877 StartZ=0 EndX=193.226 EndY=130.371 EndZ=0
    g371: LineSegment StartX=193.226 StartY=130.371 StartZ=0 EndX=197.177 EndY=129.745 EndZ=0
    g372: LineSegment StartX=197.177 StartY=129.745 StartZ=0 EndX=197.02 EndY=128.758 EndZ=0
    g373: LineSegment StartX=197.02 StartY=128.758 StartZ=0 EndX=193.07 EndY=129.383 EndZ=0
    g374: LineSegment StartX=193.07 StartY=129.383 StartZ=0 EndX=193.148 EndY=129.877 EndZ=0
    g375: LineSegment StartX=205 StartY=128 StartZ=0 EndX=193.148 EndY=126.123 EndZ=0
    g376: LineSegment StartX=193.148 StartY=126.123 StartZ=0 EndX=193.07 EndY=126.617 EndZ=0
    g377: LineSegment StartX=193.07 StartY=126.617 StartZ=0 EndX=197.02 EndY=127.242 EndZ=0
    g378: LineSegment StartX=197.02 StartY=127.242 StartZ=0 EndX=197.177 EndY=126.255 EndZ=0
    g379: LineSegment StartX=197.177 StartY=126.255 StartZ=0 EndX=193.226 EndY=125.629 EndZ=0
    g380: LineSegment StartX=193.226 StartY=125.629 StartZ=0 EndX=193.148 EndY=126.123 EndZ=0
    g381: LineSegment StartX=205 StartY=128 StartZ=0 EndX=194.308 EndY=122.552 EndZ=0
    g382: LineSegment StartX=194.308 StartY=122.552 StartZ=0 EndX=194.081 EndY=122.998 EndZ=0
    g383: LineSegment StartX=194.081 StartY=122.998 StartZ=0 EndX=197.645 EndY=124.814 EndZ=0
    g384: LineSegment StartX=197.645 StartY=124.814 StartZ=0 EndX=198.099 EndY=123.923 EndZ=0
    g385: LineSegment StartX=198.099 StartY=123.923 StartZ=0 EndX=194.535 EndY=122.107 EndZ=0
    g386: LineSegment StartX=194.535 StartY=122.107 StartZ=0 EndX=194.308 EndY=122.552 EndZ=0
    g387: LineSegment StartX=205 StartY=128 StartZ=0 EndX=196.515 EndY=136.485 EndZ=0
    g388: LineSegment StartX=196.515 StartY=136.485 StartZ=0 EndX=196.868 EndY=136.839 EndZ=0
    g389: LineSegment StartX=196.868 StartY=136.839 StartZ=0 EndX=199.697 EndY=134.01 EndZ=0
    g390: LineSegment StartX=199.697 StartY=134.01 StartZ=0 EndX=198.99 EndY=133.303 EndZ=0
    g391: LineSegment StartX=198.99 StartY=133.303 StartZ=0 EndX=196.161 EndY=136.132 EndZ=0
    g392: LineSegment StartX=196.161 StartY=136.132 StartZ=0 EndX=196.515 EndY=136.485 EndZ=0
    g393: LineSegment StartX=205 StartY=128 StartZ=0 EndX=196.515 EndY=119.515 EndZ=0
    g394: LineSegment StartX=196.515 StartY=119.515 StartZ=0 EndX=196.161 EndY=119.868 EndZ=0
    g395: LineSegment StartX=196.161 StartY=119.868 StartZ=0 EndX=198.99 EndY=122.697 EndZ=0
    g396: LineSegment StartX=198.99 StartY=122.697 StartZ=0 EndX=199.697 EndY=121.99 EndZ=0
    g397: LineSegment StartX=199.697 StartY=121.99 StartZ=0 EndX=196.868 EndY=119.161 EndZ=0
    g398: LineSegment StartX=196.868 StartY=119.161 StartZ=0 EndX=196.515 EndY=119.515 EndZ=0
    g399: Circle CenterX=205 CenterY=118 CenterZ=0 NormalX=0 NormalY=0 NormalZ=1 AngleXU=0 Radius=2
    ... +100 more geometry lines
  constraints (1415):
    c: Diameter(g0) = 10
    c: DistanceX(g0,g-4) = 20
    c: DistanceY(g0,g-4) = 17
    c: Coincident(g1,g0)
    c: Diameter(g1) = 24
    c: Coincident(g2,g0)
    c: PointOnObject(g2,g1)
    c: DistanceX(g2,g2) = 0
    c: Coincident(g3,g0)
    c: Angle(g2,g3) = 0.785398
    c: PointOnObject(g3,g1)
    c: Coincident(g4,g3)
    c: Coincident(g5,g4)
    c: Coincident(g6,g5)
    c: Coincident(g7,g6)
    c: Coincident(g8,g7)
    c: Coincident(g8,g4)
    c: Perpendicular(g3,g8)
    c: Equal(g8,g4)
    c: Parallel(g5,g7)
    c: Equal(g7,g5)
    c: Parallel(g4,g8)
    c: Perpendicular(g4,g5)
    c: Distance(g7) = 4
    c: Distance(g8) = 0.5
    c: Coincident(g10,g9)
    c: Coincident(g11,g10)
    c: Coincident(g12,g11)
    c: Coincident(g13,g12)
    c: Coincident(g14,g13)
    c: Coincident(g14,g10)
    c: Perpendicular(g9,g14)
    c: Equal(g14,g10)
    c: Parallel(g11,g13)
    c: Equal(g13,g11)
    c: Parallel(g10,g14)
    c: Perpendicular(g10,g11)
    c: Equal(g7,g13) = 4
    c: Equal(g8,g14) = 0.5
    c: Coincident(g16,g15)
    c: Coincident(g17,g16)
    c: Coincident(g18,g17)
    c: Coincident(g19,g18)
    c: Coincident(g20,g19)
    c: Coincident(g20,g16)
    c: Perpendicular(g15,g20)
    c: Equal(g20,g16)
    c: Parallel(g17,g19)
    c: Equal(g19,g17)
    c: Parallel(g16,g20)
    c: Perpendicular(g16,g17)
    c: Equal(g7,g19) = 4
    c: Equal(g8,g20) = 0.5
    c: Coincident(g22,g21)
    c: Coincident(g23,g22)
    c: Coincident(g24,g23)
    c: Coincident(g25,g24)
    c: Coincident(g26,g25)
    c: Coincident(g26,g22)
    c: Perpendicular(g21,g26)
    c: Equal(g26,g22)
    c: Parallel(g23,g25)
    c: Equal(g25,g23)
    c: Parallel(g22,g26)
    c: Perpendicular(g22,g23)
    c: Equal(g7,g25) = 4
    c: Equal(g8,g26) = 0.5
    c: Coincident(g28,g27)
    c: Coincident(g29,g28)
    c: Coincident(g30,g29)
    c: Coincident(g31,g30)
    c: Coincident(g32,g31)
    c: Coincident(g32,g28)
    c: Perpendicular(g27,g32)
    c: Equal(g32,g28)
    c: Parallel(g29,g31)
    c: Equal(g31,g29)
    c: Parallel(g28,g32)
    c: Perpendicular(g28,g29)
    c: Equal(g7,g31) = 4
    c: Equal(g8,g32) = 0.5
    c: Coincident(g34,g33)
    c: Coincident(g35,g34)
    c: Coincident(g36,g35)
    c: Coincident(g37,g36)
    c: Coincident(g38,g37)
    c: Coincident(g38,g34)
    c: Perpendicular(g33,g38)
    c: Equal(g38,g34)
    c: Parallel(g35,g37)
    c: Equal(g37,g35)
    c: Parallel(g34,g38)
    c: Perpendicular(g34,g35)
    c: Equal(g7,g37) = 4
    c: Equal(g8,g38) = 0.5
    c: Coincident(g40,g39)
    c: Coincident(g41,g40)
    c: Coincident(g42,g41)
    c: Coincident(g43,g42)
    c: Coincident(g44,g43)
    c: Coincident(g44,g40)
    c: Perpendicular(g39,g44)
    c: Equal(g44,g40)
    c: Parallel(g41,g43)
    c: Equal(g43,g41)
    c: Parallel(g40,g44)
    c: Perpendicular(g40,g41)
    c: Equal(g7,g43) = 4
    c: Equal(g8,g44) = 0.5
    c: Coincident(g46,g45)
    c: Coincident(g47,g46)
    c: Coincident(g48,g47)
    c: Coincident(g49,g48)
    c: Coincident(g50,g49)
    c: Coincident(g50,g46)
    c: Perpendicular(g45,g50)
    c: Equal(g50,g46)
    c: Parallel(g47,g49)
    c: Equal(g49,g47)
    c: Parallel(g46,g50)
    c: Perpendicular(g46,g47)
    c: Equal(g7,g49) = 4
    c: Equal(g8,g50) = 0.5
    c: Coincident(g52,g51)
    c: Coincident(g53,g52)
    c: Coincident(g54,g53)
    c: Coincident(g55,g54)
    c: Coincident(g56,g55)
    c: Coincident(g56,g52)
    c: Perpendicular(g51,g56)
    c: Equal(g56,g52)
    c: Parallel(g53,g55)
    c: Equal(g55,g53)
    c: Parallel(g52,g56)
    c: Perpendicular(g52,g53)
    c: Equal(g7,g55) = 4
    c: Equal(g8,g56) = 0.5
    c: Coincident(g58,g57)
    c: Coincident(g59,g58)
    c: Coincident(g60,g59)
    c: Coincident(g61,g60)
    c: Coincident(g62,g61)
    c: Coincident(g62,g58)
    c: Perpendicular(g57,g62)
    c: Equal(g62,g58)
    c: Parallel(g59,g61)
    c: Equal(g61,g59)
    c: Parallel(g58,g62)
    c: Perpendicular(g58,g59)
    c: Equal(g7,g61) = 4
    c: Equal(g8,g62) = 0.5
    c: Coincident(g64,g63)
    c: Coincident(g65,g64)
    c: Coincident(g66,g65)
    c: Coincident(g67,g66)
    c: Coincident(g68,g67)
    c: Coincident(g68,g64)
    c: Perpendicular(g63,g68)
    c: Equal(g68,g64)
    c: Parallel(g65,g67)
    c: Equal(g67,g65)
    c: Parallel(g64,g68)
    c: Perpendicular(g64,g65)
    c: Equal(g7,g67) = 4
    c: Equal(g8,g68) = 0.5
    c: Coincident(g70,g69)
    c: Coincident(g71,g70)
    c: Coincident(g72,g71)
    c: Coincident(g73,g72)
    c: Coincident(g74,g73)
    c: Coincident(g74,g70)
    c: Perpendicular(g69,g74)
    c: Equal(g74,g70)
    c: Parallel(g71,g73)
    c: Equal(g73,g71)
    c: Parallel(g70,g74)
    c: Perpendicular(g70,g71)
    c: Equal(g7,g73) = 4
    c: Equal(g8,g74) = 0.5
    c: Coincident(g76,g75)
    c: Coincident(g77,g76)
    c: Coincident(g78,g77)
    c: Coincident(g79,g78)
    c: Coincident(g80,g79)
    c: Coincident(g80,g76)
    c: Perpendicular(g75,g80)
    c: Equal(g80,g76)
    c: Parallel(g77,g79)
    c: Equal(g79,g77)
    c: Parallel(g76,g80)
    c: Perpendicular(g76,g77)
    c: Equal(g7,g79) = 4
    c: Equal(g8,g80) = 0.5
    c: Coincident(g82,g81)
    c: Coincident(g83,g82)
    c: Coincident(g84,g83)
    c: Coincident(g85,g84)
    c: Coincident(g86,g85)
    c: Coincident(g86,g82)
    c: Perpendicular(g81,g86)
    c: Equal(g86,g82)
    c: Parallel(g83,g85)
    c: Equal(g85,g83)
    c: Parallel(g82,g86)
    c: Perpendicular(g82,g83)
    c: Equal(g7,g85) = 4
    c: Equal(g8,g86) = 0.5
    c: Coincident(g88,g87)
    c: Coincident(g89,g88)
    c: Coincident(g90,g89)
    c: Coincident(g91,g90)
    c: Coincident(g92,g91)
    c: Coincident(g92,g88)
    c: Perpendicular(g87,g92)
    c: Equal(g92,g88)
    c: Parallel(g89,g91)
    c: Equal(g91,g89)
    c: Parallel(g88,g92)
    c: Perpendicular(g88,g89)
    c: Equal(g7,g91) = 4
    c: Equal(g8,g92) = 0.5
    c: Coincident(g94,g93)
    c: Coincident(g95,g94)
    c: Coincident(g96,g95)
    c: Coincident(g97,g96)
    c: Coincident(g98,g97)
    c: Coincident(g98,g94)
    c: Perpendicular(g93,g98)
    c: Equal(g98,g94)
    c: Parallel(g95,g97)
    c: Equal(g97,g95)
    c: Parallel(g94,g98)
    c: Perpendicular(g94,g95)
    c: Equal(g7,g97) = 4
    c: Equal(g8,g98) = 0.5
    c: Coincident(g9,g0)
    c: PointOnObject(g10,g1)
    c: Angle(g3,g9) = 0.314159
    c: Coincident(g15,g0)
    c: PointOnObject(g16,g1)
    c: Angle(g9,g15) = 0.314159
    c: PointOnObject(g22,g1)
    c: Coincident(g21,g0)
    c: Angle(g15,g21) = 0.314159
    c: Coincident(g0,g27)
    c: Coincident(g0,g33)
    c: Coincident(g39,g0)
    c: PointOnObject(g28,g1)
    c: PointOnObject(g34,g1)
    c: PointOnObject(g40,g1)
    c: Angle(g21,g27) = 0.314159
    c: Angle(g27,g33) = 0.314159
    c: Angle(g33,g39) = 0.314159
    c: PointOnObject(g46,g1)
    c: PointOnObject(g52,g1)
    c: PointOnObject(g58,g1)
    c: Coincident(g45,g0)
    c: Coincident(g51,g0)
    c: Coincident(g57,g0)
    c: Angle(g39,g45) = 0.314159
    c: Angle(g45,g51) = 0.314159
    c: Angle(g51,g57) = 0.314159
    c: Coincident(g87,g0)
    c: PointOnObject(g88,g1)
    c: Angle(g57,g87) = 0.314159
    c: PointOnObject(g64,g1)
    c: Coincident(g63,g0)
    c: Angle(g87,g63) = 0.314159
    c: Coincident(g69,g0)
    c: Coincident(g75,g0)
    c: Coincident(g81,g0)
    c: PointOnObject(g70,g1)
    c: PointOnObject(g76,g1)
    c: PointOnObject(g82,g1)
    c: Angle(g75,g81) = 0.314159
    c: Angle(g69,g75) = 0.314159
    c: Angle(g63,g69) = 0.314159
    c: Coincident(g93,g0)
    c: PointOnObject(g94,g1)
    c: Angle(g81,g93) = 0.314159
    c: PointOnObject(g99,g2)
    c: Diameter(g99) = 4
    c: DistanceY(g99,g0) = 10
    c: Diameter(g100) = 10
    c: Coincident(g101,g100)
    c: Diameter(g101) = 24
    c: Coincident(g102,g100)
    c: PointOnObject(g102,g101)
    c: DistanceX(g102,g102) = 0
    c: Coincident(g103,g100)
    c: Angle(g102,g103) = 0.785398
    c: PointOnObject(g103,g101)
    c: Coincident(g104,g103)
    c: Coincident(g105,g104)
    c: Coincident(g106,g105)
    c: Coincident(g107,g106)
    c: Coincident(g108,g107)
    c: Coincident(g108,g104)
    c: Perpendicular(g103,g108)
    c: Equal(g108,g104)
    c: Parallel(g105,g107)
    c: Equal(g107,g105)
    c: Parallel(g104,g108)
    c: Perpendicular(g104,g105)
    c: Distance(g107) = 4
    c: Distance(g108) = 0.5
    c: Coincident(g110,g109)
    c: Coincident(g111,g110)
    c: Coincident(g112,g111)
    c: Coincident(g113,g112)
    c: Coincident(g114,g113)
    c: Coincident(g114,g110)
    c: Perpendicular(g109,g114)
    c: Equal(g114,g110)
    c: Parallel(g111,g113)
    c: Equal(g113,g111)
    c: Parallel(g110,g114)
    c: Perpendicular(g110,g111)
    c: Equal(g107,g113) = 4
    c: Equal(g108,g114) = 0.5
    c: Coincident(g116,g115)
    c: Coincident(g117,g116)
    c: Coincident(g118,g117)
    c: Coincident(g119,g118)
    c: Coincident(g120,g119)
    c: Coincident(g120,g116)
    c: Perpendicular(g115,g120)
    c: Equal(g120,g116)
    c: Parallel(g117,g119)
    c: Equal(g119,g117)
    c: Parallel(g116,g120)
    c: Perpendicular(g116,g117)
    c: Equal(g107,g119) = 4
    c: Equal(g108,g120) = 0.5
    c: Coincident(g122,g121)
    c: Coincident(g123,g122)
    c: Coincident(g124,g123)
    c: Coincident(g125,g124)
    c: Coincident(g126,g125)
    c: Coincident(g126,g122)
    c: Perpendicular(g121,g126)
    c: Equal(g126,g122)
    c: Parallel(g123,g125)
    c: Equal(g125,g123)
    c: Parallel(g122,g126)
    c: Perpendicular(g122,g123)
    c: Equal(g107,g125) = 4
    c: Equal(g108,g126) = 0.5
    c: Coincident(g128,g127)
    c: Coincident(g129,g128)
    c: Coincident(g130,g129)
    c: Coincident(g131,g130)
    c: Coincident(g132,g131)
    c: Coincident(g132,g128)
    c: Perpendicular(g127,g132)
    c: Equal(g132,g128)
    c: Parallel(g129,g131)
    c: Equal(g131,g129)
    c: Parallel(g128,g132)
    c: Perpendicular(g128,g129)
    c: Equal(g107,g131) = 4
    c: Equal(g108,g132) = 0.5
    c: Coincident(g134,g133)
    c: Coincident(g135,g134)
    c: Coincident(g136,g135)
    c: Coincident(g137,g136)
    c: Coincident(g138,g137)
    c: Coincident(g138,g134)
    c: Perpendicular(g133,g138)
    c: Equal(g138,g134)
    c: Parallel(g135,g137)
    c: Equal(g137,g135)
    c: Parallel(g134,g138)
    c: Perpendicular(g134,g135)
    c: Equal(g107,g137) = 4
    c: Equal(g108,g138) = 0.5
    c: Coincident(g140,g139)
    c: Coincident(g141,g140)
    c: Coincident(g142,g141)
    c: Coincident(g143,g142)
    c: Coincident(g144,g143)
    c: Coincident(g144,g140)
    c: Perpendicular(g139,g144)
    c: Equal(g144,g140)
    c: Parallel(g141,g143)
    c: Equal(g143,g141)
    c: Parallel(g140,g144)
    c: Perpendicular(g140,g141)
    c: Equal(g107,g143) = 4
    c: Equal(g108,g144) = 0.5
    c: Coincident(g146,g145)
    c: Coincident(g147,g146)
    c: Coincident(g148,g147)
    c: Coincident(g149,g148)
    c: Coincident(g150,g149)
    c: Coincident(g150,g146)
    c: Perpendicular(g145,g150)
    c: Equal(g150,g146)
    c: Parallel(g147,g149)
    c: Equal(g149,g147)
    c: Parallel(g146,g150)
    c: Perpendicular(g146,g147)
    c: Equal(g107,g149) = 4
    c: Equal(g108,g150) = 0.5
    c: Coincident(g152,g151)
    c: Coincident(g153,g152)
    c: Coincident(g154,g153)
    c: Coincident(g155,g154)
    c: Coincident(g156,g155)
    c: Coincident(g156,g152)
    c: Perpendicular(g151,g156)
    c: Equal(g156,g152)
    c: Parallel(g153,g155)
    c: Equal(g155,g153)
    c: Parallel(g152,g156)
    c: Perpendicular(g152,g153)
    c: Equal(g107,g155) = 4
    c: Equal(g108,g156) = 0.5
    c: Coincident(g158,g157)
    c: Coincident(g159,g158)
    c: Coincident(g160,g159)
    c: Coincident(g161,g160)
    c: Coincident(g162,g161)
    c: Coincident(g162,g158)
    c: Perpendicular(g157,g162)
    c: Equal(g162,g158)
    c: Parallel(g159,g161)
    c: Equal(g161,g159)
    c: Parallel(g158,g162)
    c: Perpendicular(g158,g159)
    c: Equal(g107,g161) = 4
    c: Equal(g108,g162) = 0.5
    c: Coincident(g164,g163)
    c: Coincident(g165,g164)
    c: Coincident(g166,g165)
    c: Coincident(g167,g166)
    c: Coincident(g168,g167)
    c: Coincident(g168,g164)
    c: Perpendicular(g163,g168)
    c: Equal(g168,g164)
    c: Parallel(g165,g167)
    c: Equal(g167,g165)
    c: Parallel(g164,g168)
    c: Perpendicular(g164,g165)
    c: Equal(g107,g167) = 4
    c: Equal(g108,g168) = 0.5
    c: Coincident(g170,g169)
    c: Coincident(g171,g170)
    c: Coincident(g172,g171)
    c: Coincident(g173,g172)
    c: Coincident(g174,g173)
    c: Coincident(g174,g170)
    c: Perpendicular(g169,g174)
    c: Equal(g174,g170)
    c: Parallel(g171,g173)
    c: Equal(g173,g171)
    c: Parallel(g170,g174)
    c: Perpendicular(g170,g171)
    c: Equal(g107,g173) = 4
    c: Equal(g108,g174) = 0.5
    c: Coincident(g176,g175)
    c: Coincident(g177,g176)
    c: Coincident(g178,g177)
    c: Coincident(g179,g178)
    c: Coincident(g180,g179)
    c: Coincident(g180,g176)
    c: Perpendicular(g175,g180)
    c: Equal(g180,g176)
    c: Parallel(g177,g179)
    c: Equal(g179,g177)
    c: Parallel(g176,g180)
    c: Perpendicular(g176,g177)
    c: Equal(g107,g179) = 4
    c: Equal(g108,g180) = 0.5
    c: Coincident(g182,g181)
    c: Coincident(g183,g182)
    c: Coincident(g184,g183)
    c: Coincident(g185,g184)
    c: Coincident(g186,g185)
    c: Coincident(g186,g182)
    c: Perpendicular(g181,g186)
    c: Equal(g186,g182)
    c: Parallel(g183,g185)
    c: Equal(g185,g183)
    c: Parallel(g182,g186)
    c: Perpendicular(g182,g183)
    c: Equal(g107,g185) = 4
    c: Equal(g108,g186) = 0.5
    c: Coincident(g188,g187)
    c: Coincident(g189,g188)
    c: Coincident(g190,g189)
    c: Coincident(g191,g190)
    c: Coincident(g192,g191)
    c: Coincident(g192,g188)
    c: Perpendicular(g187,g192)
    c: Equal(g192,g188)
    c: Parallel(g189,g191)
    c: Equal(g191,g189)
    c: Parallel(g188,g192)
    c: Perpendicular(g188,g189)
    c: Equal(g107,g191) = 4
    c: Equal(g108,g192) = 0.5
    c: Coincident(g194,g193)
    c: Coincident(g195,g194)
    c: Coincident(g196,g195)
    c: Coincident(g197,g196)
    c: Coincident(g198,g197)
    c: Coincident(g198,g194)
    c: Perpendicular(g193,g198)
    c: Equal(g198,g194)
    c: Parallel(g195,g197)
    c: Equal(g197,g195)
    c: Parallel(g194,g198)
    c: Perpendicular(g194,g195)
    c: Equal(g107,g197) = 4
    c: Equal(g108,g198) = 0.5
    c: Coincident(g109,g100)
    c: PointOnObject(g110,g101)
    c: Angle(g103,g109) = 0.314159
    c: Coincident(g115,g100)
    c: PointOnObject(g116,g101)
    c: Angle(g109,g115) = 0.314159
    c: PointOnObject(g122,g101)
    c: Coincident(g121,g100)
    c: Angle(g115,g121) = 0.314159
    c: Coincident(g100,g127)
    c: Coincident(g100,g133)
    c: Coincident(g139,g100)
    c: PointOnObject(g128,g101)
    c: PointOnObject(g134,g101)
    c: PointOnObject(g140,g101)
    c: Angle(g121,g127) = 0.314159
    c: Angle(g127,g133) = 0.314159
    c: Angle(g133,g139) = 0.314159
    c: PointOnObject(g146,g101)
    c: PointOnObject(g152,g101)
    c: PointOnObject(g158,g101)
    c: Coincident(g145,g100)
    c: Coincident(g151,g100)
    c: Coincident(g157,g100)
    c: Angle(g139,g145) = 0.314159
    c: Angle(g145,g151) = 0.314159
    c: Angle(g151,g157) = 0.314159
    c: Coincident(g187,g100)
    c: PointOnObject(g188,g101)
    c: Angle(g157,g187) = 0.314159
    c: PointOnObject(g164,g101)
    c: Coincident(g163,g100)
    c: Angle(g187,g163) = 0.314159
    c: Coincident(g169,g100)
    c: Coincident(g175,g100)
    c: Coincident(g181,g100)
    c: PointOnObject(g170,g101)
    c: PointOnObject(g176,g101)
    c: PointOnObject(g182,g101)
    c: Angle(g175,g181) = 0.314159
    c: Angle(g169,g175) = 0.314159
    c: Angle(g163,g169) = 0.314159
    c: Coincident(g193,g100)
    c: PointOnObject(g194,g101)
    c: Angle(g181,g193) = 0.314159
    c: PointOnObject(g199,g102)
    c: Diameter(g199) = 4
    c: DistanceY(g199,g100) = 10
    c: DistanceX(g100,g0) = 30
    c: DistanceY(g100,g0) = 0
    c: Diameter(g200) = 10
    c: Coincident(g201,g200)
    c: Diameter(g201) = 24
    c: Coincident(g202,g200)
    c: PointOnObject(g202,g201)
    c: DistanceX(g202,g202) = 0
    c: Coincident(g203,g200)
    c: Angle(g202,g203) = 0.785398
    c: PointOnObject(g203,g201)
    c: Coincident(g204,g203)
    c: Coincident(g205,g204)
    c: Coincident(g206,g205)
    c: Coincident(g207,g206)
    c: Coincident(g208,g207)
    c: Coincident(g208,g204)
    c: Perpendicular(g203,g208)
    c: Equal(g208,g204)
    c: Parallel(g205,g207)
    c: Equal(g207,g205)
    c: Parallel(g204,g208)
    c: Perpendicular(g204,g205)
    c: Distance(g207) = 4
    c: Distance(g208) = 0.5
    c: Coincident(g210,g209)
    c: Coincident(g211,g210)
    c: Coincident(g212,g211)
    c: Coincident(g213,g212)
    c: Coincident(g214,g213)
    c: Coincident(g214,g210)
    c: Perpendicular(g209,g214)
    c: Equal(g214,g210)
    c: Parallel(g211,g213)
    c: Equal(g213,g211)
    c: Parallel(g210,g214)
    c: Perpendicular(g210,g211)
    c: Equal(g207,g213) = 4
    c: Equal(g208,g214) = 0.5
    c: Coincident(g216,g215)
    c: Coincident(g217,g216)
    c: Coincident(g218,g217)
    c: Coincident(g219,g218)
    c: Coincident(g220,g219)
    c: Coincident(g220,g216)
    c: Perpendicular(g215,g220)
    c: Equal(g220,g216)
    c: Parallel(g217,g219)
    c: Equal(g219,g217)
    c: Parallel(g216,g220)
    c: Perpendicular(g216,g217)
    c: Equal(g207,g219) = 4
    c: Equal(g208,g220) = 0.5
    c: Coincident(g222,g221)
    c: Coincident(g223,g222)
    c: Coincident(g224,g223)
    c: Coincident(g225,g224)
    c: Coincident(g226,g225)
    c: Coincident(g226,g222)
    c: Perpendicular(g221,g226)
    c: Equal(g226,g222)
    c: Parallel(g223,g225)
    c: Equal(g225,g223)
    c: Parallel(g222,g226)
    c: Perpendicular(g222,g223)
    c: Equal(g207,g225) = 4
    c: Equal(g208,g226) = 0.5
    c: Coincident(g228,g227)
    c: Coincident(g229,g228)
    c: Coincident(g230,g229)
    c: Coincident(g231,g230)
    c: Coincident(g232,g231)
    c: Coincident(g232,g228)
    c: Perpendicular(g227,g232)
    c: Equal(g232,g228)
    c: Parallel(g229,g231)
    c: Equal(g231,g229)
    c: Parallel(g228,g232)
    c: Perpendicular(g228,g229)
    c: Equal(g207,g231) = 4
    c: Equal(g208,g232) = 0.5
    c: Coincident(g234,g233)
    c: Coincident(g235,g234)
    c: Coincident(g236,g235)
    c: Coincident(g237,g236)
    c: Coincident(g238,g237)
    c: Coincident(g238,g234)
    c: Perpendicular(g233,g238)
    c: Equal(g238,g234)
    c: Parallel(g235,g237)
    c: Equal(g237,g235)
    c: Parallel(g234,g238)
    c: Perpendicular(g234,g235)
    c: Equal(g207,g237) = 4
    c: Equal(g208,g238) = 0.5
    c: Coincident(g240,g239)
    c: Coincident(g241,g240)
    c: Coincident(g242,g241)
    c: Coincident(g243,g242)
    c: Coincident(g244,g243)
    c: Coincident(g244,g240)
    c: Perpendicular(g239,g244)
    c: Equal(g244,g240)
    c: Parallel(g241,g243)
    c: Equal(g243,g241)
    c: Parallel(g240,g244)
    c: Perpendicular(g240,g241)
    c: Equal(g207,g243) = 4
    c: Equal(g208,g244) = 0.5
    c: Coincident(g246,g245)
    c: Coincident(g247,g246)
    c: Coincident(g248,g247)
    c: Coincident(g249,g248)
    c: Coincident(g250,g249)
    c: Coincident(g250,g246)
    c: Perpendicular(g245,g250)
    c: Equal(g250,g246)
    c: Parallel(g247,g249)
    c: Equal(g249,g247)
    c: Parallel(g246,g250)
    c: Perpendicular(g246,g247)
    c: Equal(g207,g249) = 4
    c: Equal(g208,g250) = 0.5
    c: Coincident(g252,g251)
    c: Coincident(g253,g252)
    c: Coincident(g254,g253)
    c: Coincident(g255,g254)
    c: Coincident(g256,g255)
    c: Coincident(g256,g252)
    c: Perpendicular(g251,g256)
    c: Equal(g256,g252)
    c: Parallel(g253,g255)
    c: Equal(g255,g253)
    c: Parallel(g252,g256)
    c: Perpendicular(g252,g253)
    c: Equal(g207,g255) = 4
    c: Equal(g208,g256) = 0.5
    c: Coincident(g258,g257)
    c: Coincident(g259,g258)
    c: Coincident(g260,g259)
    c: Coincident(g261,g260)
    c: Coincident(g262,g261)
    c: Coincident(g262,g258)
    c: Perpendicular(g257,g262)
    c: Equal(g262,g258)
    c: Parallel(g259,g261)
    c: Equal(g261,g259)
    c: Parallel(g258,g262)
    c: Perpendicular(g258,g259)
    c: Equal(g207,g261) = 4
    c: Equal(g208,g262) = 0.5
    c: Coincident(g264,g263)
    c: Coincident(g265,g264)
    c: Coincident(g266,g265)
    c: Coincident(g267,g266)
    c: Coincident(g268,g267)
    c: Coincident(g268,g264)
    c: Perpendicular(g263,g268)
    c: Equal(g268,g264)
    c: Parallel(g265,g267)
    c: Equal(g267,g265)
    c: Parallel(g264,g268)
    c: Perpendicular(g264,g265)
    c: Equal(g207,g267) = 4
    c: Equal(g208,g268) = 0.5
    c: Coincident(g270,g269)
    c: Coincident(g271,g270)
    c: Coincident(g272,g271)
    c: Coincident(g273,g272)
    c: Coincident(g274,g273)
    c: Coincident(g274,g270)
    c: Perpendicular(g269,g274)
    c: Equal(g274,g270)
    c: Parallel(g271,g273)
    c: Equal(g273,g271)
    c: Parallel(g270,g274)
    c: Perpendicular(g270,g271)
    c: Equal(g207,g273) = 4
    c: Equal(g208,g274) = 0.5
    c: Coincident(g276,g275)
    c: Coincident(g277,g276)
    c: Coincident(g278,g277)
    c: Coincident(g279,g278)
    c: Coincident(g280,g279)
    c: Coincident(g280,g276)
    c: Perpendicular(g275,g280)
    c: Equal(g280,g276)
    c: Parallel(g277,g279)
    c: Equal(g279,g277)
    c: Parallel(g276,g280)
    c: Perpendicular(g276,g277)
    c: Equal(g207,g279) = 4
    c: Equal(g208,g280) = 0.5
    c: Coincident(g282,g281)
    c: Coincident(g283,g282)
    c: Coincident(g284,g283)
    c: Coincident(g285,g284)
    c: Coincident(g286,g285)
    c: Coincident(g286,g282)
    c: Perpendicular(g281,g286)
    c: Equal(g286,g282)
    c: Parallel(g283,g285)
    c: Equal(g285,g283)
    c: Parallel(g282,g286)
    c: Perpendicular(g282,g283)
    c: Equal(g207,g285) = 4
    c: Equal(g208,g286) = 0.5
    c: Coincident(g288,g287)
    c: Coincident(g289,g288)
    c: Coincident(g290,g289)
    c: Coincident(g291,g290)
    c: Coincident(g292,g291)
    c: Coincident(g292,g288)
    c: Perpendicular(g287,g292)
    c: Equal(g292,g288)
    c: Parallel(g289,g291)
    c: Equal(g291,g289)
    c: Parallel(g288,g292)
    c: Perpendicular(g288,g289)
    c: Equal(g207,g291) = 4
    c: Equal(g208,g292) = 0.5
    c: Coincident(g294,g293)
    c: Coincident(g295,g294)
    c: Coincident(g296,g295)
    c: Coincident(g297,g296)
    c: Coincident(g298,g297)
    c: Coincident(g298,g294)
    c: Perpendicular(g293,g298)
    c: Equal(g298,g294)
    c: Parallel(g295,g297)
    c: Equal(g297,g295)
    c: Parallel(g294,g298)
    c: Perpendicular(g294,g295)
    c: Equal(g207,g297) = 4
    c: Equal(g208,g298) = 0.5
    c: Coincident(g209,g200)
    c: PointOnObject(g210,g201)
    c: Angle(g203,g209) = 0.314159
    c: Coincident(g215,g200)
    c: PointOnObject(g216,g201)
    c: Angle(g209,g215) = 0.314159
    c: PointOnObject(g222,g201)
    c: Coincident(g221,g200)
    c: Angle(g215,g221) = 0.314159
    c: Coincident(g200,g227)
    c: Coincident(g200,g233)
    c: Coincident(g239,g200)
    c: PointOnObject(g228,g201)
    c: PointOnObject(g234,g201)
    c: PointOnObject(g240,g201)
    c: Angle(g221,g227) = 0.314159
    c: Angle(g227,g233) = 0.314159
    c: Angle(g233,g239) = 0.314159
    c: PointOnObject(g246,g201)
    c: PointOnObject(g252,g201)
    c: PointOnObject(g258,g201)
    c: Coincident(g245,g200)
    c: Coincident(g251,g200)
    c: Coincident(g257,g200)
    c: Angle(g239,g245) = 0.314159
    c: Angle(g245,g251) = 0.314159
    c: Angle(g251,g257) = 0.314159
    c: Coincident(g287,g200)
    c: PointOnObject(g288,g201)
    c: Angle(g257,g287) = 0.314159
    c: PointOnObject(g264,g201)
    c: Coincident(g263,g200)
    c: Angle(g287,g263) = 0.314159
    c: Coincident(g269,g200)
    c: Coincident(g275,g200)
    c: Coincident(g281,g200)
    c: PointOnObject(g270,g201)
    c: PointOnObject(g276,g201)
    c: PointOnObject(g282,g201)
    c: Angle(g275,g281) = 0.314159
    c: Angle(g269,g275) = 0.314159
    c: Angle(g263,g269) = 0.314159
    c: Coincident(g293,g200)
    c: PointOnObject(g294,g201)
    c: Angle(g281,g293) = 0.314159
    c: PointOnObject(g299,g202)
    c: Diameter(g299) = 4
    c: DistanceY(g299,g200) = 10
    c: Diameter(g300) = 10
    c: Coincident(g301,g300)
    c: Diameter(g301) = 24
    c: Coincident(g302,g300)
    c: PointOnObject(g302,g301)
    c: DistanceX(g302,g302) = 0
    c: Coincident(g303,g300)
    c: Angle(g302,g303) = 0.785398
    c: PointOnObject(g303,g301)
    c: Coincident(g304,g303)
    c: Coincident(g305,g304)
    c: Coincident(g306,g305)
    c: Coincident(g307,g306)
    c: Coincident(g308,g307)
    c: Coincident(g308,g304)
    c: Perpendicular(g303,g308)
    c: Equal(g308,g304)
    c: Parallel(g305,g307)
    c: Equal(g307,g305)
    c: Parallel(g304,g308)
    c: Perpendicular(g304,g305)
    c: Distance(g307) = 4
    c: Distance(g308) = 0.5
    c: Coincident(g310,g309)
    c: Coincident(g311,g310)
    c: Coincident(g312,g311)
    c: Coincident(g313,g312)
    c: Coincident(g314,g313)
    c: Coincident(g314,g310)
    c: Perpendicular(g309,g314)
    c: Equal(g314,g310)
    c: Parallel(g311,g313)
    c: Equal(g313,g311)
    c: Parallel(g310,g314)
    c: Perpendicular(g310,g311)
    c: Equal(g307,g313) = 4
    c: Equal(g308,g314) = 0.5
    c: Coincident(g316,g315)
    c: Coincident(g317,g316)
    c: Coincident(g318,g317)
    c: Coincident(g319,g318)
    c: Coincident(g320,g319)
    c: Coincident(g320,g316)
    c: Perpendicular(g315,g320)
    c: Equal(g320,g316)
    c: Parallel(g317,g319)
    c: Equal(g319,g317)
    c: Parallel(g316,g320)
    c: Perpendicular(g316,g317)
    c: Equal(g307,g319) = 4
    c: Equal(g308,g320) = 0.5
    c: Coincident(g322,g321)
    c: Coincident(g323,g322)
    c: Coincident(g324,g323)
    c: Coincident(g325,g324)
    c: Coincident(g326,g325)
    c: Coincident(g326,g322)
    c: Perpendicular(g321,g326)
    c: Equal(g326,g322)
    c: Parallel(g323,g325)
    c: Equal(g325,g323)
    c: Parallel(g322,g326)
    c: Perpendicular(g322,g323)
    c: Equal(g307,g325) = 4
    c: Equal(g308,g326) = 0.5
    c: Coincident(g328,g327)
    c: Coincident(g329,g328)
    c: Coincident(g330,g329)
    c: Coincident(g331,g330)
    c: Coincident(g332,g331)
    c: Coincident(g332,g328)
    c: Perpendicular(g327,g332)
    c: Equal(g332,g328)
    c: Parallel(g329,g331)
    c: Equal(g331,g329)
    c: Parallel(g328,g332)
    c: Perpendicular(g328,g329)
    c: Equal(g307,g331) = 4
    c: Equal(g308,g332) = 0.5
    c: Coincident(g334,g333)
    c: Coincident(g335,g334)
    c: Coincident(g336,g335)
    c: Coincident(g337,g336)
    c: Coincident(g338,g337)
    c: Coincident(g338,g334)
    c: Perpendicular(g333,g338)
    c: Equal(g338,g334)
    c: Parallel(g335,g337)
    c: Equal(g337,g335)
    c: Parallel(g334,g338)
    c: Perpendicular(g334,g335)
    c: Equal(g307,g337) = 4
    c: Equal(g308,g338) = 0.5
    c: Coincident(g340,g339)
    c: Coincident(g341,g340)
    c: Coincident(g342,g341)
    c: Coincident(g343,g342)
    c: Coincident(g344,g343)
    c: Coincident(g344,g340)
    c: Perpendicular(g339,g344)
    c: Equal(g344,g340)
    c: Parallel(g341,g343)
    c: Equal(g343,g341)
    c: Parallel(g340,g344)
    c: Perpendicular(g340,g341)
    c: Equal(g307,g343) = 4
    c: Equal(g308,g344) = 0.5
    c: Coincident(g346,g345)
    c: Coincident(g347,g346)
    c: Coincident(g348,g347)
    c: Coincident(g349,g348)
    c: Coincident(g350,g349)
    c: Coincident(g350,g346)
    c: Perpendicular(g345,g350)
    c: Equal(g350,g346)
    c: Parallel(g347,g349)
    c: Equal(g349,g347)
    c: Parallel(g346,g350)
    c: Perpendicular(g346,g347)
    c: Equal(g307,g349) = 4
    c: Equal(g308,g350) = 0.5
    c: Coincident(g352,g351)
    c: Coincident(g353,g352)
    c: Coincident(g354,g353)
    c: Coincident(g355,g354)
    c: Coincident(g356,g355)
    c: Coincident(g356,g352)
    c: Perpendicular(g351,g356)
    c: Equal(g356,g352)
    c: Parallel(g353,g355)
    c: Equal(g355,g353)
    c: Parallel(g352,g356)
    c: Perpendicular(g352,g353)
    c: Equal(g307,g355) = 4
    c: Equal(g308,g356) = 0.5
    c: Coincident(g358,g357)
    c: Coincident(g359,g358)
    c: Coincident(g360,g359)
    c: Coincident(g361,g360)
    c: Coincident(g362,g361)
    c: Coincident(g362,g358)
    c: Perpendicular(g357,g362)
    c: Equal(g362,g358)
    c: Parallel(g359,g361)
    c: Equal(g361,g359)
    c: Parallel(g358,g362)
    c: Perpendicular(g358,g359)
    c: Equal(g307,g361) = 4
    c: Equal(g308,g362) = 0.5
    c: Coincident(g364,g363)
    c: Coincident(g365,g364)
    c: Coincident(g366,g365)
    c: Coincident(g367,g366)
    c: Coincident(g368,g367)
    c: Coincident(g368,g364)
    c: Perpendicular(g363,g368)
    c: Equal(g368,g364)
    c: Parallel(g365,g367)
    c: Equal(g367,g365)
    c: Parallel(g364,g368)
    c: Perpendicular(g364,g365)
    c: Equal(g307,g367) = 4
    c: Equal(g308,g368) = 0.5
    c: Coincident(g370,g369)
    c: Coincident(g371,g370)
    c: Coincident(g372,g371)
    c: Coincident(g373,g372)
    c: Coincident(g374,g373)
    c: Coincident(g374,g370)
    c: Perpendicular(g369,g374)
    c: Equal(g374,g370)
    c: Parallel(g371,g373)
    c: Equal(g373,g371)
    c: Parallel(g370,g374)
    c: Perpendicular(g370,g371)
    c: Equal(g307,g373) = 4
    c: Equal(g308,g374) = 0.5
    c: Coincident(g376,g375)
    c: Coincident(g377,g376)
    c: Coincident(g378,g377)
    c: Coincident(g379,g378)
    c: Coincident(g380,g379)
    c: Coincident(g380,g376)
    c: Perpendicular(g375,g380)
    c: Equal(g380,g376)
    c: Parallel(g377,g379)
    c: Equal(g379,g377)
    c: Parallel(g376,g380)
    c: Perpendicular(g376,g377)
    c: Equal(g307,g379) = 4
    c: Equal(g308,g380) = 0.5
    c: Coincident(g382,g381)
    c: Coincident(g383,g382)
    c: Coincident(g384,g383)
    c: Coincident(g385,g384)
    c: Coincident(g386,g385)
    c: Coincident(g386,g382)
    c: Perpendicular(g381,g386)
    c: Equal(g386,g382)
    c: Parallel(g383,g385)
    c: Equal(g385,g383)
    c: Parallel(g382,g386)
    c: Perpendicular(g382,g383)
    c: Equal(g307,g385) = 4
    c: Equal(g308,g386) = 0.5
    c: Coincident(g388,g387)
    c: Coincident(g389,g388)
    c: Coincident(g390,g389)
    c: Coincident(g391,g390)
    c: Coincident(g392,g391)
    c: Coincident(g392,g388)
    c: Perpendicular(g387,g392)
    c: Equal(g392,g388)
    c: Parallel(g389,g391)
    c: Equal(g391,g389)
    c: Parallel(g388,g392)
    c: Perpendicular(g388,g389)
    c: Equal(g307,g391) = 4
    c: Equal(g308,g392) = 0.5
    c: Coincident(g394,g393)
    c: Coincident(g395,g394)
    c: Coincident(g396,g395)
    c: Coincident(g397,g396)
    c: Coincident(g398,g397)
    c: Coincident(g398,g394)
    c: Perpendicular(g393,g398)
    c: Equal(g398,g394)
    c: Parallel(g395,g397)
    c: Equal(g397,g395)
    c: Parallel(g394,g398)
    c: Perpendicular(g394,g395)
    c: Equal(g307,g397) = 4
    c: Equal(g308,g398) = 0.5
    c: Coincident(g309,g300)
    c: PointOnObject(g310,g301)
    c: Angle(g303,g309) = 0.314159
    c: Coincident(g315,g300)
    c: PointOnObject(g316,g301)
    c: Angle(g309,g315) = 0.314159
    c: PointOnObject(g322,g301)
    c: Coincident(g321,g300)
    c: Angle(g315,g321) = 0.314159
    c: Coincident(g300,g327)
    c: Coincident(g300,g333)
    c: Coincident(g339,g300)
    c: PointOnObject(g328,g301)
    c: PointOnObject(g334,g301)
    c: PointOnObject(g340,g301)
    c: Angle(g321,g327) = 0.314159
    c: Angle(g327,g333) = 0.314159
    c: Angle(g333,g339) = 0.314159
    c: PointOnObject(g346,g301)
    c: PointOnObject(g352,g301)
    c: PointOnObject(g358,g301)
    c: Coincident(g345,g300)
    c: Coincident(g351,g300)
    c: Coincident(g357,g300)
    c: Angle(g339,g345) = 0.314159
    c: Angle(g345,g351) = 0.314159
    c: Angle(g351,g357) = 0.314159
    c: Coincident(g387,g300)
    c: PointOnObject(g388,g301)
    c: Angle(g357,g387) = 0.314159
    c: PointOnObject(g364,g301)
    c: Coincident(g363,g300)
    c: Angle(g387,g363) = 0.314159
    c: Coincident(g369,g300)
    c: Coincident(g375,g300)
    c: Coincident(g381,g300)
    c: PointOnObject(g370,g301)
    c: PointOnObject(g376,g301)
    c: PointOnObject(g382,g301)
    c: Angle(g375,g381) = 0.314159
    c: Angle(g369,g375) = 0.314159
    c: Angle(g363,g369) = 0.314159
    c: Coincident(g393,g300)
    c: PointOnObject(g394,g301)
    c: Angle(g381,g393) = 0.314159
    c: PointOnObject(g399,g302)
    c: Diameter(g399) = 4
    c: DistanceY(g399,g300) = 10
    c: DistanceX(g300,g200) = 30
    c: DistanceY(g300,g200) = 0
    c: DistanceX(g200,g100) = 30
    c: DistanceY(g200,g100) = 0
    c: Diameter(g400) = 10
    c: Coincident(g401,g400)
    c: Diameter(g401) = 24
    c: Coincident(g402,g400)
    c: PointOnObject(g402,g401)
    c: DistanceX(g402,g402) = 0
    c: Coincident(g403,g400)
    c: Angle(g402,g403) = 0.785398
    c: PointOnObject(g403,g401)
    c: Coincident(g404,g403)
    c: Coincident(g405,g404)
    c: Coincident(g406,g405)
    c: Coincident(g407,g406)
    c: Coincident(g408,g407)
    c: Coincident(g408,g404)
    c: Perpendicular(g403,g408)
    c: Equal(g408,g404)
    c: Parallel(g405,g407)
    c: Equal(g407,g405)
    c: Parallel(g404,g408)
    c: Perpendicular(g404,g405)
    c: Distance(g407) = 4
    c: Distance(g408) = 0.5
    c: Coincident(g410,g409)
    c: Coincident(g411,g410)
    c: Coincident(g412,g411)
    c: Coincident(g413,g412)
    c: Coincident(g414,g413)
    c: Coincident(g414,g410)
    c: Perpendicular(g409,g414)
    c: Equal(g414,g410)
    c: Parallel(g411,g413)
    c: Equal(g413,g411)
    c: Parallel(g410,g414)
    c: Perpendicular(g410,g411)
    c: Equal(g407,g413) = 4
    c: Equal(g408,g414) = 0.5
    c: Coincident(g416,g415)
    c: Coincident(g417,g416)
    c: Coincident(g418,g417)
    c: Coincident(g419,g418)
    c: Coincident(g420,g419)
    c: Coincident(g420,g416)
    c: Perpendicular(g415,g420)
    c: Equal(g420,g416)
    c: Parallel(g417,g419)
    c: Equal(g419,g417)
    c: Parallel(g416,g420)
    c: Perpendicular(g416,g417)
    c: Equal(g407,g419) = 4
    c: Equal(g408,g420) = 0.5
    c: Coincident(g422,g421)
    c: Coincident(g423,g422)
    c: Coincident(g424,g423)
    c: Coincident(g425,g424)
    c: Coincident(g426,g425)
    c: Coincident(g426,g422)
    c: Perpendicular(g421,g426)
    c: Equal(g426,g422)
    c: Parallel(g423,g425)
    c: Equal(g425,g423)
    c: Parallel(g422,g426)
    c: Perpendicular(g422,g423)
    c: Equal(g407,g425) = 4
    c: Equal(g408,g426) = 0.5
    c: Coincident(g428,g427)
    c: Coincident(g429,g428)
    c: Coincident(g430,g429)
    c: Coincident(g431,g430)
    c: Coincident(g432,g431)
    c: Coincident(g432,g428)
    c: Perpendicular(g427,g432)
    c: Equal(g432,g428)
    c: Parallel(g429,g431)
    c: Equal(g431,g429)
    c: Parallel(g428,g432)
    c: Perpendicular(g428,g429)
    c: Equal(g407,g431) = 4
    c: Equal(g408,g432) = 0.5
    c: Coincident(g434,g433)
    c: Coincident(g435,g434)
    c: Coincident(g436,g435)
    c: Coincident(g437,g436)
    c: Coincident(g438,g437)
    c: Coincident(g438,g434)
    c: Perpendicular(g433,g438)
    c: Equal(g438,g434)
    c: Parallel(g435,g437)
    c: Equal(g437,g435)
    c: Parallel(g434,g438)
    c: Perpendicular(g434,g435)
    c: Equal(g407,g437) = 4
    c: Equal(g408,g438) = 0.5
    c: Coincident(g440,g439)
    c: Coincident(g441,g440)
    c: Coincident(g442,g441)
    c: Coincident(g443,g442)
    c: Coincident(g444,g443)
    c: Coincident(g444,g440)
    c: Perpendicular(g439,g444)
    c: Equal(g444,g440)
    c: Parallel(g441,g443)
    c: Equal(g443,g441)
    c: Parallel(g440,g444)
    c: Perpendicular(g440,g441)
    c: Equal(g407,g443) = 4
    c: Equal(g408,g444) = 0.5
    c: Coincident(g446,g445)
    c: Coincident(g447,g446)
    c: Coincident(g448,g447)
    c: Coincident(g449,g448)
    c: Coincident(g450,g449)
    c: Coincident(g450,g446)
    c: Perpendicular(g445,g450)
    c: Equal(g450,g446)
    c: Parallel(g447,g449)
    c: Equal(g449,g447)
    c: Parallel(g446,g450)
    c: Perpendicular(g446,g447)
    c: Equal(g407,g449) = 4
    c: Equal(g408,g450) = 0.5
    c: Coincident(g452,g451)
    c: Coincident(g453,g452)
    c: Coincident(g454,g453)
    c: Coincident(g455,g454)
    c: Coincident(g456,g455)
    c: Coincident(g456,g452)
    c: Perpendicular(g451,g456)
    c: Equal(g456,g452)
    c: Parallel(g453,g455)
    c: Equal(g455,g453)
    c: Parallel(g452,g456)
    c: Perpendicular(g452,g453)
    c: Equal(g407,g455) = 4
    c: Equal(g408,g456) = 0.5
    c: Coincident(g458,g457)
    c: Coincident(g459,g458)
    c: Coincident(g460,g459)
    c: Coincident(g461,g460)
    c: Coincident(g462,g461)
    c: Coincident(g462,g458)
    c: Perpendicular(g457,g462)
    c: Equal(g462,g458)
    c: Parallel(g459,g461)
    c: Equal(g461,g459)
    c: Parallel(g458,g462)
    c: Perpendicular(g458,g459)
    c: Equal(g407,g461) = 4
    c: Equal(g408,g462) = 0.5
    c: Coincident(g464,g463)
    c: Coincident(g465,g464)
    c: Coincident(g466,g465)
    c: Coincident(g467,g466)
    c: Coincident(g468,g467)
    c: Coincident(g468,g464)
    c: Perpendicular(g463,g468)
    c: Equal(g468,g464)
    c: Parallel(g465,g467)
    c: Equal(g467,g465)
    c: Parallel(g464,g468)
    c: Perpendicular(g464,g465)
    c: Equal(g407,g467) = 4
    c: Equal(g408,g468) = 0.5
    c: Coincident(g470,g469)
    c: Coincident(g471,g470)
    c: Coincident(g472,g471)
    c: Coincident(g473,g472)
    c: Coincident(g474,g473)
    c: Coincident(g474,g470)
    c: Perpendicular(g469,g474)
    c: Equal(g474,g470)
    c: Parallel(g471,g473)
    c: Equal(g473,g471)
    c: Parallel(g470,g474)
    c: Perpendicular(g470,g471)
    c: Equal(g407,g473) = 4
    c: Equal(g408,g474) = 0.5
    c: Coincident(g476,g475)
    c: Coincident(g477,g476)
    c: Coincident(g478,g477)
    c: Coincident(g479,g478)
    c: Coincident(g480,g479)
    c: Coincident(g480,g476)
    c: Perpendicular(g475,g480)
    c: Equal(g480,g476)
    c: Parallel(g477,g479)
    c: Equal(g479,g477)
    c: Parallel(g476,g480)
    c: Perpendicular(g476,g477)
    c: Equal(g407,g479) = 4
    c: Equal(g408,g480) = 0.5
    c: Coincident(g482,g481)
    c: Coincident(g483,g482)
    c: Coincident(g484,g483)
    c: Coincident(g485,g484)
    c: Coincident(g486,g485)
    c: Coincident(g486,g482)
    c: Perpendicular(g481,g486)
    c: Equal(g486,g482)
    c: Parallel(g483,g485)
    c: Equal(g485,g483)
    c: Parallel(g482,g486)
    c: Perpendicular(g482,g483)
    c: Equal(g407,g485) = 4
    c: Equal(g408,g486) = 0.5
    c: Coincident(g488,g487)
    c: Coincident(g489,g488)
    c: Coincident(g490,g489)
    c: Coincident(g491,g490)
    c: Coincident(g492,g491)
    c: Coincident(g492,g488)
    c: Perpendicular(g487,g492)
    c: Equal(g492,g488)
    c: Parallel(g489,g491)
    c: Equal(g491,g489)
    c: Parallel(g488,g492)
    c: Perpendicular(g488,g489)
    c: Equal(g407,g491) = 4
    c: Equal(g408,g492) = 0.5
    c: Coincident(g494,g493)
    c: Coincident(g495,g494)
    c: Coincident(g496,g495)
    c: Coincident(g497,g496)
    c: Coincident(g498,g497)
    c: Coincident(g498,g494)
    c: Perpendicular(g493,g498)
    c: Equal(g498,g494)
    c: Parallel(g495,g497)
    c: Equal(g497,g495)
    c: Parallel(g494,g498)
    c: Perpendicular(g494,g495)
    c: Equal(g407,g497) = 4
    c: Equal(g408,g498) = 0.5
    c: Coincident(g409,g400)
    c: PointOnObject(g410,g401)
    c: Angle(g403,g409) = 0.314159
    c: Coincident(g415,g400)
    c: PointOnObject(g416,g401)
    c: Angle(g409,g415) = 0.314159
    c: PointOnObject(g422,g401)
    c: Coincident(g421,g400)
    c: Angle(g415,g421) = 0.314159
    c: Coincident(g400,g427)
    c: Coincident(g400,g433)
    c: Coincident(g439,g400)
    c: PointOnObject(g428,g401)
    c: PointOnObject(g434,g401)
    c: PointOnObject(g440,g401)
    c: Angle(g421,g427) = 0.314159
    c: Angle(g427,g433) = 0.314159
    c: Angle(g433,g439) = 0.314159
    c: PointOnObject(g446,g401)
    c: PointOnObject(g452,g401)
    c: PointOnObject(g458,g401)
    c: Coincident(g445,g400)
    c: Coincident(g451,g400)
    c: Coincident(g457,g400)
    c: Angle(g439,g445) = 0.314159
    c: Angle(g445,g451) = 0.314159
    c: Angle(g451,g457) = 0.314159
    c: Coincident(g487,g400)
    c: PointOnObject(g488,g401)
    c: Angle(g457,g487) = 0.314159
    c: PointOnObject(g464,g401)
    c: Coincident(g463,g400)
    c: Angle(g487,g463) = 0.314159
    c: Coincident(g469,g400)
    c: Coincident(g475,g400)
    c: Coincident(g481,g400)
    c: PointOnObject(g470,g401)
    c: PointOnObject(g476,g401)
    c: PointOnObject(g482,g401)
    c: Angle(g475,g481) = 0.314159
    c: Angle(g469,g475) = 0.314159
    c: Angle(g463,g469) = 0.314159
    c: Coincident(g493,g400)
    c: PointOnObject(g494,g401)
    c: Angle(g481,g493) = 0.314159
    c: PointOnObject(g499,g402)
    c: Diameter(g499) = 4
    c: DistanceY(g499,g400) = 10
    c: DistanceY(g300,g400) = 0
    c: DistanceX(g400,g300) = 30
FEATURE [PartDesign::Body] Body
  Group = -> [Sketch,Pad,Sketch001,Sketch002,Sketch008,Sketch005,Sketch006,Sketch004,Sketch007,Sketch003,Sketch009]
  Origin = -> Origin
  Tip = -> Pad
